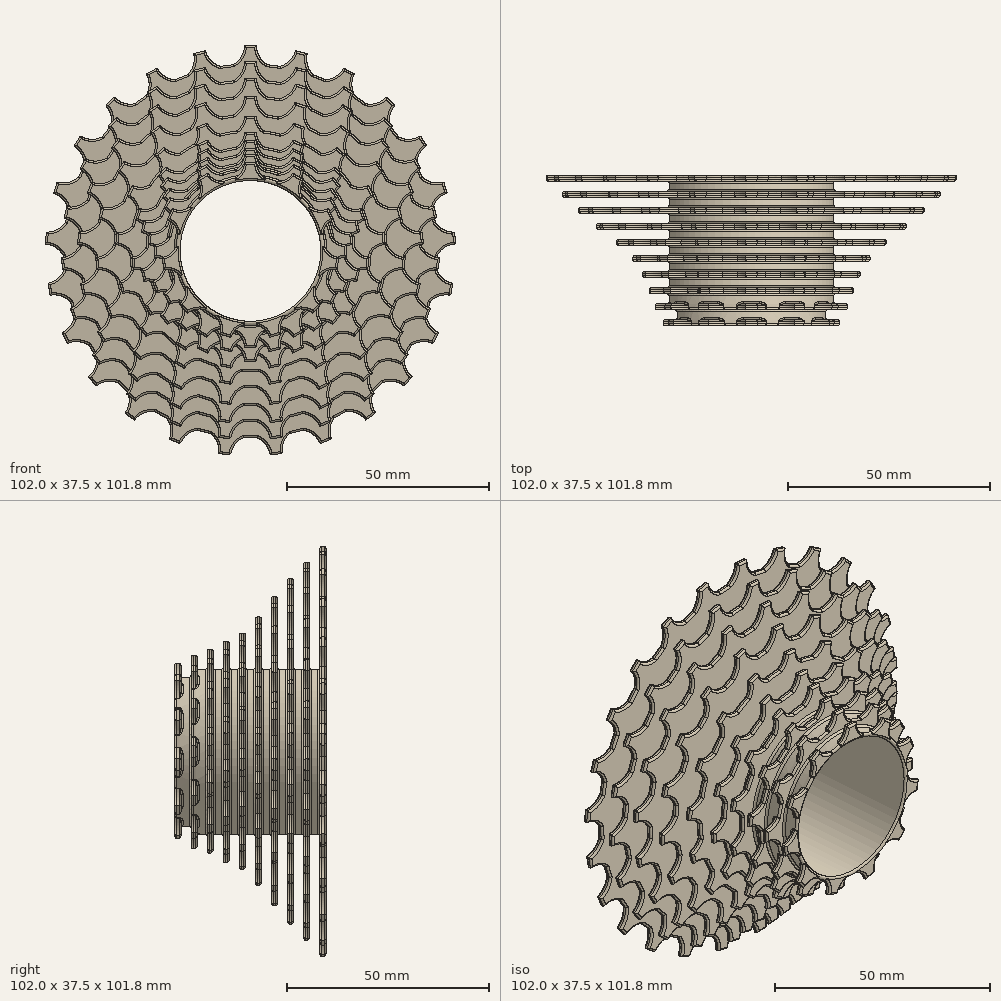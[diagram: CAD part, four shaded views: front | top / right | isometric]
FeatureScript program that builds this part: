
annotation { "Feature Type Name" : "Feature", "Feature Type Description" : "" }
export const myFeature = defineFeature(function(context is Context, id is Id, definition is map)
    precondition{}
    {
        {
            var Q0;
            Q0=qCreatedBy(makeId("Front.planeOp"),FACE);
            var sketch = newSketch(context, id + "F0", { "sketchPlane" : qUnion([Q0])});
            skCircle(sketch, "E0", {"center": v(0, 0) * mm, "radius": 46.5 * mm});
            skLineSegment(sketch, "E1", {"start": v(1.5, 51) * mm, "end": v(-1.5, 51) * mm});
            skLineSegment(sketch, "E2", {"start": v(0, -58.64) * mm, "end": v(0, 66.7) * mm, "construction": true});
            skLineSegment(sketch, "E3", {"start": v(-56.93, 0) * mm, "end": v(57.2, 0) * mm, "construction": true});
            skLineSegment(sketch, "E4", {"start": v(7, 54.15) * mm, "end": v(7, 48.61) * mm, "construction": true});
            skArc(sketch, "E5", {"start": v(1.5, 51) * mm, "mid": v(2.22, 48.3) * mm, "end": v(4.17, 46.31) * mm});
            skArc(sketch, "E6.MirrorCS", {"start": v(-1.5, 51) * mm, "mid": v(-2.22, 48.3) * mm, "end": v(-4.17, 46.31) * mm});
            skLineSegment(sketch, "E7.1.0", {"start": v(-11.23, 49.77) * mm, "end": v(-14.14, 49.02) * mm});
            skArc(sketch, "E7.1.1", {"start": v(-14.14, 49.02) * mm, "mid": v(-14.16, 46.24) * mm, "end": v(-15.56, 43.82) * mm});
            skArc(sketch, "E7.1.2", {"start": v(-11.23, 49.77) * mm, "mid": v(-9.86, 47.34) * mm, "end": v(-7.48, 45.9) * mm});
            skLineSegment(sketch, "E7.2.0", {"start": v(-23.25, 45.41) * mm, "end": v(-25.88, 43.97) * mm});
            skArc(sketch, "E7.2.1", {"start": v(-25.88, 43.97) * mm, "mid": v(-25.22, 41.26) * mm, "end": v(-25.97, 38.58) * mm});
            skArc(sketch, "E7.2.2", {"start": v(-23.25, 45.41) * mm, "mid": v(-21.33, 43.4) * mm, "end": v(-18.66, 42.6) * mm});
            skLineSegment(sketch, "E7.3.0", {"start": v(-33.82, 38.2) * mm, "end": v(-36, 36.15) * mm});
            skArc(sketch, "E7.3.1", {"start": v(-36, 36.15) * mm, "mid": v(-34.69, 33.7) * mm, "end": v(-34.74, 30.9) * mm});
            skArc(sketch, "E7.3.2", {"start": v(-33.82, 38.2) * mm, "mid": v(-31.45, 36.73) * mm, "end": v(-28.66, 36.62) * mm});
            skLineSegment(sketch, "E7.4.0", {"start": v(-42.26, 28.6) * mm, "end": v(-43.86, 26.06) * mm});
            skArc(sketch, "E7.4.1", {"start": v(-43.86, 26.06) * mm, "mid": v(-41.98, 24) * mm, "end": v(-41.34, 21.3) * mm});
            skArc(sketch, "E7.4.2", {"start": v(-42.26, 28.6) * mm, "mid": v(-39.6, 27.76) * mm, "end": v(-36.87, 28.34) * mm});
            skLineSegment(sketch, "E7.5.0", {"start": v(-48.04, 17.19) * mm, "end": v(-48.97, 14.33) * mm});
            skArc(sketch, "E7.5.1", {"start": v(-48.97, 14.33) * mm, "mid": v(-46.63, 12.82) * mm, "end": v(-45.33, 10.35) * mm});
            skArc(sketch, "E7.5.2", {"start": v(-48.04, 17.19) * mm, "mid": v(-45.26, 17.04) * mm, "end": v(-42.76, 18.28) * mm});
            skLineSegment(sketch, "E7.6.0", {"start": v(-50.8, 4.7) * mm, "end": v(-51, 1.7) * mm});
            skArc(sketch, "E7.6.1", {"start": v(-51, 1.7) * mm, "mid": v(-48.35, 0.82) * mm, "end": v(-46.48, -1.25) * mm});
            skArc(sketch, "E7.6.2", {"start": v(-50.8, 4.7) * mm, "mid": v(-48.07, 5.25) * mm, "end": v(-45.96, 7.07) * mm});
            skLineSegment(sketch, "E7.7.0", {"start": v(-50.38, -8.08) * mm, "end": v(-49.82, -11.03) * mm});
            skArc(sketch, "E7.7.1", {"start": v(-49.82, -11.03) * mm, "mid": v(-47.03, -11.23) * mm, "end": v(-44.71, -12.77) * mm});
            skArc(sketch, "E7.7.2", {"start": v(-50.38, -8.08) * mm, "mid": v(-47.87, -6.87) * mm, "end": v(-46.27, -4.58) * mm});
            skLineSegment(sketch, "E7.8.0", {"start": v(-46.78, -20.36) * mm, "end": v(-45.5, -23.07) * mm});
            skArc(sketch, "E7.8.1", {"start": v(-45.5, -23.07) * mm, "mid": v(-42.76, -22.58) * mm, "end": v(-40.13, -23.5) * mm});
            skArc(sketch, "E7.8.2", {"start": v(-46.78, -20.36) * mm, "mid": v(-44.65, -18.56) * mm, "end": v(-43.68, -15.95) * mm});
            skLineSegment(sketch, "E7.9.0", {"start": v(-40.25, -31.35) * mm, "end": v(-38.34, -33.66) * mm});
            skArc(sketch, "E7.9.1", {"start": v(-38.34, -33.66) * mm, "mid": v(-35.8, -32.5) * mm, "end": v(-33.03, -32.73) * mm});
            skArc(sketch, "E7.9.2", {"start": v(-40.25, -31.35) * mm, "mid": v(-38.64, -29.08) * mm, "end": v(-38.34, -26.3) * mm});
            skLineSegment(sketch, "E7.10.0", {"start": v(-31.2, -40.38) * mm, "end": v(-28.76, -42.14) * mm});
            skArc(sketch, "E7.10.1", {"start": v(-28.76, -42.14) * mm, "mid": v(-26.6, -40.39) * mm, "end": v(-23.85, -39.92) * mm});
            skArc(sketch, "E7.10.2", {"start": v(-31.2, -40.38) * mm, "mid": v(-30.2, -37.78) * mm, "end": v(-30.6, -35.02) * mm});
            skLineSegment(sketch, "E7.11.0", {"start": v(-20.17, -46.87) * mm, "end": v(-17.38, -47.97) * mm});
            skArc(sketch, "E7.11.1", {"start": v(-17.38, -47.97) * mm, "mid": v(-15.72, -45.73) * mm, "end": v(-13.17, -44.6) * mm});
            skArc(sketch, "E7.11.2", {"start": v(-20.17, -46.87) * mm, "mid": v(-19.85, -44.1) * mm, "end": v(-20.93, -41.53) * mm});
            skLineSegment(sketch, "E7.12.0", {"start": v(-7.88, -50.4) * mm, "end": v(-4.9, -50.79) * mm});
            skArc(sketch, "E7.12.1", {"start": v(-4.9, -50.79) * mm, "mid": v(-3.85, -48.2) * mm, "end": v(-1.67, -46.47) * mm});
            skArc(sketch, "E7.12.2", {"start": v(-7.88, -50.4) * mm, "mid": v(-8.26, -47.65) * mm, "end": v(-9.94, -45.42) * mm});
            skLineSegment(sketch, "E7.13.0", {"start": v(4.9, -50.79) * mm, "end": v(7.88, -50.4) * mm});
            skArc(sketch, "E7.13.1", {"start": v(7.88, -50.4) * mm, "mid": v(8.26, -47.65) * mm, "end": v(9.94, -45.42) * mm});
            skArc(sketch, "E7.13.2", {"start": v(4.9, -50.79) * mm, "mid": v(3.85, -48.2) * mm, "end": v(1.67, -46.47) * mm});
            skLineSegment(sketch, "E7.14.0", {"start": v(17.38, -47.97) * mm, "end": v(20.17, -46.87) * mm});
            skArc(sketch, "E7.14.1", {"start": v(20.17, -46.87) * mm, "mid": v(19.85, -44.1) * mm, "end": v(20.93, -41.53) * mm});
            skArc(sketch, "E7.14.2", {"start": v(17.38, -47.97) * mm, "mid": v(15.72, -45.73) * mm, "end": v(13.17, -44.6) * mm});
            skLineSegment(sketch, "E7.15.0", {"start": v(28.76, -42.14) * mm, "end": v(31.2, -40.38) * mm});
            skArc(sketch, "E7.15.1", {"start": v(31.2, -40.38) * mm, "mid": v(30.2, -37.78) * mm, "end": v(30.6, -35.02) * mm});
            skArc(sketch, "E7.15.2", {"start": v(28.76, -42.14) * mm, "mid": v(26.6, -40.39) * mm, "end": v(23.85, -39.92) * mm});
            skLineSegment(sketch, "E7.16.0", {"start": v(38.34, -33.66) * mm, "end": v(40.25, -31.35) * mm});
            skArc(sketch, "E7.16.1", {"start": v(40.25, -31.35) * mm, "mid": v(38.64, -29.08) * mm, "end": v(38.34, -26.3) * mm});
            skArc(sketch, "E7.16.2", {"start": v(38.34, -33.66) * mm, "mid": v(35.8, -32.5) * mm, "end": v(33.03, -32.73) * mm});
            skLineSegment(sketch, "E7.17.0", {"start": v(45.5, -23.07) * mm, "end": v(46.78, -20.36) * mm});
            skArc(sketch, "E7.17.1", {"start": v(46.78, -20.36) * mm, "mid": v(44.65, -18.56) * mm, "end": v(43.68, -15.95) * mm});
            skArc(sketch, "E7.17.2", {"start": v(45.5, -23.07) * mm, "mid": v(42.76, -22.58) * mm, "end": v(40.13, -23.5) * mm});
            skLineSegment(sketch, "E7.18.0", {"start": v(49.82, -11.03) * mm, "end": v(50.38, -8.08) * mm});
            skArc(sketch, "E7.18.1", {"start": v(50.38, -8.08) * mm, "mid": v(47.87, -6.87) * mm, "end": v(46.27, -4.58) * mm});
            skArc(sketch, "E7.18.2", {"start": v(49.82, -11.03) * mm, "mid": v(47.03, -11.23) * mm, "end": v(44.71, -12.77) * mm});
            skLineSegment(sketch, "E7.19.0", {"start": v(51, 1.7) * mm, "end": v(50.8, 4.7) * mm});
            skArc(sketch, "E7.19.1", {"start": v(50.8, 4.7) * mm, "mid": v(48.07, 5.25) * mm, "end": v(45.96, 7.07) * mm});
            skArc(sketch, "E7.19.2", {"start": v(51, 1.7) * mm, "mid": v(48.35, 0.82) * mm, "end": v(46.48, -1.25) * mm});
            skLineSegment(sketch, "E7.20.0", {"start": v(48.97, 14.33) * mm, "end": v(48.04, 17.19) * mm});
            skArc(sketch, "E7.20.1", {"start": v(48.04, 17.19) * mm, "mid": v(45.26, 17.04) * mm, "end": v(42.76, 18.28) * mm});
            skArc(sketch, "E7.20.2", {"start": v(48.97, 14.33) * mm, "mid": v(46.63, 12.82) * mm, "end": v(45.33, 10.35) * mm});
            skLineSegment(sketch, "E7.21.0", {"start": v(43.86, 26.06) * mm, "end": v(42.26, 28.6) * mm});
            skArc(sketch, "E7.21.1", {"start": v(42.26, 28.6) * mm, "mid": v(39.6, 27.76) * mm, "end": v(36.87, 28.34) * mm});
            skArc(sketch, "E7.21.2", {"start": v(43.86, 26.06) * mm, "mid": v(41.98, 24) * mm, "end": v(41.34, 21.3) * mm});
            skLineSegment(sketch, "E7.22.0", {"start": v(36, 36.15) * mm, "end": v(33.82, 38.2) * mm});
            skArc(sketch, "E7.22.1", {"start": v(33.82, 38.2) * mm, "mid": v(31.45, 36.73) * mm, "end": v(28.66, 36.62) * mm});
            skArc(sketch, "E7.22.2", {"start": v(36, 36.15) * mm, "mid": v(34.69, 33.7) * mm, "end": v(34.74, 30.9) * mm});
            skLineSegment(sketch, "E7.23.0", {"start": v(25.88, 43.97) * mm, "end": v(23.25, 45.41) * mm});
            skArc(sketch, "E7.23.1", {"start": v(23.25, 45.41) * mm, "mid": v(21.33, 43.4) * mm, "end": v(18.66, 42.6) * mm});
            skArc(sketch, "E7.23.2", {"start": v(25.88, 43.97) * mm, "mid": v(25.22, 41.26) * mm, "end": v(25.97, 38.58) * mm});
            skLineSegment(sketch, "E7.24.0", {"start": v(14.14, 49.02) * mm, "end": v(11.23, 49.77) * mm});
            skArc(sketch, "E7.24.1", {"start": v(11.23, 49.77) * mm, "mid": v(9.86, 47.34) * mm, "end": v(7.48, 45.9) * mm});
            skArc(sketch, "E7.24.2", {"start": v(14.14, 49.02) * mm, "mid": v(14.16, 46.24) * mm, "end": v(15.56, 43.82) * mm});
            skCircle(sketch, "E8", {"center": v(0, 0) * mm, "radius": 17.5 * mm});
            skSolve(sketch);
        }
        {
            var Q0;
            Q0 = qSketchRegion(id + "F0", true);
            extrude(context, id + "F1", {"entities" : qUnion([Q0]), "depth" : 1.5 * mm, "offsetDistance" : 25 * mm});
        }
        {
            var Q0;
            Q0=makeQuery(id+"F1.opExtrude","CAP_FACE",FACE,{"disambiguationData":[OSD([sQuery(id+"F0.wireOp",EDGE,"E0"),sQuery(id+"F0.wireOp",EDGE,"E1"),sQuery(id+"F0.wireOp",EDGE,"E5"),sQuery(id+"F0.wireOp",EDGE,"E6.MirrorCS"),sQuery(id+"F0.wireOp",EDGE,"E7.1.0"),sQuery(id+"F0.wireOp",EDGE,"E7.1.1"),sQuery(id+"F0.wireOp",EDGE,"E7.1.2"),sQuery(id+"F0.wireOp",EDGE,"E7.2.0"),sQuery(id+"F0.wireOp",EDGE,"E7.2.1"),sQuery(id+"F0.wireOp",EDGE,"E7.2.2"),sQuery(id+"F0.wireOp",EDGE,"E7.3.0"),sQuery(id+"F0.wireOp",EDGE,"E7.3.1"),sQuery(id+"F0.wireOp",EDGE,"E7.3.2"),sQuery(id+"F0.wireOp",EDGE,"E7.4.0"),sQuery(id+"F0.wireOp",EDGE,"E7.4.1"),sQuery(id+"F0.wireOp",EDGE,"E7.4.2"),sQuery(id+"F0.wireOp",EDGE,"E7.5.0"),sQuery(id+"F0.wireOp",EDGE,"E7.5.1"),sQuery(id+"F0.wireOp",EDGE,"E7.5.2"),sQuery(id+"F0.wireOp",EDGE,"E7.6.0"),sQuery(id+"F0.wireOp",EDGE,"E7.6.1"),sQuery(id+"F0.wireOp",EDGE,"E7.6.2"),sQuery(id+"F0.wireOp",EDGE,"E7.7.0"),sQuery(id+"F0.wireOp",EDGE,"E7.7.1"),sQuery(id+"F0.wireOp",EDGE,"E7.7.2"),sQuery(id+"F0.wireOp",EDGE,"E7.8.0"),sQuery(id+"F0.wireOp",EDGE,"E7.8.1"),sQuery(id+"F0.wireOp",EDGE,"E7.8.2"),sQuery(id+"F0.wireOp",EDGE,"E7.9.0"),sQuery(id+"F0.wireOp",EDGE,"E7.9.1"),sQuery(id+"F0.wireOp",EDGE,"E7.9.2"),sQuery(id+"F0.wireOp",EDGE,"E7.10.0"),sQuery(id+"F0.wireOp",EDGE,"E7.10.1"),sQuery(id+"F0.wireOp",EDGE,"E7.10.2"),sQuery(id+"F0.wireOp",EDGE,"E7.11.0"),sQuery(id+"F0.wireOp",EDGE,"E7.11.1"),sQuery(id+"F0.wireOp",EDGE,"E7.11.2"),sQuery(id+"F0.wireOp",EDGE,"E7.12.0"),sQuery(id+"F0.wireOp",EDGE,"E7.12.1"),sQuery(id+"F0.wireOp",EDGE,"E7.12.2"),sQuery(id+"F0.wireOp",EDGE,"E7.13.0"),sQuery(id+"F0.wireOp",EDGE,"E7.13.1"),sQuery(id+"F0.wireOp",EDGE,"E7.13.2"),sQuery(id+"F0.wireOp",EDGE,"E7.14.0"),sQuery(id+"F0.wireOp",EDGE,"E7.14.1"),sQuery(id+"F0.wireOp",EDGE,"E7.14.2"),sQuery(id+"F0.wireOp",EDGE,"E7.15.0"),sQuery(id+"F0.wireOp",EDGE,"E7.15.1"),sQuery(id+"F0.wireOp",EDGE,"E7.15.2"),sQuery(id+"F0.wireOp",EDGE,"E7.16.0"),sQuery(id+"F0.wireOp",EDGE,"E7.16.1"),sQuery(id+"F0.wireOp",EDGE,"E7.16.2"),sQuery(id+"F0.wireOp",EDGE,"E7.17.0"),sQuery(id+"F0.wireOp",EDGE,"E7.17.1"),sQuery(id+"F0.wireOp",EDGE,"E7.17.2"),sQuery(id+"F0.wireOp",EDGE,"E7.18.0"),sQuery(id+"F0.wireOp",EDGE,"E7.18.1"),sQuery(id+"F0.wireOp",EDGE,"E7.18.2"),sQuery(id+"F0.wireOp",EDGE,"E7.19.0"),sQuery(id+"F0.wireOp",EDGE,"E7.19.1"),sQuery(id+"F0.wireOp",EDGE,"E7.19.2"),sQuery(id+"F0.wireOp",EDGE,"E7.20.0"),sQuery(id+"F0.wireOp",EDGE,"E7.20.1"),sQuery(id+"F0.wireOp",EDGE,"E7.20.2"),sQuery(id+"F0.wireOp",EDGE,"E7.21.0"),sQuery(id+"F0.wireOp",EDGE,"E7.21.1"),sQuery(id+"F0.wireOp",EDGE,"E7.21.2"),sQuery(id+"F0.wireOp",EDGE,"E7.22.0"),sQuery(id+"F0.wireOp",EDGE,"E7.22.1"),sQuery(id+"F0.wireOp",EDGE,"E7.22.2"),sQuery(id+"F0.wireOp",EDGE,"E7.23.0"),sQuery(id+"F0.wireOp",EDGE,"E7.23.1"),sQuery(id+"F0.wireOp",EDGE,"E7.23.2"),sQuery(id+"F0.wireOp",EDGE,"E7.24.0"),sQuery(id+"F0.wireOp",EDGE,"E7.24.1"),sQuery(id+"F0.wireOp",EDGE,"E7.24.2"),sQuery(id+"F0.wireOp",EDGE,"E8")])],"isStart":false});
            var sketch = newSketch(context, id + "F2", { "sketchPlane" : qUnion([Q0])});
            skCircle(sketch, "E9", {"center": v(0, 0) * mm, "radius": 20.5 * mm});
            skCircle(sketch, "E10", {"center": v(0, 0) * mm, "radius": 17.5 * mm});
            skSolve(sketch);
        }
        {
            var Q0;
            Q0 = qSketchRegion(id + "F2", true);
            extrude(context, id + "F3", {"entities" : qUnion([Q0]), "operationType" : NewBodyOperationType.ADD, "depth" : 2.5 * mm, "offsetDistance" : 25 * mm});
        }
        {
            var Q0;
            Q0=makeQuery(id+"F3.opExtrude","CAP_FACE",FACE,{"disambiguationData":[OSD([sQuery(id+"F2.wireOp",EDGE,"E9"),sQuery(id+"F2.wireOp",EDGE,"E10")])],"isStart":false});
            var sketch = newSketch(context, id + "F4", { "sketchPlane" : qUnion([Q0])});
            skCircle(sketch, "E11", {"center": v(0, 0) * mm, "radius": 42.5 * mm});
            skLineSegment(sketch, "E12", {"start": v(-1.5, 47) * mm, "end": v(1.5, 47) * mm});
            skArc(sketch, "E13", {"start": v(1.5, 47) * mm, "mid": v(2.2, 44.3) * mm, "end": v(4.15, 42.3) * mm});
            skArc(sketch, "E14.MirrorCS", {"start": v(-1.5, 47) * mm, "mid": v(-2.2, 44.3) * mm, "end": v(-4.15, 42.3) * mm});
            skLineSegment(sketch, "E15.1.0", {"start": v(-14.12, 44.85) * mm, "end": v(-11.24, 45.66) * mm});
            skArc(sketch, "E15.1.1", {"start": v(-14.12, 44.85) * mm, "mid": v(-14.08, 42.06) * mm, "end": v(-15.4, 39.6) * mm});
            skArc(sketch, "E15.1.2", {"start": v(-11.24, 45.66) * mm, "mid": v(-9.83, 43.25) * mm, "end": v(-7.42, 41.85) * mm});
            skLineSegment(sketch, "E15.2.0", {"start": v(-25.7, 39.38) * mm, "end": v(-23.14, 40.94) * mm});
            skArc(sketch, "E15.2.1", {"start": v(-25.7, 39.38) * mm, "mid": v(-24.9, 36.7) * mm, "end": v(-25.52, 33.98) * mm});
            skArc(sketch, "E15.2.2", {"start": v(-23.14, 40.94) * mm, "mid": v(-21.13, 39) * mm, "end": v(-18.43, 38.3) * mm});
            skLineSegment(sketch, "E15.3.0", {"start": v(-35.37, 30.98) * mm, "end": v(-33.33, 33.18) * mm});
            skArc(sketch, "E15.3.1", {"start": v(-35.37, 30.98) * mm, "mid": v(-33.88, 28.62) * mm, "end": v(-33.74, 25.84) * mm});
            skArc(sketch, "E15.3.2", {"start": v(-33.33, 33.18) * mm, "mid": v(-30.87, 31.85) * mm, "end": v(-28.08, 31.9) * mm});
            skLineSegment(sketch, "E15.4.0", {"start": v(-42.42, 20.3) * mm, "end": v(-41.04, 22.95) * mm});
            skArc(sketch, "E15.4.1", {"start": v(-42.42, 20.3) * mm, "mid": v(-40.35, 18.42) * mm, "end": v(-39.46, 15.78) * mm});
            skArc(sketch, "E15.4.2", {"start": v(-41.04, 22.95) * mm, "mid": v(-38.32, 22.34) * mm, "end": v(-35.65, 23.14) * mm});
            skLineSegment(sketch, "E15.5.0", {"start": v(-46.32, 8.1) * mm, "end": v(-45.71, 11.03) * mm});
            skArc(sketch, "E15.5.1", {"start": v(-46.32, 8.1) * mm, "mid": v(-43.82, 6.85) * mm, "end": v(-42.26, 4.54) * mm});
            skArc(sketch, "E15.5.2", {"start": v(-45.71, 11.03) * mm, "mid": v(-42.93, 11.17) * mm, "end": v(-40.57, 12.67) * mm});
            skLineSegment(sketch, "E15.6.0", {"start": v(-46.79, -4.7) * mm, "end": v(-47, -1.71) * mm});
            skArc(sketch, "E15.6.1", {"start": v(-46.79, -4.7) * mm, "mid": v(-44.05, -5.23) * mm, "end": v(-41.92, -7.03) * mm});
            skArc(sketch, "E15.6.2", {"start": v(-47, -1.71) * mm, "mid": v(-44.35, -0.82) * mm, "end": v(-42.48, 1.25) * mm});
            skLineSegment(sketch, "E15.7.0", {"start": v(-43.78, -17.15) * mm, "end": v(-44.79, -14.33) * mm});
            skArc(sketch, "E15.7.1", {"start": v(-43.78, -17.15) * mm, "mid": v(-41, -16.92) * mm, "end": v(-38.47, -18.07) * mm});
            skArc(sketch, "E15.7.2", {"start": v(-44.79, -14.33) * mm, "mid": v(-42.48, -12.76) * mm, "end": v(-41.24, -10.26) * mm});
            skLineSegment(sketch, "E15.8.0", {"start": v(-37.53, -28.33) * mm, "end": v(-39.26, -25.88) * mm});
            skArc(sketch, "E15.8.1", {"start": v(-37.53, -28.33) * mm, "mid": v(-34.92, -27.35) * mm, "end": v(-32.16, -27.78) * mm});
            skArc(sketch, "E15.8.2", {"start": v(-39.26, -25.88) * mm, "mid": v(-37.47, -23.74) * mm, "end": v(-36.95, -21) * mm});
            skLineSegment(sketch, "E15.9.0", {"start": v(-28.5, -37.4) * mm, "end": v(-30.82, -35.51) * mm});
            skArc(sketch, "E15.9.1", {"start": v(-28.5, -37.4) * mm, "mid": v(-26.25, -35.76) * mm, "end": v(-23.48, -35.43) * mm});
            skArc(sketch, "E15.9.2", {"start": v(-30.82, -35.51) * mm, "mid": v(-29.67, -32.97) * mm, "end": v(-29.91, -30.2) * mm});
            skLineSegment(sketch, "E15.10.0", {"start": v(-17.35, -43.7) * mm, "end": v(-20.1, -42.51) * mm});
            skArc(sketch, "E15.10.1", {"start": v(-17.35, -43.7) * mm, "mid": v(-15.62, -41.51) * mm, "end": v(-13.05, -40.45) * mm});
            skArc(sketch, "E15.10.2", {"start": v(-20.1, -42.51) * mm, "mid": v(-19.67, -39.75) * mm, "end": v(-20.66, -37.14) * mm});
            skLineSegment(sketch, "E15.11.0", {"start": v(-4.91, -46.77) * mm, "end": v(-7.89, -46.36) * mm});
            skArc(sketch, "E15.11.1", {"start": v(-4.91, -46.77) * mm, "mid": v(-3.85, -44.19) * mm, "end": v(-1.65, -42.47) * mm});
            skArc(sketch, "E15.11.2", {"start": v(-7.89, -46.36) * mm, "mid": v(-8.22, -43.59) * mm, "end": v(-9.87, -41.34) * mm});
            skLineSegment(sketch, "E15.12.0", {"start": v(7.89, -46.36) * mm, "end": v(4.91, -46.77) * mm});
            skArc(sketch, "E15.12.1", {"start": v(7.89, -46.36) * mm, "mid": v(8.22, -43.59) * mm, "end": v(9.87, -41.34) * mm});
            skArc(sketch, "E15.12.2", {"start": v(4.91, -46.77) * mm, "mid": v(3.85, -44.19) * mm, "end": v(1.65, -42.47) * mm});
            skLineSegment(sketch, "E15.13.0", {"start": v(20.1, -42.51) * mm, "end": v(17.35, -43.7) * mm});
            skArc(sketch, "E15.13.1", {"start": v(20.1, -42.51) * mm, "mid": v(19.67, -39.75) * mm, "end": v(20.66, -37.14) * mm});
            skArc(sketch, "E15.13.2", {"start": v(17.35, -43.7) * mm, "mid": v(15.62, -41.51) * mm, "end": v(13.05, -40.45) * mm});
            skLineSegment(sketch, "E15.14.0", {"start": v(30.82, -35.51) * mm, "end": v(28.5, -37.4) * mm});
            skArc(sketch, "E15.14.1", {"start": v(30.82, -35.51) * mm, "mid": v(29.67, -32.97) * mm, "end": v(29.91, -30.2) * mm});
            skArc(sketch, "E15.14.2", {"start": v(28.5, -37.4) * mm, "mid": v(26.25, -35.76) * mm, "end": v(23.48, -35.43) * mm});
            skLineSegment(sketch, "E15.15.0", {"start": v(39.26, -25.88) * mm, "end": v(37.53, -28.33) * mm});
            skArc(sketch, "E15.15.1", {"start": v(39.26, -25.88) * mm, "mid": v(37.47, -23.74) * mm, "end": v(36.95, -21) * mm});
            skArc(sketch, "E15.15.2", {"start": v(37.53, -28.33) * mm, "mid": v(34.92, -27.35) * mm, "end": v(32.16, -27.78) * mm});
            skLineSegment(sketch, "E15.16.0", {"start": v(44.79, -14.33) * mm, "end": v(43.78, -17.15) * mm});
            skArc(sketch, "E15.16.1", {"start": v(44.79, -14.33) * mm, "mid": v(42.48, -12.76) * mm, "end": v(41.24, -10.26) * mm});
            skArc(sketch, "E15.16.2", {"start": v(43.78, -17.15) * mm, "mid": v(41, -16.92) * mm, "end": v(38.47, -18.07) * mm});
            skLineSegment(sketch, "E15.17.0", {"start": v(47, -1.71) * mm, "end": v(46.79, -4.7) * mm});
            skArc(sketch, "E15.17.1", {"start": v(47, -1.71) * mm, "mid": v(44.35, -0.82) * mm, "end": v(42.48, 1.25) * mm});
            skArc(sketch, "E15.17.2", {"start": v(46.79, -4.7) * mm, "mid": v(44.05, -5.23) * mm, "end": v(41.92, -7.03) * mm});
            skLineSegment(sketch, "E15.18.0", {"start": v(45.71, 11.03) * mm, "end": v(46.32, 8.1) * mm});
            skArc(sketch, "E15.18.1", {"start": v(45.71, 11.03) * mm, "mid": v(42.93, 11.17) * mm, "end": v(40.57, 12.67) * mm});
            skArc(sketch, "E15.18.2", {"start": v(46.32, 8.1) * mm, "mid": v(43.82, 6.85) * mm, "end": v(42.26, 4.54) * mm});
            skLineSegment(sketch, "E15.19.0", {"start": v(41.04, 22.95) * mm, "end": v(42.42, 20.3) * mm});
            skArc(sketch, "E15.19.1", {"start": v(41.04, 22.95) * mm, "mid": v(38.32, 22.34) * mm, "end": v(35.65, 23.14) * mm});
            skArc(sketch, "E15.19.2", {"start": v(42.42, 20.3) * mm, "mid": v(40.35, 18.42) * mm, "end": v(39.46, 15.78) * mm});
            skLineSegment(sketch, "E15.20.0", {"start": v(33.33, 33.18) * mm, "end": v(35.37, 30.98) * mm});
            skArc(sketch, "E15.20.1", {"start": v(33.33, 33.18) * mm, "mid": v(30.87, 31.85) * mm, "end": v(28.08, 31.9) * mm});
            skArc(sketch, "E15.20.2", {"start": v(35.37, 30.98) * mm, "mid": v(33.88, 28.62) * mm, "end": v(33.74, 25.84) * mm});
            skLineSegment(sketch, "E15.21.0", {"start": v(23.14, 40.94) * mm, "end": v(25.7, 39.38) * mm});
            skArc(sketch, "E15.21.1", {"start": v(23.14, 40.94) * mm, "mid": v(21.13, 39) * mm, "end": v(18.43, 38.3) * mm});
            skArc(sketch, "E15.21.2", {"start": v(25.7, 39.38) * mm, "mid": v(24.9, 36.7) * mm, "end": v(25.52, 33.98) * mm});
            skLineSegment(sketch, "E15.22.0", {"start": v(11.24, 45.66) * mm, "end": v(14.12, 44.85) * mm});
            skArc(sketch, "E15.22.1", {"start": v(11.24, 45.66) * mm, "mid": v(9.83, 43.25) * mm, "end": v(7.42, 41.85) * mm});
            skArc(sketch, "E15.22.2", {"start": v(14.12, 44.85) * mm, "mid": v(14.08, 42.06) * mm, "end": v(15.4, 39.6) * mm});
            skCircle(sketch, "E16", {"center": v(0, 0) * mm, "radius": 17.5 * mm});
            skSolve(sketch);
        }
        {
            var Q0;
            Q0 = qSketchRegion(id + "F4", true);
            extrude(context, id + "F5", {"entities" : qUnion([Q0]), "operationType" : NewBodyOperationType.ADD, "depth" : 1.5 * mm, "offsetDistance" : 25 * mm});
        }
        {
            var Q0;
            Q0=makeQuery(id+"F5.opExtrude","CAP_FACE",FACE,{"disambiguationData":[OSD([sQuery(id+"F4.wireOp",EDGE,"E11"),sQuery(id+"F4.wireOp",EDGE,"E12"),sQuery(id+"F4.wireOp",EDGE,"E13"),sQuery(id+"F4.wireOp",EDGE,"E14.MirrorCS"),sQuery(id+"F4.wireOp",EDGE,"E15.1.0"),sQuery(id+"F4.wireOp",EDGE,"E15.1.1"),sQuery(id+"F4.wireOp",EDGE,"E15.1.2"),sQuery(id+"F4.wireOp",EDGE,"E15.2.0"),sQuery(id+"F4.wireOp",EDGE,"E15.2.1"),sQuery(id+"F4.wireOp",EDGE,"E15.2.2"),sQuery(id+"F4.wireOp",EDGE,"E15.3.0"),sQuery(id+"F4.wireOp",EDGE,"E15.3.1"),sQuery(id+"F4.wireOp",EDGE,"E15.3.2"),sQuery(id+"F4.wireOp",EDGE,"E15.4.0"),sQuery(id+"F4.wireOp",EDGE,"E15.4.1"),sQuery(id+"F4.wireOp",EDGE,"E15.4.2"),sQuery(id+"F4.wireOp",EDGE,"E15.5.0"),sQuery(id+"F4.wireOp",EDGE,"E15.5.1"),sQuery(id+"F4.wireOp",EDGE,"E15.5.2"),sQuery(id+"F4.wireOp",EDGE,"E15.6.0"),sQuery(id+"F4.wireOp",EDGE,"E15.6.1"),sQuery(id+"F4.wireOp",EDGE,"E15.6.2"),sQuery(id+"F4.wireOp",EDGE,"E15.7.0"),sQuery(id+"F4.wireOp",EDGE,"E15.7.1"),sQuery(id+"F4.wireOp",EDGE,"E15.7.2"),sQuery(id+"F4.wireOp",EDGE,"E15.8.0"),sQuery(id+"F4.wireOp",EDGE,"E15.8.1"),sQuery(id+"F4.wireOp",EDGE,"E15.8.2"),sQuery(id+"F4.wireOp",EDGE,"E15.9.0"),sQuery(id+"F4.wireOp",EDGE,"E15.9.1"),sQuery(id+"F4.wireOp",EDGE,"E15.9.2"),sQuery(id+"F4.wireOp",EDGE,"E15.10.0"),sQuery(id+"F4.wireOp",EDGE,"E15.10.1"),sQuery(id+"F4.wireOp",EDGE,"E15.10.2"),sQuery(id+"F4.wireOp",EDGE,"E15.11.0"),sQuery(id+"F4.wireOp",EDGE,"E15.11.1"),sQuery(id+"F4.wireOp",EDGE,"E15.11.2"),sQuery(id+"F4.wireOp",EDGE,"E15.12.0"),sQuery(id+"F4.wireOp",EDGE,"E15.12.1"),sQuery(id+"F4.wireOp",EDGE,"E15.12.2"),sQuery(id+"F4.wireOp",EDGE,"E15.13.0"),sQuery(id+"F4.wireOp",EDGE,"E15.13.1"),sQuery(id+"F4.wireOp",EDGE,"E15.13.2"),sQuery(id+"F4.wireOp",EDGE,"E15.14.0"),sQuery(id+"F4.wireOp",EDGE,"E15.14.1"),sQuery(id+"F4.wireOp",EDGE,"E15.14.2"),sQuery(id+"F4.wireOp",EDGE,"E15.15.0"),sQuery(id+"F4.wireOp",EDGE,"E15.15.1"),sQuery(id+"F4.wireOp",EDGE,"E15.15.2"),sQuery(id+"F4.wireOp",EDGE,"E15.16.0"),sQuery(id+"F4.wireOp",EDGE,"E15.16.1"),sQuery(id+"F4.wireOp",EDGE,"E15.16.2"),sQuery(id+"F4.wireOp",EDGE,"E15.17.0"),sQuery(id+"F4.wireOp",EDGE,"E15.17.1"),sQuery(id+"F4.wireOp",EDGE,"E15.17.2"),sQuery(id+"F4.wireOp",EDGE,"E15.18.0"),sQuery(id+"F4.wireOp",EDGE,"E15.18.1"),sQuery(id+"F4.wireOp",EDGE,"E15.18.2"),sQuery(id+"F4.wireOp",EDGE,"E15.19.0"),sQuery(id+"F4.wireOp",EDGE,"E15.19.1"),sQuery(id+"F4.wireOp",EDGE,"E15.19.2"),sQuery(id+"F4.wireOp",EDGE,"E15.20.0"),sQuery(id+"F4.wireOp",EDGE,"E15.20.1"),sQuery(id+"F4.wireOp",EDGE,"E15.20.2"),sQuery(id+"F4.wireOp",EDGE,"E15.21.0"),sQuery(id+"F4.wireOp",EDGE,"E15.21.1"),sQuery(id+"F4.wireOp",EDGE,"E15.21.2"),sQuery(id+"F4.wireOp",EDGE,"E15.22.0"),sQuery(id+"F4.wireOp",EDGE,"E15.22.1"),sQuery(id+"F4.wireOp",EDGE,"E15.22.2"),sQuery(id+"F4.wireOp",EDGE,"E16")])],"isStart":false});
            var sketch = newSketch(context, id + "F6", { "sketchPlane" : qUnion([Q0])});
            skCircle(sketch, "E17", {"center": v(0, 0) * mm, "radius": 17.5 * mm});
            skCircle(sketch, "E18", {"center": v(0, 0) * mm, "radius": 20.5 * mm});
            skSolve(sketch);
        }
        {
            var Q0;
            Q0 = qSketchRegion(id + "F6", true);
            extrude(context, id + "F7", {"entities" : qUnion([Q0]), "operationType" : NewBodyOperationType.ADD, "depth" : 2.5 * mm, "offsetDistance" : 25 * mm});
        }
        {
            var Q0;
            Q0=makeQuery(id+"F3.opExtrude","SWEPT_FACE",FACE,{"disambiguationData":[OSD([sQuery(id+"F2.wireOp",EDGE,"E9")])]});
            var Q1;
            Q1=makeQuery(id+"F1.opExtrude","CAP_FACE",FACE,{"disambiguationData":[OSD([sQuery(id+"F0.wireOp",EDGE,"E0"),sQuery(id+"F0.wireOp",EDGE,"E1"),sQuery(id+"F0.wireOp",EDGE,"E5"),sQuery(id+"F0.wireOp",EDGE,"E6.MirrorCS"),sQuery(id+"F0.wireOp",EDGE,"E7.1.0"),sQuery(id+"F0.wireOp",EDGE,"E7.1.1"),sQuery(id+"F0.wireOp",EDGE,"E7.1.2"),sQuery(id+"F0.wireOp",EDGE,"E7.2.0"),sQuery(id+"F0.wireOp",EDGE,"E7.2.1"),sQuery(id+"F0.wireOp",EDGE,"E7.2.2"),sQuery(id+"F0.wireOp",EDGE,"E7.3.0"),sQuery(id+"F0.wireOp",EDGE,"E7.3.1"),sQuery(id+"F0.wireOp",EDGE,"E7.3.2"),sQuery(id+"F0.wireOp",EDGE,"E7.4.0"),sQuery(id+"F0.wireOp",EDGE,"E7.4.1"),sQuery(id+"F0.wireOp",EDGE,"E7.4.2"),sQuery(id+"F0.wireOp",EDGE,"E7.5.0"),sQuery(id+"F0.wireOp",EDGE,"E7.5.1"),sQuery(id+"F0.wireOp",EDGE,"E7.5.2"),sQuery(id+"F0.wireOp",EDGE,"E7.6.0"),sQuery(id+"F0.wireOp",EDGE,"E7.6.1"),sQuery(id+"F0.wireOp",EDGE,"E7.6.2"),sQuery(id+"F0.wireOp",EDGE,"E7.7.0"),sQuery(id+"F0.wireOp",EDGE,"E7.7.1"),sQuery(id+"F0.wireOp",EDGE,"E7.7.2"),sQuery(id+"F0.wireOp",EDGE,"E7.8.0"),sQuery(id+"F0.wireOp",EDGE,"E7.8.1"),sQuery(id+"F0.wireOp",EDGE,"E7.8.2"),sQuery(id+"F0.wireOp",EDGE,"E7.9.0"),sQuery(id+"F0.wireOp",EDGE,"E7.9.1"),sQuery(id+"F0.wireOp",EDGE,"E7.9.2"),sQuery(id+"F0.wireOp",EDGE,"E7.10.0"),sQuery(id+"F0.wireOp",EDGE,"E7.10.1"),sQuery(id+"F0.wireOp",EDGE,"E7.10.2"),sQuery(id+"F0.wireOp",EDGE,"E7.11.0"),sQuery(id+"F0.wireOp",EDGE,"E7.11.1"),sQuery(id+"F0.wireOp",EDGE,"E7.11.2"),sQuery(id+"F0.wireOp",EDGE,"E7.12.0"),sQuery(id+"F0.wireOp",EDGE,"E7.12.1"),sQuery(id+"F0.wireOp",EDGE,"E7.12.2"),sQuery(id+"F0.wireOp",EDGE,"E7.13.0"),sQuery(id+"F0.wireOp",EDGE,"E7.13.1"),sQuery(id+"F0.wireOp",EDGE,"E7.13.2"),sQuery(id+"F0.wireOp",EDGE,"E7.14.0"),sQuery(id+"F0.wireOp",EDGE,"E7.14.1"),sQuery(id+"F0.wireOp",EDGE,"E7.14.2"),sQuery(id+"F0.wireOp",EDGE,"E7.15.0"),sQuery(id+"F0.wireOp",EDGE,"E7.15.1"),sQuery(id+"F0.wireOp",EDGE,"E7.15.2"),sQuery(id+"F0.wireOp",EDGE,"E7.16.0"),sQuery(id+"F0.wireOp",EDGE,"E7.16.1"),sQuery(id+"F0.wireOp",EDGE,"E7.16.2"),sQuery(id+"F0.wireOp",EDGE,"E7.17.0"),sQuery(id+"F0.wireOp",EDGE,"E7.17.1"),sQuery(id+"F0.wireOp",EDGE,"E7.17.2"),sQuery(id+"F0.wireOp",EDGE,"E7.18.0"),sQuery(id+"F0.wireOp",EDGE,"E7.18.1"),sQuery(id+"F0.wireOp",EDGE,"E7.18.2"),sQuery(id+"F0.wireOp",EDGE,"E7.19.0"),sQuery(id+"F0.wireOp",EDGE,"E7.19.1"),sQuery(id+"F0.wireOp",EDGE,"E7.19.2"),sQuery(id+"F0.wireOp",EDGE,"E7.20.0"),sQuery(id+"F0.wireOp",EDGE,"E7.20.1"),sQuery(id+"F0.wireOp",EDGE,"E7.20.2"),sQuery(id+"F0.wireOp",EDGE,"E7.21.0"),sQuery(id+"F0.wireOp",EDGE,"E7.21.1"),sQuery(id+"F0.wireOp",EDGE,"E7.21.2"),sQuery(id+"F0.wireOp",EDGE,"E7.22.0"),sQuery(id+"F0.wireOp",EDGE,"E7.22.1"),sQuery(id+"F0.wireOp",EDGE,"E7.22.2"),sQuery(id+"F0.wireOp",EDGE,"E7.23.0"),sQuery(id+"F0.wireOp",EDGE,"E7.23.1"),sQuery(id+"F0.wireOp",EDGE,"E7.23.2"),sQuery(id+"F0.wireOp",EDGE,"E7.24.0"),sQuery(id+"F0.wireOp",EDGE,"E7.24.1"),sQuery(id+"F0.wireOp",EDGE,"E7.24.2"),sQuery(id+"F0.wireOp",EDGE,"E8")])],"isStart":false});
            fillet(context, id + "F8", {"entities" : qUnion([Q0, Q1]), "radius" : .5 * mm, "tangentPropagation" : true, "allowEdgeOverflow" : false});
        }
        {
            var Q0;
            Q0=makeQuery(id+"F1.opExtrude","CAP_FACE",FACE,{"disambiguationData":[OSD([sQuery(id+"F0.wireOp",EDGE,"E0"),sQuery(id+"F0.wireOp",EDGE,"E1"),sQuery(id+"F0.wireOp",EDGE,"E5"),sQuery(id+"F0.wireOp",EDGE,"E6.MirrorCS"),sQuery(id+"F0.wireOp",EDGE,"E7.1.0"),sQuery(id+"F0.wireOp",EDGE,"E7.1.1"),sQuery(id+"F0.wireOp",EDGE,"E7.1.2"),sQuery(id+"F0.wireOp",EDGE,"E7.2.0"),sQuery(id+"F0.wireOp",EDGE,"E7.2.1"),sQuery(id+"F0.wireOp",EDGE,"E7.2.2"),sQuery(id+"F0.wireOp",EDGE,"E7.3.0"),sQuery(id+"F0.wireOp",EDGE,"E7.3.1"),sQuery(id+"F0.wireOp",EDGE,"E7.3.2"),sQuery(id+"F0.wireOp",EDGE,"E7.4.0"),sQuery(id+"F0.wireOp",EDGE,"E7.4.1"),sQuery(id+"F0.wireOp",EDGE,"E7.4.2"),sQuery(id+"F0.wireOp",EDGE,"E7.5.0"),sQuery(id+"F0.wireOp",EDGE,"E7.5.1"),sQuery(id+"F0.wireOp",EDGE,"E7.5.2"),sQuery(id+"F0.wireOp",EDGE,"E7.6.0"),sQuery(id+"F0.wireOp",EDGE,"E7.6.1"),sQuery(id+"F0.wireOp",EDGE,"E7.6.2"),sQuery(id+"F0.wireOp",EDGE,"E7.7.0"),sQuery(id+"F0.wireOp",EDGE,"E7.7.1"),sQuery(id+"F0.wireOp",EDGE,"E7.7.2"),sQuery(id+"F0.wireOp",EDGE,"E7.8.0"),sQuery(id+"F0.wireOp",EDGE,"E7.8.1"),sQuery(id+"F0.wireOp",EDGE,"E7.8.2"),sQuery(id+"F0.wireOp",EDGE,"E7.9.0"),sQuery(id+"F0.wireOp",EDGE,"E7.9.1"),sQuery(id+"F0.wireOp",EDGE,"E7.9.2"),sQuery(id+"F0.wireOp",EDGE,"E7.10.0"),sQuery(id+"F0.wireOp",EDGE,"E7.10.1"),sQuery(id+"F0.wireOp",EDGE,"E7.10.2"),sQuery(id+"F0.wireOp",EDGE,"E7.11.0"),sQuery(id+"F0.wireOp",EDGE,"E7.11.1"),sQuery(id+"F0.wireOp",EDGE,"E7.11.2"),sQuery(id+"F0.wireOp",EDGE,"E7.12.0"),sQuery(id+"F0.wireOp",EDGE,"E7.12.1"),sQuery(id+"F0.wireOp",EDGE,"E7.12.2"),sQuery(id+"F0.wireOp",EDGE,"E7.13.0"),sQuery(id+"F0.wireOp",EDGE,"E7.13.1"),sQuery(id+"F0.wireOp",EDGE,"E7.13.2"),sQuery(id+"F0.wireOp",EDGE,"E7.14.0"),sQuery(id+"F0.wireOp",EDGE,"E7.14.1"),sQuery(id+"F0.wireOp",EDGE,"E7.14.2"),sQuery(id+"F0.wireOp",EDGE,"E7.15.0"),sQuery(id+"F0.wireOp",EDGE,"E7.15.1"),sQuery(id+"F0.wireOp",EDGE,"E7.15.2"),sQuery(id+"F0.wireOp",EDGE,"E7.16.0"),sQuery(id+"F0.wireOp",EDGE,"E7.16.1"),sQuery(id+"F0.wireOp",EDGE,"E7.16.2"),sQuery(id+"F0.wireOp",EDGE,"E7.17.0"),sQuery(id+"F0.wireOp",EDGE,"E7.17.1"),sQuery(id+"F0.wireOp",EDGE,"E7.17.2"),sQuery(id+"F0.wireOp",EDGE,"E7.18.0"),sQuery(id+"F0.wireOp",EDGE,"E7.18.1"),sQuery(id+"F0.wireOp",EDGE,"E7.18.2"),sQuery(id+"F0.wireOp",EDGE,"E7.19.0"),sQuery(id+"F0.wireOp",EDGE,"E7.19.1"),sQuery(id+"F0.wireOp",EDGE,"E7.19.2"),sQuery(id+"F0.wireOp",EDGE,"E7.20.0"),sQuery(id+"F0.wireOp",EDGE,"E7.20.1"),sQuery(id+"F0.wireOp",EDGE,"E7.20.2"),sQuery(id+"F0.wireOp",EDGE,"E7.21.0"),sQuery(id+"F0.wireOp",EDGE,"E7.21.1"),sQuery(id+"F0.wireOp",EDGE,"E7.21.2"),sQuery(id+"F0.wireOp",EDGE,"E7.22.0"),sQuery(id+"F0.wireOp",EDGE,"E7.22.1"),sQuery(id+"F0.wireOp",EDGE,"E7.22.2"),sQuery(id+"F0.wireOp",EDGE,"E7.23.0"),sQuery(id+"F0.wireOp",EDGE,"E7.23.1"),sQuery(id+"F0.wireOp",EDGE,"E7.23.2"),sQuery(id+"F0.wireOp",EDGE,"E7.24.0"),sQuery(id+"F0.wireOp",EDGE,"E7.24.1"),sQuery(id+"F0.wireOp",EDGE,"E7.24.2"),sQuery(id+"F0.wireOp",EDGE,"E8")])],"isStart":true});
            fillet(context, id + "F9", {"entities" : qUnion([Q0]), "radius" : .5 * mm, "tangentPropagation" : true, "allowEdgeOverflow" : false});
        }
        {
            var Q0;
            Q0=makeQuery(id+"F5.opExtrude","CAP_FACE",FACE,{"disambiguationData":[OSD([sQuery(id+"F4.wireOp",EDGE,"E11"),sQuery(id+"F4.wireOp",EDGE,"E12"),sQuery(id+"F4.wireOp",EDGE,"E13"),sQuery(id+"F4.wireOp",EDGE,"E14.MirrorCS"),sQuery(id+"F4.wireOp",EDGE,"E15.1.0"),sQuery(id+"F4.wireOp",EDGE,"E15.1.1"),sQuery(id+"F4.wireOp",EDGE,"E15.1.2"),sQuery(id+"F4.wireOp",EDGE,"E15.2.0"),sQuery(id+"F4.wireOp",EDGE,"E15.2.1"),sQuery(id+"F4.wireOp",EDGE,"E15.2.2"),sQuery(id+"F4.wireOp",EDGE,"E15.3.0"),sQuery(id+"F4.wireOp",EDGE,"E15.3.1"),sQuery(id+"F4.wireOp",EDGE,"E15.3.2"),sQuery(id+"F4.wireOp",EDGE,"E15.4.0"),sQuery(id+"F4.wireOp",EDGE,"E15.4.1"),sQuery(id+"F4.wireOp",EDGE,"E15.4.2"),sQuery(id+"F4.wireOp",EDGE,"E15.5.0"),sQuery(id+"F4.wireOp",EDGE,"E15.5.1"),sQuery(id+"F4.wireOp",EDGE,"E15.5.2"),sQuery(id+"F4.wireOp",EDGE,"E15.6.0"),sQuery(id+"F4.wireOp",EDGE,"E15.6.1"),sQuery(id+"F4.wireOp",EDGE,"E15.6.2"),sQuery(id+"F4.wireOp",EDGE,"E15.7.0"),sQuery(id+"F4.wireOp",EDGE,"E15.7.1"),sQuery(id+"F4.wireOp",EDGE,"E15.7.2"),sQuery(id+"F4.wireOp",EDGE,"E15.8.0"),sQuery(id+"F4.wireOp",EDGE,"E15.8.1"),sQuery(id+"F4.wireOp",EDGE,"E15.8.2"),sQuery(id+"F4.wireOp",EDGE,"E15.9.0"),sQuery(id+"F4.wireOp",EDGE,"E15.9.1"),sQuery(id+"F4.wireOp",EDGE,"E15.9.2"),sQuery(id+"F4.wireOp",EDGE,"E15.10.0"),sQuery(id+"F4.wireOp",EDGE,"E15.10.1"),sQuery(id+"F4.wireOp",EDGE,"E15.10.2"),sQuery(id+"F4.wireOp",EDGE,"E15.11.0"),sQuery(id+"F4.wireOp",EDGE,"E15.11.1"),sQuery(id+"F4.wireOp",EDGE,"E15.11.2"),sQuery(id+"F4.wireOp",EDGE,"E15.12.0"),sQuery(id+"F4.wireOp",EDGE,"E15.12.1"),sQuery(id+"F4.wireOp",EDGE,"E15.12.2"),sQuery(id+"F4.wireOp",EDGE,"E15.13.0"),sQuery(id+"F4.wireOp",EDGE,"E15.13.1"),sQuery(id+"F4.wireOp",EDGE,"E15.13.2"),sQuery(id+"F4.wireOp",EDGE,"E15.14.0"),sQuery(id+"F4.wireOp",EDGE,"E15.14.1"),sQuery(id+"F4.wireOp",EDGE,"E15.14.2"),sQuery(id+"F4.wireOp",EDGE,"E15.15.0"),sQuery(id+"F4.wireOp",EDGE,"E15.15.1"),sQuery(id+"F4.wireOp",EDGE,"E15.15.2"),sQuery(id+"F4.wireOp",EDGE,"E15.16.0"),sQuery(id+"F4.wireOp",EDGE,"E15.16.1"),sQuery(id+"F4.wireOp",EDGE,"E15.16.2"),sQuery(id+"F4.wireOp",EDGE,"E15.17.0"),sQuery(id+"F4.wireOp",EDGE,"E15.17.1"),sQuery(id+"F4.wireOp",EDGE,"E15.17.2"),sQuery(id+"F4.wireOp",EDGE,"E15.18.0"),sQuery(id+"F4.wireOp",EDGE,"E15.18.1"),sQuery(id+"F4.wireOp",EDGE,"E15.18.2"),sQuery(id+"F4.wireOp",EDGE,"E15.19.0"),sQuery(id+"F4.wireOp",EDGE,"E15.19.1"),sQuery(id+"F4.wireOp",EDGE,"E15.19.2"),sQuery(id+"F4.wireOp",EDGE,"E15.20.0"),sQuery(id+"F4.wireOp",EDGE,"E15.20.1"),sQuery(id+"F4.wireOp",EDGE,"E15.20.2"),sQuery(id+"F4.wireOp",EDGE,"E15.21.0"),sQuery(id+"F4.wireOp",EDGE,"E15.21.1"),sQuery(id+"F4.wireOp",EDGE,"E15.21.2"),sQuery(id+"F4.wireOp",EDGE,"E15.22.0"),sQuery(id+"F4.wireOp",EDGE,"E15.22.1"),sQuery(id+"F4.wireOp",EDGE,"E15.22.2"),sQuery(id+"F4.wireOp",EDGE,"E16")])],"isStart":true});
            fillet(context, id + "F10", {"entities" : qUnion([Q0]), "radius" : .5 * mm, "tangentPropagation" : true, "allowEdgeOverflow" : false});
        }
        {
            var Q0;
            Q0=makeQuery(id+"F7.opExtrude","CAP_FACE",FACE,{"disambiguationData":[OSD([sQuery(id+"F6.wireOp",EDGE,"E17"),sQuery(id+"F6.wireOp",EDGE,"E18")])],"isStart":false});
            var sketch = newSketch(context, id + "F11", { "sketchPlane" : qUnion([Q0])});
            skCircle(sketch, "E19", {"center": v(0, 0) * mm, "radius": 38.5 * mm});
            skLineSegment(sketch, "E20", {"start": v(-1.5, 43) * mm, "end": v(1.5, 43) * mm});
            skLineSegment(sketch, "E21", {"start": v(0, 43) * mm, "end": v(7, 43) * mm, "construction": true});
            skArc(sketch, "E22", {"start": v(1.5, 43) * mm, "mid": v(2.22, 40.28) * mm, "end": v(4.2, 38.27) * mm});
            skArc(sketch, "E23.MirrorCS", {"start": v(-1.5, 43) * mm, "mid": v(-2.22, 40.28) * mm, "end": v(-4.2, 38.27) * mm});
            skCircle(sketch, "E24", {"center": v(0, 0) * mm, "radius": 17.5 * mm});
            skArc(sketch, "E25.1.0", {"start": v(-11.24, 41.53) * mm, "mid": v(-9.75, 39.14) * mm, "end": v(-7.28, 37.8) * mm});
            skLineSegment(sketch, "E25.1.1", {"start": v(-14.1, 40.65) * mm, "end": v(-11.24, 41.53) * mm});
            skArc(sketch, "E25.1.2", {"start": v(-14.1, 40.65) * mm, "mid": v(-14, 37.84) * mm, "end": v(-15.29, 35.34) * mm});
            skArc(sketch, "E25.2.0", {"start": v(-22.98, 36.37) * mm, "mid": v(-20.86, 34.53) * mm, "end": v(-18.1, 33.98) * mm});
            skLineSegment(sketch, "E25.2.1", {"start": v(-25.46, 34.68) * mm, "end": v(-22.98, 36.37) * mm});
            skArc(sketch, "E25.2.2", {"start": v(-25.46, 34.68) * mm, "mid": v(-24.52, 32.03) * mm, "end": v(-25.02, 29.26) * mm});
            skArc(sketch, "E25.3.0", {"start": v(-32.68, 27.98) * mm, "mid": v(-30.1, 26.85) * mm, "end": v(-27.3, 27.14) * mm});
            skLineSegment(sketch, "E25.3.1", {"start": v(-34.55, 25.64) * mm, "end": v(-32.68, 27.98) * mm});
            skArc(sketch, "E25.3.2", {"start": v(-34.55, 25.64) * mm, "mid": v(-32.88, 23.38) * mm, "end": v(-32.53, 20.58) * mm});
            skArc(sketch, "E25.4.0", {"start": v(-39.48, 17.1) * mm, "mid": v(-36.68, 16.78) * mm, "end": v(-34.1, 17.88) * mm});
            skLineSegment(sketch, "E25.4.1", {"start": v(-40.58, 14.31) * mm, "end": v(-39.48, 17.1) * mm});
            skArc(sketch, "E25.4.2", {"start": v(-40.58, 14.31) * mm, "mid": v(-38.3, 12.65) * mm, "end": v(-37.16, 10.08) * mm});
            skArc(sketch, "E25.5.0", {"start": v(-42.77, 4.7) * mm, "mid": v(-40, 5.22) * mm, "end": v(-37.85, 7.04) * mm});
            skLineSegment(sketch, "E25.5.1", {"start": v(-43, 1.72) * mm, "end": v(-42.77, 4.7) * mm});
            skArc(sketch, "E25.5.2", {"start": v(-43, 1.72) * mm, "mid": v(-40.33, 0.8) * mm, "end": v(-38.48, -1.32) * mm});
            skArc(sketch, "E25.6.0", {"start": v(-42.26, -8.1) * mm, "mid": v(-39.76, -6.8) * mm, "end": v(-38.24, -4.43) * mm});
            skLineSegment(sketch, "E25.6.1", {"start": v(-41.59, -11.03) * mm, "end": v(-42.26, -8.1) * mm});
            skArc(sketch, "E25.6.2", {"start": v(-41.59, -11.03) * mm, "mid": v(-38.78, -11.13) * mm, "end": v(-36.38, -12.6) * mm});
            skArc(sketch, "E25.7.0", {"start": v(-37.99, -20.2) * mm, "mid": v(-36, -18.22) * mm, "end": v(-35.24, -15.5) * mm});
            skLineSegment(sketch, "E25.7.1", {"start": v(-36.49, -22.8) * mm, "end": v(-37.99, -20.2) * mm});
            skArc(sketch, "E25.7.2", {"start": v(-36.49, -22.8) * mm, "mid": v(-33.77, -22.06) * mm, "end": v(-31.05, -22.77) * mm});
            skArc(sketch, "E25.8.0", {"start": v(-30.35, -30.5) * mm, "mid": v(-29.02, -28.02) * mm, "end": v(-29.1, -25.2) * mm});
            skLineSegment(sketch, "E25.8.1", {"start": v(-28.15, -32.54) * mm, "end": v(-30.35, -30.5) * mm});
            skArc(sketch, "E25.8.2", {"start": v(-28.15, -32.54) * mm, "mid": v(-25.77, -31.04) * mm, "end": v(-22.96, -30.9) * mm});
            skArc(sketch, "E25.9.0", {"start": v(-20, -38.1) * mm, "mid": v(-19.48, -35.33) * mm, "end": v(-20.38, -32.66) * mm});
            skLineSegment(sketch, "E25.9.1", {"start": v(-17.3, -39.4) * mm, "end": v(-20, -38.1) * mm});
            skArc(sketch, "E25.9.2", {"start": v(-17.3, -39.4) * mm, "mid": v(-15.48, -37.25) * mm, "end": v(-12.83, -36.3) * mm});
            skArc(sketch, "E25.10.0", {"start": v(-7.9, -42.3) * mm, "mid": v(-8.2, -39.5) * mm, "end": v(-9.85, -37.22) * mm});
            skLineSegment(sketch, "E25.10.1", {"start": v(-4.93, -42.74) * mm, "end": v(-7.9, -42.3) * mm});
            skArc(sketch, "E25.10.2", {"start": v(-4.93, -42.74) * mm, "mid": v(-3.8, -40.16) * mm, "end": v(-1.56, -38.47) * mm});
            skArc(sketch, "E25.11.0", {"start": v(4.93, -42.74) * mm, "mid": v(3.8, -40.16) * mm, "end": v(1.56, -38.47) * mm});
            skLineSegment(sketch, "E25.11.1", {"start": v(7.9, -42.3) * mm, "end": v(4.93, -42.74) * mm});
            skArc(sketch, "E25.11.2", {"start": v(7.9, -42.3) * mm, "mid": v(8.2, -39.5) * mm, "end": v(9.85, -37.22) * mm});
            skArc(sketch, "E25.12.0", {"start": v(17.3, -39.4) * mm, "mid": v(15.48, -37.25) * mm, "end": v(12.83, -36.3) * mm});
            skLineSegment(sketch, "E25.12.1", {"start": v(20, -38.1) * mm, "end": v(17.3, -39.4) * mm});
            skArc(sketch, "E25.12.2", {"start": v(20, -38.1) * mm, "mid": v(19.48, -35.33) * mm, "end": v(20.38, -32.66) * mm});
            skArc(sketch, "E25.13.0", {"start": v(28.15, -32.54) * mm, "mid": v(25.77, -31.04) * mm, "end": v(22.96, -30.9) * mm});
            skLineSegment(sketch, "E25.13.1", {"start": v(30.35, -30.5) * mm, "end": v(28.15, -32.54) * mm});
            skArc(sketch, "E25.13.2", {"start": v(30.35, -30.5) * mm, "mid": v(29.02, -28.02) * mm, "end": v(29.1, -25.2) * mm});
            skArc(sketch, "E25.14.0", {"start": v(36.49, -22.8) * mm, "mid": v(33.77, -22.06) * mm, "end": v(31.05, -22.77) * mm});
            skLineSegment(sketch, "E25.14.1", {"start": v(37.99, -20.2) * mm, "end": v(36.49, -22.8) * mm});
            skArc(sketch, "E25.14.2", {"start": v(37.99, -20.2) * mm, "mid": v(36, -18.22) * mm, "end": v(35.24, -15.5) * mm});
            skArc(sketch, "E25.15.0", {"start": v(41.59, -11.03) * mm, "mid": v(38.78, -11.13) * mm, "end": v(36.38, -12.6) * mm});
            skLineSegment(sketch, "E25.15.1", {"start": v(42.26, -8.1) * mm, "end": v(41.59, -11.03) * mm});
            skArc(sketch, "E25.15.2", {"start": v(42.26, -8.1) * mm, "mid": v(39.76, -6.8) * mm, "end": v(38.24, -4.43) * mm});
            skArc(sketch, "E25.16.0", {"start": v(43, 1.72) * mm, "mid": v(40.33, 0.8) * mm, "end": v(38.48, -1.32) * mm});
            skLineSegment(sketch, "E25.16.1", {"start": v(42.77, 4.7) * mm, "end": v(43, 1.72) * mm});
            skArc(sketch, "E25.16.2", {"start": v(42.77, 4.7) * mm, "mid": v(40, 5.22) * mm, "end": v(37.85, 7.04) * mm});
            skArc(sketch, "E25.17.0", {"start": v(40.58, 14.31) * mm, "mid": v(38.3, 12.65) * mm, "end": v(37.16, 10.08) * mm});
            skLineSegment(sketch, "E25.17.1", {"start": v(39.48, 17.1) * mm, "end": v(40.58, 14.31) * mm});
            skArc(sketch, "E25.17.2", {"start": v(39.48, 17.1) * mm, "mid": v(36.68, 16.78) * mm, "end": v(34.1, 17.88) * mm});
            skArc(sketch, "E25.18.0", {"start": v(34.55, 25.64) * mm, "mid": v(32.88, 23.38) * mm, "end": v(32.53, 20.58) * mm});
            skLineSegment(sketch, "E25.18.1", {"start": v(32.68, 27.98) * mm, "end": v(34.55, 25.64) * mm});
            skArc(sketch, "E25.18.2", {"start": v(32.68, 27.98) * mm, "mid": v(30.1, 26.85) * mm, "end": v(27.3, 27.14) * mm});
            skArc(sketch, "E25.19.0", {"start": v(25.46, 34.68) * mm, "mid": v(24.52, 32.03) * mm, "end": v(25.02, 29.26) * mm});
            skLineSegment(sketch, "E25.19.1", {"start": v(22.98, 36.37) * mm, "end": v(25.46, 34.68) * mm});
            skArc(sketch, "E25.19.2", {"start": v(22.98, 36.37) * mm, "mid": v(20.86, 34.53) * mm, "end": v(18.1, 33.98) * mm});
            skArc(sketch, "E25.20.0", {"start": v(14.1, 40.65) * mm, "mid": v(14, 37.84) * mm, "end": v(15.29, 35.34) * mm});
            skLineSegment(sketch, "E25.20.1", {"start": v(11.24, 41.53) * mm, "end": v(14.1, 40.65) * mm});
            skArc(sketch, "E25.20.2", {"start": v(11.24, 41.53) * mm, "mid": v(9.75, 39.14) * mm, "end": v(7.28, 37.8) * mm});
            skSolve(sketch);
        }
        {
            var Q0;
            Q0 = qSketchRegion(id + "F11", true);
            extrude(context, id + "F12", {"entities" : qUnion([Q0]), "operationType" : NewBodyOperationType.ADD, "depth" : 1.5 * mm, "offsetDistance" : 25 * mm});
        }
        {
            var Q0;
            Q0=makeQuery(id+"F12.opExtrude","CAP_FACE",FACE,{"disambiguationData":[OSD([sQuery(id+"F11.wireOp",EDGE,"E19"),sQuery(id+"F11.wireOp",EDGE,"E20"),sQuery(id+"F11.wireOp",EDGE,"E22"),sQuery(id+"F11.wireOp",EDGE,"E23.MirrorCS"),sQuery(id+"F11.wireOp",EDGE,"E24"),sQuery(id+"F11.wireOp",EDGE,"E25.1.0"),sQuery(id+"F11.wireOp",EDGE,"E25.1.1"),sQuery(id+"F11.wireOp",EDGE,"E25.1.2"),sQuery(id+"F11.wireOp",EDGE,"E25.2.0"),sQuery(id+"F11.wireOp",EDGE,"E25.2.1"),sQuery(id+"F11.wireOp",EDGE,"E25.2.2"),sQuery(id+"F11.wireOp",EDGE,"E25.3.0"),sQuery(id+"F11.wireOp",EDGE,"E25.3.1"),sQuery(id+"F11.wireOp",EDGE,"E25.3.2"),sQuery(id+"F11.wireOp",EDGE,"E25.4.0"),sQuery(id+"F11.wireOp",EDGE,"E25.4.1"),sQuery(id+"F11.wireOp",EDGE,"E25.4.2"),sQuery(id+"F11.wireOp",EDGE,"E25.5.0"),sQuery(id+"F11.wireOp",EDGE,"E25.5.1"),sQuery(id+"F11.wireOp",EDGE,"E25.5.2"),sQuery(id+"F11.wireOp",EDGE,"E25.6.0"),sQuery(id+"F11.wireOp",EDGE,"E25.6.1"),sQuery(id+"F11.wireOp",EDGE,"E25.6.2"),sQuery(id+"F11.wireOp",EDGE,"E25.7.0"),sQuery(id+"F11.wireOp",EDGE,"E25.7.1"),sQuery(id+"F11.wireOp",EDGE,"E25.7.2"),sQuery(id+"F11.wireOp",EDGE,"E25.8.0"),sQuery(id+"F11.wireOp",EDGE,"E25.8.1"),sQuery(id+"F11.wireOp",EDGE,"E25.8.2"),sQuery(id+"F11.wireOp",EDGE,"E25.9.0"),sQuery(id+"F11.wireOp",EDGE,"E25.9.1"),sQuery(id+"F11.wireOp",EDGE,"E25.9.2"),sQuery(id+"F11.wireOp",EDGE,"E25.10.0"),sQuery(id+"F11.wireOp",EDGE,"E25.10.1"),sQuery(id+"F11.wireOp",EDGE,"E25.10.2"),sQuery(id+"F11.wireOp",EDGE,"E25.11.0"),sQuery(id+"F11.wireOp",EDGE,"E25.11.1"),sQuery(id+"F11.wireOp",EDGE,"E25.11.2"),sQuery(id+"F11.wireOp",EDGE,"E25.12.0"),sQuery(id+"F11.wireOp",EDGE,"E25.12.1"),sQuery(id+"F11.wireOp",EDGE,"E25.12.2"),sQuery(id+"F11.wireOp",EDGE,"E25.13.0"),sQuery(id+"F11.wireOp",EDGE,"E25.13.1"),sQuery(id+"F11.wireOp",EDGE,"E25.13.2"),sQuery(id+"F11.wireOp",EDGE,"E25.14.0"),sQuery(id+"F11.wireOp",EDGE,"E25.14.1"),sQuery(id+"F11.wireOp",EDGE,"E25.14.2"),sQuery(id+"F11.wireOp",EDGE,"E25.15.0"),sQuery(id+"F11.wireOp",EDGE,"E25.15.1"),sQuery(id+"F11.wireOp",EDGE,"E25.15.2"),sQuery(id+"F11.wireOp",EDGE,"E25.16.0"),sQuery(id+"F11.wireOp",EDGE,"E25.16.1"),sQuery(id+"F11.wireOp",EDGE,"E25.16.2"),sQuery(id+"F11.wireOp",EDGE,"E25.17.0"),sQuery(id+"F11.wireOp",EDGE,"E25.17.1"),sQuery(id+"F11.wireOp",EDGE,"E25.17.2"),sQuery(id+"F11.wireOp",EDGE,"E25.18.0"),sQuery(id+"F11.wireOp",EDGE,"E25.18.1"),sQuery(id+"F11.wireOp",EDGE,"E25.18.2"),sQuery(id+"F11.wireOp",EDGE,"E25.19.0"),sQuery(id+"F11.wireOp",EDGE,"E25.19.1"),sQuery(id+"F11.wireOp",EDGE,"E25.19.2"),sQuery(id+"F11.wireOp",EDGE,"E25.20.0"),sQuery(id+"F11.wireOp",EDGE,"E25.20.1"),sQuery(id+"F11.wireOp",EDGE,"E25.20.2")])],"isStart":false});
            var sketch = newSketch(context, id + "F13", { "sketchPlane" : qUnion([Q0])});
            skCircle(sketch, "E26", {"center": v(0, 0) * mm, "radius": 20.5 * mm});
            skCircle(sketch, "E27", {"center": v(0, 0) * mm, "radius": 17.5 * mm});
            skSolve(sketch);
        }
        {
            var Q0;
            Q0 = qSketchRegion(id + "F13", true);
            extrude(context, id + "F14", {"entities" : qUnion([Q0]), "operationType" : NewBodyOperationType.ADD, "depth" : 2.5 * mm, "offsetDistance" : 25 * mm});
        }
        {
            var Q0;
            Q0=makeQuery(id+"F14.opExtrude","CAP_FACE",FACE,{"disambiguationData":[OSD([sQuery(id+"F13.wireOp",EDGE,"E26"),sQuery(id+"F13.wireOp",EDGE,"E27")])],"isStart":false});
            var sketch = newSketch(context, id + "F15", { "sketchPlane" : qUnion([Q0])});
            skCircle(sketch, "E28", {"center": v(0, 0) * mm, "radius": 34 * mm});
            skLineSegment(sketch, "E29", {"start": v(-1.5, 38.5) * mm, "end": v(1.5, 38.5) * mm});
            skLineSegment(sketch, "E30", {"start": v(0, 38.5) * mm, "end": v(5.43, 38.5) * mm});
            skArc(sketch, "E31", {"start": v(1.5, 38.5) * mm, "mid": v(2.24, 35.75) * mm, "end": v(4.26, 33.73) * mm});
            skArc(sketch, "E32.MirrorCS", {"start": v(-1.5, 38.5) * mm, "mid": v(-2.24, 35.75) * mm, "end": v(-4.26, 33.73) * mm});
            skArc(sketch, "E33.1.0", {"start": v(-11.08, 36.9) * mm, "mid": v(-9.49, 34.54) * mm, "end": v(-6.93, 33.29) * mm});
            skLineSegment(sketch, "E33.1.1", {"start": v(-13.92, 35.93) * mm, "end": v(-11.08, 36.9) * mm});
            skArc(sketch, "E33.1.2", {"start": v(-13.92, 35.93) * mm, "mid": v(-13.72, 33.08) * mm, "end": v(-14.98, 30.52) * mm});
            skArc(sketch, "E33.2.0", {"start": v(-22.46, 31.3) * mm, "mid": v(-20.19, 29.58) * mm, "end": v(-17.36, 29.23) * mm});
            skLineSegment(sketch, "E33.2.1", {"start": v(-24.83, 29.46) * mm, "end": v(-22.46, 31.3) * mm});
            skArc(sketch, "E33.2.2", {"start": v(-24.83, 29.46) * mm, "mid": v(-23.72, 26.83) * mm, "end": v(-24.08, 24) * mm});
            skArc(sketch, "E33.3.0", {"start": v(-31.41, 22.31) * mm, "mid": v(-28.7, 21.43) * mm, "end": v(-25.91, 22.01) * mm});
            skLineSegment(sketch, "E33.3.1", {"start": v(-33.05, 19.8) * mm, "end": v(-31.41, 22.31) * mm});
            skArc(sketch, "E33.3.2", {"start": v(-33.05, 19.8) * mm, "mid": v(-31.15, 17.68) * mm, "end": v(-30.57, 14.89) * mm});
            skArc(sketch, "E33.4.0", {"start": v(-36.95, 10.9) * mm, "mid": v(-34.1, 10.95) * mm, "end": v(-31.65, 12.4) * mm});
            skLineSegment(sketch, "E33.4.1", {"start": v(-37.7, 8) * mm, "end": v(-36.95, 10.9) * mm});
            skArc(sketch, "E33.4.2", {"start": v(-37.7, 8) * mm, "mid": v(-35.2, 6.6) * mm, "end": v(-33.75, 4.15) * mm});
            skArc(sketch, "E33.5.0", {"start": v(-38.5, -1.68) * mm, "mid": v(-35.8, -0.72) * mm, "end": v(-33.97, 1.46) * mm});
            skLineSegment(sketch, "E33.5.1", {"start": v(-38.24, -4.67) * mm, "end": v(-38.5, -1.68) * mm});
            skArc(sketch, "E33.5.2", {"start": v(-38.24, -4.67) * mm, "mid": v(-35.44, -5.18) * mm, "end": v(-33.27, -7.03) * mm});
            skArc(sketch, "E33.6.0", {"start": v(-35.86, -14.1) * mm, "mid": v(-33.63, -12.3) * mm, "end": v(-32.6, -9.65) * mm});
            skLineSegment(sketch, "E33.6.1", {"start": v(-34.65, -16.84) * mm, "end": v(-35.86, -14.1) * mm});
            skArc(sketch, "E33.6.2", {"start": v(-34.65, -16.84) * mm, "mid": v(-31.84, -16.4) * mm, "end": v(-29.18, -17.45) * mm});
            skArc(sketch, "E33.7.0", {"start": v(-29.34, -24.97) * mm, "mid": v(-27.82, -22.56) * mm, "end": v(-27.7, -19.71) * mm});
            skLineSegment(sketch, "E33.7.1", {"start": v(-27.3, -27.18) * mm, "end": v(-29.34, -24.97) * mm});
            skArc(sketch, "E33.7.2", {"start": v(-27.3, -27.18) * mm, "mid": v(-24.78, -25.86) * mm, "end": v(-21.93, -25.98) * mm});
            skArc(sketch, "E33.8.0", {"start": v(-19.64, -33.15) * mm, "mid": v(-18.98, -30.37) * mm, "end": v(-19.8, -27.64) * mm});
            skLineSegment(sketch, "E33.8.1", {"start": v(-17, -34.57) * mm, "end": v(-19.64, -33.15) * mm});
            skArc(sketch, "E33.8.2", {"start": v(-17, -34.57) * mm, "mid": v(-15.04, -32.5) * mm, "end": v(-12.31, -31.7) * mm});
            skArc(sketch, "E33.9.0", {"start": v(-7.82, -37.73) * mm, "mid": v(-8.1, -34.9) * mm, "end": v(-9.75, -32.57) * mm});
            skLineSegment(sketch, "E33.9.1", {"start": v(-4.86, -38.22) * mm, "end": v(-7.82, -37.73) * mm});
            skArc(sketch, "E33.9.2", {"start": v(-4.86, -38.22) * mm, "mid": v(-3.68, -35.63) * mm, "end": v(-1.35, -33.97) * mm});
            skArc(sketch, "E33.10.0", {"start": v(4.86, -38.22) * mm, "mid": v(3.68, -35.63) * mm, "end": v(1.35, -33.97) * mm});
            skLineSegment(sketch, "E33.10.1", {"start": v(7.82, -37.73) * mm, "end": v(4.86, -38.22) * mm});
            skArc(sketch, "E33.10.2", {"start": v(7.82, -37.73) * mm, "mid": v(8.1, -34.9) * mm, "end": v(9.75, -32.57) * mm});
            skArc(sketch, "E33.11.0", {"start": v(17, -34.57) * mm, "mid": v(15.04, -32.5) * mm, "end": v(12.31, -31.7) * mm});
            skLineSegment(sketch, "E33.11.1", {"start": v(19.64, -33.15) * mm, "end": v(17, -34.57) * mm});
            skArc(sketch, "E33.11.2", {"start": v(19.64, -33.15) * mm, "mid": v(18.98, -30.37) * mm, "end": v(19.8, -27.64) * mm});
            skArc(sketch, "E33.12.0", {"start": v(27.3, -27.18) * mm, "mid": v(24.78, -25.86) * mm, "end": v(21.93, -25.98) * mm});
            skLineSegment(sketch, "E33.12.1", {"start": v(29.34, -24.97) * mm, "end": v(27.3, -27.18) * mm});
            skArc(sketch, "E33.12.2", {"start": v(29.34, -24.97) * mm, "mid": v(27.82, -22.56) * mm, "end": v(27.7, -19.71) * mm});
            skArc(sketch, "E33.13.0", {"start": v(34.65, -16.84) * mm, "mid": v(31.84, -16.4) * mm, "end": v(29.18, -17.45) * mm});
            skLineSegment(sketch, "E33.13.1", {"start": v(35.86, -14.1) * mm, "end": v(34.65, -16.84) * mm});
            skArc(sketch, "E33.13.2", {"start": v(35.86, -14.1) * mm, "mid": v(33.63, -12.3) * mm, "end": v(32.6, -9.65) * mm});
            skArc(sketch, "E33.14.0", {"start": v(38.24, -4.67) * mm, "mid": v(35.44, -5.18) * mm, "end": v(33.27, -7.03) * mm});
            skLineSegment(sketch, "E33.14.1", {"start": v(38.5, -1.68) * mm, "end": v(38.24, -4.67) * mm});
            skArc(sketch, "E33.14.2", {"start": v(38.5, -1.68) * mm, "mid": v(35.8, -0.72) * mm, "end": v(33.97, 1.46) * mm});
            skArc(sketch, "E33.15.0", {"start": v(37.7, 8) * mm, "mid": v(35.2, 6.6) * mm, "end": v(33.75, 4.15) * mm});
            skLineSegment(sketch, "E33.15.1", {"start": v(36.95, 10.9) * mm, "end": v(37.7, 8) * mm});
            skArc(sketch, "E33.15.2", {"start": v(36.95, 10.9) * mm, "mid": v(34.1, 10.95) * mm, "end": v(31.65, 12.4) * mm});
            skArc(sketch, "E33.16.0", {"start": v(33.05, 19.8) * mm, "mid": v(31.15, 17.68) * mm, "end": v(30.57, 14.89) * mm});
            skLineSegment(sketch, "E33.16.1", {"start": v(31.41, 22.31) * mm, "end": v(33.05, 19.8) * mm});
            skArc(sketch, "E33.16.2", {"start": v(31.41, 22.31) * mm, "mid": v(28.7, 21.43) * mm, "end": v(25.91, 22.01) * mm});
            skArc(sketch, "E33.17.0", {"start": v(24.83, 29.46) * mm, "mid": v(23.72, 26.83) * mm, "end": v(24.08, 24) * mm});
            skLineSegment(sketch, "E33.17.1", {"start": v(22.46, 31.3) * mm, "end": v(24.83, 29.46) * mm});
            skArc(sketch, "E33.17.2", {"start": v(22.46, 31.3) * mm, "mid": v(20.19, 29.58) * mm, "end": v(17.36, 29.23) * mm});
            skArc(sketch, "E33.18.0", {"start": v(13.92, 35.93) * mm, "mid": v(13.72, 33.08) * mm, "end": v(14.98, 30.52) * mm});
            skLineSegment(sketch, "E33.18.1", {"start": v(11.08, 36.9) * mm, "end": v(13.92, 35.93) * mm});
            skArc(sketch, "E33.18.2", {"start": v(11.08, 36.9) * mm, "mid": v(9.49, 34.54) * mm, "end": v(6.93, 33.29) * mm});
            skCircle(sketch, "E34", {"center": v(0, 0) * mm, "radius": 17.5 * mm});
            skSolve(sketch);
        }
        {
            var Q0;
            Q0 = qSketchRegion(id + "F15", true);
            extrude(context, id + "F16", {"entities" : qUnion([Q0]), "operationType" : NewBodyOperationType.ADD, "depth" : 1.5 * mm, "offsetDistance" : 25 * mm});
        }
        {
            var Q0;
            Q0=makeQuery(id+"F16.opExtrude","CAP_FACE",FACE,{"disambiguationData":[OSD([sQuery(id+"F15.wireOp",EDGE,"E28"),sQuery(id+"F15.wireOp",EDGE,"E29"),sQuery(id+"F15.wireOp",EDGE,"E30"),sQuery(id+"F15.wireOp",EDGE,"E32.MirrorCS"),sQuery(id+"F15.wireOp",EDGE,"E31"),sQuery(id+"F15.wireOp",EDGE,"E33.1.0"),sQuery(id+"F15.wireOp",EDGE,"E33.1.1"),sQuery(id+"F15.wireOp",EDGE,"E33.1.2"),sQuery(id+"F15.wireOp",EDGE,"E33.2.0"),sQuery(id+"F15.wireOp",EDGE,"E33.2.1"),sQuery(id+"F15.wireOp",EDGE,"E33.2.2"),sQuery(id+"F15.wireOp",EDGE,"E33.3.0"),sQuery(id+"F15.wireOp",EDGE,"E33.3.1"),sQuery(id+"F15.wireOp",EDGE,"E33.3.2"),sQuery(id+"F15.wireOp",EDGE,"E33.4.0"),sQuery(id+"F15.wireOp",EDGE,"E33.4.1"),sQuery(id+"F15.wireOp",EDGE,"E33.4.2"),sQuery(id+"F15.wireOp",EDGE,"E33.5.0"),sQuery(id+"F15.wireOp",EDGE,"E33.5.1"),sQuery(id+"F15.wireOp",EDGE,"E33.5.2"),sQuery(id+"F15.wireOp",EDGE,"E33.6.0"),sQuery(id+"F15.wireOp",EDGE,"E33.6.1"),sQuery(id+"F15.wireOp",EDGE,"E33.6.2"),sQuery(id+"F15.wireOp",EDGE,"E33.7.0"),sQuery(id+"F15.wireOp",EDGE,"E33.7.1"),sQuery(id+"F15.wireOp",EDGE,"E33.7.2"),sQuery(id+"F15.wireOp",EDGE,"E33.8.0"),sQuery(id+"F15.wireOp",EDGE,"E33.8.1"),sQuery(id+"F15.wireOp",EDGE,"E33.8.2"),sQuery(id+"F15.wireOp",EDGE,"E33.9.0"),sQuery(id+"F15.wireOp",EDGE,"E33.9.1"),sQuery(id+"F15.wireOp",EDGE,"E33.9.2"),sQuery(id+"F15.wireOp",EDGE,"E33.10.0"),sQuery(id+"F15.wireOp",EDGE,"E33.10.1"),sQuery(id+"F15.wireOp",EDGE,"E33.10.2"),sQuery(id+"F15.wireOp",EDGE,"E33.11.0"),sQuery(id+"F15.wireOp",EDGE,"E33.11.1"),sQuery(id+"F15.wireOp",EDGE,"E33.11.2"),sQuery(id+"F15.wireOp",EDGE,"E33.12.0"),sQuery(id+"F15.wireOp",EDGE,"E33.12.1"),sQuery(id+"F15.wireOp",EDGE,"E33.12.2"),sQuery(id+"F15.wireOp",EDGE,"E33.13.0"),sQuery(id+"F15.wireOp",EDGE,"E33.13.1"),sQuery(id+"F15.wireOp",EDGE,"E33.13.2"),sQuery(id+"F15.wireOp",EDGE,"E33.14.0"),sQuery(id+"F15.wireOp",EDGE,"E33.14.1"),sQuery(id+"F15.wireOp",EDGE,"E33.14.2"),sQuery(id+"F15.wireOp",EDGE,"E33.15.0"),sQuery(id+"F15.wireOp",EDGE,"E33.15.1"),sQuery(id+"F15.wireOp",EDGE,"E33.15.2"),sQuery(id+"F15.wireOp",EDGE,"E33.16.0"),sQuery(id+"F15.wireOp",EDGE,"E33.16.1"),sQuery(id+"F15.wireOp",EDGE,"E33.16.2"),sQuery(id+"F15.wireOp",EDGE,"E33.17.0"),sQuery(id+"F15.wireOp",EDGE,"E33.17.1"),sQuery(id+"F15.wireOp",EDGE,"E33.17.2"),sQuery(id+"F15.wireOp",EDGE,"E33.18.0"),sQuery(id+"F15.wireOp",EDGE,"E33.18.1"),sQuery(id+"F15.wireOp",EDGE,"E33.18.2"),sQuery(id+"F15.wireOp",EDGE,"E34")])],"isStart":false});
            var sketch = newSketch(context, id + "F17", { "sketchPlane" : qUnion([Q0])});
            skCircle(sketch, "E35", {"center": v(0, 0) * mm, "radius": 17.5 * mm});
            skCircle(sketch, "E36", {"center": v(0, 0) * mm, "radius": 20.5 * mm});
            skSolve(sketch);
        }
        {
            var Q0;
            Q0 = qSketchRegion(id + "F17", true);
            extrude(context, id + "F18", {"entities" : qUnion([Q0]), "operationType" : NewBodyOperationType.ADD, "depth" : 2.5 * mm, "offsetDistance" : 25 * mm});
        }
        {
            var Q0;
            Q0=makeQuery(id+"F18.opExtrude","CAP_FACE",FACE,{"disambiguationData":[OSD([sQuery(id+"F17.wireOp",EDGE,"E35"),sQuery(id+"F17.wireOp",EDGE,"E36")])],"isStart":false});
            var sketch = newSketch(context, id + "F19", { "sketchPlane" : qUnion([Q0])});
            skCircle(sketch, "E37", {"center": v(0, 0) * mm, "radius": 30 * mm});
            skLineSegment(sketch, "E38", {"start": v(-1.5, 33.5) * mm, "end": v(1.5, 33.5) * mm});
            skLineSegment(sketch, "E39", {"start": v(1.5, 33.5) * mm, "end": v(7.93, 33.5) * mm, "construction": true});
            skArc(sketch, "E40", {"start": v(1.5, 33.5) * mm, "mid": v(2.01, 31.41) * mm, "end": v(3.43, 29.8) * mm});
            skArc(sketch, "E41.MirrorCS", {"start": v(-1.5, 33.5) * mm, "mid": v(-2.01, 31.41) * mm, "end": v(-3.43, 29.8) * mm});
            skLineSegment(sketch, "E42.1.0", {"start": v(-13.5, 30.7) * mm, "end": v(-10.7, 31.78) * mm});
            skArc(sketch, "E42.1.1", {"start": v(-10.7, 31.78) * mm, "mid": v(-9.47, 30.02) * mm, "end": v(-7.56, 29.03) * mm});
            skArc(sketch, "E42.1.2", {"start": v(-13.5, 30.7) * mm, "mid": v(-13.22, 28.57) * mm, "end": v(-13.97, 26.55) * mm});
            skLineSegment(sketch, "E42.2.0", {"start": v(-23.68, 23.75) * mm, "end": v(-21.46, 25.77) * mm});
            skArc(sketch, "E42.2.1", {"start": v(-21.46, 25.77) * mm, "mid": v(-19.68, 24.57) * mm, "end": v(-17.54, 24.34) * mm});
            skArc(sketch, "E42.2.2", {"start": v(-23.68, 23.75) * mm, "mid": v(-22.65, 21.86) * mm, "end": v(-22.62, 19.71) * mm});
            skLineSegment(sketch, "E42.3.0", {"start": v(-30.66, 13.59) * mm, "end": v(-29.32, 16.27) * mm});
            skArc(sketch, "E42.3.1", {"start": v(-29.32, 16.27) * mm, "mid": v(-27.22, 15.8) * mm, "end": v(-25.15, 16.36) * mm});
            skArc(sketch, "E42.3.2", {"start": v(-30.66, 13.59) * mm, "mid": v(-29.02, 12.2) * mm, "end": v(-28.2, 10.2) * mm});
            skLineSegment(sketch, "E42.4.0", {"start": v(-33.5, 1.6) * mm, "end": v(-33.22, 4.58) * mm});
            skArc(sketch, "E42.4.1", {"start": v(-33.22, 4.58) * mm, "mid": v(-31.1, 4.9) * mm, "end": v(-29.36, 6.17) * mm});
            skArc(sketch, "E42.4.2", {"start": v(-33.5, 1.6) * mm, "mid": v(-31.47, 0.9) * mm, "end": v(-30, -0.67) * mm});
            skLineSegment(sketch, "E42.5.0", {"start": v(-31.81, -10.61) * mm, "end": v(-32.63, -7.72) * mm});
            skArc(sketch, "E42.5.1", {"start": v(-32.63, -7.72) * mm, "mid": v(-30.77, -6.66) * mm, "end": v(-29.6, -4.85) * mm});
            skArc(sketch, "E42.5.2", {"start": v(-31.81, -10.61) * mm, "mid": v(-29.66, -10.53) * mm, "end": v(-27.73, -11.46) * mm});
            skLineSegment(sketch, "E42.6.0", {"start": v(-25.83, -21.39) * mm, "end": v(-27.64, -19) * mm});
            skArc(sketch, "E42.6.1", {"start": v(-27.64, -19) * mm, "mid": v(-26.28, -17.32) * mm, "end": v(-25.85, -15.22) * mm});
            skArc(sketch, "E42.6.2", {"start": v(-25.83, -21.39) * mm, "mid": v(-23.86, -20.54) * mm, "end": v(-21.71, -20.7) * mm});
            skLineSegment(sketch, "E42.7.0", {"start": v(-16.36, -29.27) * mm, "end": v(-18.91, -27.7) * mm});
            skArc(sketch, "E42.7.1", {"start": v(-18.91, -27.7) * mm, "mid": v(-18.25, -25.65) * mm, "end": v(-18.6, -23.53) * mm});
            skArc(sketch, "E42.7.2", {"start": v(-16.36, -29.27) * mm, "mid": v(-14.83, -27.77) * mm, "end": v(-12.77, -27.15) * mm});
            skLineSegment(sketch, "E42.8.0", {"start": v(-4.68, -33.2) * mm, "end": v(-7.63, -32.65) * mm});
            skArc(sketch, "E42.8.1", {"start": v(-7.63, -32.65) * mm, "mid": v(-7.75, -30.5) * mm, "end": v(-8.85, -28.66) * mm});
            skArc(sketch, "E42.8.2", {"start": v(-4.68, -33.2) * mm, "mid": v(-3.8, -31.25) * mm, "end": v(-2.1, -29.93) * mm});
            skLineSegment(sketch, "E42.9.0", {"start": v(7.63, -32.65) * mm, "end": v(4.68, -33.2) * mm});
            skArc(sketch, "E42.9.1", {"start": v(4.68, -33.2) * mm, "mid": v(3.8, -31.25) * mm, "end": v(2.1, -29.93) * mm});
            skArc(sketch, "E42.9.2", {"start": v(7.63, -32.65) * mm, "mid": v(7.75, -30.5) * mm, "end": v(8.85, -28.66) * mm});
            skLineSegment(sketch, "E42.10.0", {"start": v(18.91, -27.7) * mm, "end": v(16.36, -29.27) * mm});
            skArc(sketch, "E42.10.1", {"start": v(16.36, -29.27) * mm, "mid": v(14.83, -27.77) * mm, "end": v(12.77, -27.15) * mm});
            skArc(sketch, "E42.10.2", {"start": v(18.91, -27.7) * mm, "mid": v(18.25, -25.65) * mm, "end": v(18.6, -23.53) * mm});
            skLineSegment(sketch, "E42.11.0", {"start": v(27.64, -19) * mm, "end": v(25.83, -21.39) * mm});
            skArc(sketch, "E42.11.1", {"start": v(25.83, -21.39) * mm, "mid": v(23.86, -20.54) * mm, "end": v(21.71, -20.7) * mm});
            skArc(sketch, "E42.11.2", {"start": v(27.64, -19) * mm, "mid": v(26.28, -17.32) * mm, "end": v(25.85, -15.22) * mm});
            skLineSegment(sketch, "E42.12.0", {"start": v(32.63, -7.72) * mm, "end": v(31.81, -10.61) * mm});
            skArc(sketch, "E42.12.1", {"start": v(31.81, -10.61) * mm, "mid": v(29.66, -10.53) * mm, "end": v(27.73, -11.46) * mm});
            skArc(sketch, "E42.12.2", {"start": v(32.63, -7.72) * mm, "mid": v(30.77, -6.66) * mm, "end": v(29.6, -4.85) * mm});
            skLineSegment(sketch, "E42.13.0", {"start": v(33.22, 4.58) * mm, "end": v(33.5, 1.6) * mm});
            skArc(sketch, "E42.13.1", {"start": v(33.5, 1.6) * mm, "mid": v(31.47, 0.9) * mm, "end": v(30, -0.67) * mm});
            skArc(sketch, "E42.13.2", {"start": v(33.22, 4.58) * mm, "mid": v(31.1, 4.9) * mm, "end": v(29.36, 6.17) * mm});
            skLineSegment(sketch, "E42.14.0", {"start": v(29.32, 16.27) * mm, "end": v(30.66, 13.59) * mm});
            skArc(sketch, "E42.14.1", {"start": v(30.66, 13.59) * mm, "mid": v(29.02, 12.2) * mm, "end": v(28.2, 10.2) * mm});
            skArc(sketch, "E42.14.2", {"start": v(29.32, 16.27) * mm, "mid": v(27.22, 15.8) * mm, "end": v(25.15, 16.36) * mm});
            skLineSegment(sketch, "E42.15.0", {"start": v(21.46, 25.77) * mm, "end": v(23.68, 23.75) * mm});
            skArc(sketch, "E42.15.1", {"start": v(23.68, 23.75) * mm, "mid": v(22.65, 21.86) * mm, "end": v(22.62, 19.71) * mm});
            skArc(sketch, "E42.15.2", {"start": v(21.46, 25.77) * mm, "mid": v(19.68, 24.57) * mm, "end": v(17.54, 24.34) * mm});
            skLineSegment(sketch, "E42.16.0", {"start": v(10.7, 31.78) * mm, "end": v(13.5, 30.7) * mm});
            skArc(sketch, "E42.16.1", {"start": v(13.5, 30.7) * mm, "mid": v(13.22, 28.57) * mm, "end": v(13.97, 26.55) * mm});
            skArc(sketch, "E42.16.2", {"start": v(10.7, 31.78) * mm, "mid": v(9.47, 30.02) * mm, "end": v(7.56, 29.03) * mm});
            skCircle(sketch, "E43", {"center": v(0, 0) * mm, "radius": 17.5 * mm});
            skSolve(sketch);
        }
        {
            var Q0;
            Q0 = qSketchRegion(id + "F19", true);
            extrude(context, id + "F20", {"entities" : qUnion([Q0]), "operationType" : NewBodyOperationType.ADD, "depth" : 1.5 * mm, "offsetDistance" : 25 * mm});
        }
        {
            var Q0;
            Q0=makeQuery(id+"F20.opExtrude","CAP_FACE",FACE,{"disambiguationData":[OSD([sQuery(id+"F19.wireOp",EDGE,"E37"),sQuery(id+"F19.wireOp",EDGE,"E38"),sQuery(id+"F19.wireOp",EDGE,"E40"),sQuery(id+"F19.wireOp",EDGE,"E41.MirrorCS"),sQuery(id+"F19.wireOp",EDGE,"E42.1.0"),sQuery(id+"F19.wireOp",EDGE,"E42.1.1"),sQuery(id+"F19.wireOp",EDGE,"E42.1.2"),sQuery(id+"F19.wireOp",EDGE,"E42.2.0"),sQuery(id+"F19.wireOp",EDGE,"E42.2.1"),sQuery(id+"F19.wireOp",EDGE,"E42.2.2"),sQuery(id+"F19.wireOp",EDGE,"E42.3.0"),sQuery(id+"F19.wireOp",EDGE,"E42.3.1"),sQuery(id+"F19.wireOp",EDGE,"E42.3.2"),sQuery(id+"F19.wireOp",EDGE,"E42.4.0"),sQuery(id+"F19.wireOp",EDGE,"E42.4.1"),sQuery(id+"F19.wireOp",EDGE,"E42.4.2"),sQuery(id+"F19.wireOp",EDGE,"E42.5.0"),sQuery(id+"F19.wireOp",EDGE,"E42.5.1"),sQuery(id+"F19.wireOp",EDGE,"E42.5.2"),sQuery(id+"F19.wireOp",EDGE,"E42.6.0"),sQuery(id+"F19.wireOp",EDGE,"E42.6.1"),sQuery(id+"F19.wireOp",EDGE,"E42.6.2"),sQuery(id+"F19.wireOp",EDGE,"E42.7.0"),sQuery(id+"F19.wireOp",EDGE,"E42.7.1"),sQuery(id+"F19.wireOp",EDGE,"E42.7.2"),sQuery(id+"F19.wireOp",EDGE,"E42.8.0"),sQuery(id+"F19.wireOp",EDGE,"E42.8.1"),sQuery(id+"F19.wireOp",EDGE,"E42.8.2"),sQuery(id+"F19.wireOp",EDGE,"E42.9.0"),sQuery(id+"F19.wireOp",EDGE,"E42.9.1"),sQuery(id+"F19.wireOp",EDGE,"E42.9.2"),sQuery(id+"F19.wireOp",EDGE,"E42.10.0"),sQuery(id+"F19.wireOp",EDGE,"E42.10.1"),sQuery(id+"F19.wireOp",EDGE,"E42.10.2"),sQuery(id+"F19.wireOp",EDGE,"E42.11.0"),sQuery(id+"F19.wireOp",EDGE,"E42.11.1"),sQuery(id+"F19.wireOp",EDGE,"E42.11.2"),sQuery(id+"F19.wireOp",EDGE,"E42.12.0"),sQuery(id+"F19.wireOp",EDGE,"E42.12.1"),sQuery(id+"F19.wireOp",EDGE,"E42.12.2"),sQuery(id+"F19.wireOp",EDGE,"E42.13.0"),sQuery(id+"F19.wireOp",EDGE,"E42.13.1"),sQuery(id+"F19.wireOp",EDGE,"E42.13.2"),sQuery(id+"F19.wireOp",EDGE,"E42.14.0"),sQuery(id+"F19.wireOp",EDGE,"E42.14.1"),sQuery(id+"F19.wireOp",EDGE,"E42.14.2"),sQuery(id+"F19.wireOp",EDGE,"E42.15.0"),sQuery(id+"F19.wireOp",EDGE,"E42.15.1"),sQuery(id+"F19.wireOp",EDGE,"E42.15.2"),sQuery(id+"F19.wireOp",EDGE,"E42.16.0"),sQuery(id+"F19.wireOp",EDGE,"E42.16.1"),sQuery(id+"F19.wireOp",EDGE,"E42.16.2"),sQuery(id+"F19.wireOp",EDGE,"E43")])],"isStart":false});
            var sketch = newSketch(context, id + "F21", { "sketchPlane" : qUnion([Q0])});
            skCircle(sketch, "E44", {"center": v(0, 0) * mm, "radius": 17.5 * mm});
            skCircle(sketch, "E45", {"center": v(0, 0) * mm, "radius": 20.5 * mm});
            skSolve(sketch);
        }
        {
            var Q0;
            Q0 = qSketchRegion(id + "F21", true);
            extrude(context, id + "F22", {"entities" : qUnion([Q0]), "operationType" : NewBodyOperationType.ADD, "depth" : 2.5 * mm, "offsetDistance" : 25 * mm});
        }
        {
            var Q0;
            Q0=makeQuery(id+"F22.opExtrude","CAP_FACE",FACE,{"disambiguationData":[OSD([sQuery(id+"F21.wireOp",EDGE,"E44"),sQuery(id+"F21.wireOp",EDGE,"E45")])],"isStart":false});
            var sketch = newSketch(context, id + "F23", { "sketchPlane" : qUnion([Q0])});
            skCircle(sketch, "E46", {"center": v(0, 0) * mm, "radius": 26 * mm});
            skLineSegment(sketch, "E47", {"start": v(-1.5, 29.5) * mm, "end": v(1.5, 29.5) * mm});
            skLineSegment(sketch, "E48", {"start": v(1.5, 29.5) * mm, "end": v(7.1, 29.5) * mm, "construction": true});
            skArc(sketch, "E49", {"start": v(1.5, 29.5) * mm, "mid": v(2.03, 27.38) * mm, "end": v(3.5, 25.76) * mm});
            skArc(sketch, "E50.MirrorCS", {"start": v(-1.5, 29.5) * mm, "mid": v(-2.03, 27.38) * mm, "end": v(-3.5, 25.76) * mm});
            skLineSegment(sketch, "E51.MirrorCS", {"start": v(1.5, 29.5) * mm, "end": v(-1.5, 29.5) * mm});
            skArc(sketch, "E52.1.0", {"start": v(-10.63, 27.56) * mm, "mid": v(-9.28, 25.84) * mm, "end": v(-7.3, 24.96) * mm});
            skArc(sketch, "E52.1.1", {"start": v(-13.37, 26.34) * mm, "mid": v(-13, 24.2) * mm, "end": v(-13.67, 22.12) * mm});
            skLineSegment(sketch, "E52.1.2", {"start": v(-13.37, 26.34) * mm, "end": v(-10.63, 27.56) * mm});
            skArc(sketch, "E52.2.0", {"start": v(-20.92, 20.85) * mm, "mid": v(-19, 19.83) * mm, "end": v(-16.81, 19.83) * mm});
            skArc(sketch, "E52.2.1", {"start": v(-22.93, 18.62) * mm, "mid": v(-21.7, 16.82) * mm, "end": v(-21.48, 14.65) * mm});
            skLineSegment(sketch, "E52.2.2", {"start": v(-22.93, 18.62) * mm, "end": v(-20.92, 20.85) * mm});
            skArc(sketch, "E52.3.0", {"start": v(-27.6, 10.54) * mm, "mid": v(-25.42, 10.4) * mm, "end": v(-23.42, 11.28) * mm});
            skArc(sketch, "E52.3.1", {"start": v(-28.52, 7.69) * mm, "mid": v(-26.67, 6.53) * mm, "end": v(-25.58, 4.64) * mm});
            skLineSegment(sketch, "E52.3.2", {"start": v(-28.52, 7.69) * mm, "end": v(-27.6, 10.54) * mm});
            skArc(sketch, "E52.4.0", {"start": v(-29.5, -1.6) * mm, "mid": v(-27.45, -0.84) * mm, "end": v(-25.99, 0.78) * mm});
            skArc(sketch, "E52.4.1", {"start": v(-29.18, -4.58) * mm, "mid": v(-27.02, -4.88) * mm, "end": v(-25.26, -6.16) * mm});
            skLineSegment(sketch, "E52.4.2", {"start": v(-29.18, -4.58) * mm, "end": v(-29.5, -1.6) * mm});
            skArc(sketch, "E52.5.0", {"start": v(-26.3, -13.45) * mm, "mid": v(-24.73, -11.93) * mm, "end": v(-24.06, -9.86) * mm});
            skArc(sketch, "E52.5.1", {"start": v(-24.8, -16.05) * mm, "mid": v(-22.7, -15.45) * mm, "end": v(-20.57, -15.9) * mm});
            skLineSegment(sketch, "E52.5.2", {"start": v(-24.8, -16.05) * mm, "end": v(-26.3, -13.45) * mm});
            skArc(sketch, "E52.6.0", {"start": v(-18.55, -22.98) * mm, "mid": v(-17.74, -20.96) * mm, "end": v(-17.97, -18.8) * mm});
            skArc(sketch, "E52.6.1", {"start": v(-16.13, -24.75) * mm, "mid": v(-14.45, -23.35) * mm, "end": v(-12.32, -22.9) * mm});
            skLineSegment(sketch, "E52.6.2", {"start": v(-16.13, -24.75) * mm, "end": v(-18.55, -22.98) * mm});
            skArc(sketch, "E52.7.0", {"start": v(-7.6, -28.54) * mm, "mid": v(-7.68, -26.36) * mm, "end": v(-8.77, -24.48) * mm});
            skArc(sketch, "E52.7.1", {"start": v(-4.67, -29.17) * mm, "mid": v(-3.7, -27.2) * mm, "end": v(-1.94, -25.93) * mm});
            skLineSegment(sketch, "E52.7.2", {"start": v(-4.67, -29.17) * mm, "end": v(-7.6, -28.54) * mm});
            skArc(sketch, "E52.8.0", {"start": v(4.67, -29.17) * mm, "mid": v(3.7, -27.2) * mm, "end": v(1.94, -25.93) * mm});
            skArc(sketch, "E52.8.1", {"start": v(7.6, -28.54) * mm, "mid": v(7.68, -26.36) * mm, "end": v(8.77, -24.48) * mm});
            skLineSegment(sketch, "E52.8.2", {"start": v(7.6, -28.54) * mm, "end": v(4.67, -29.17) * mm});
            skArc(sketch, "E52.9.0", {"start": v(16.13, -24.75) * mm, "mid": v(14.45, -23.35) * mm, "end": v(12.32, -22.9) * mm});
            skArc(sketch, "E52.9.1", {"start": v(18.55, -22.98) * mm, "mid": v(17.74, -20.96) * mm, "end": v(17.97, -18.8) * mm});
            skLineSegment(sketch, "E52.9.2", {"start": v(18.55, -22.98) * mm, "end": v(16.13, -24.75) * mm});
            skArc(sketch, "E52.10.0", {"start": v(24.8, -16.05) * mm, "mid": v(22.7, -15.45) * mm, "end": v(20.57, -15.9) * mm});
            skArc(sketch, "E52.10.1", {"start": v(26.3, -13.45) * mm, "mid": v(24.73, -11.93) * mm, "end": v(24.06, -9.86) * mm});
            skLineSegment(sketch, "E52.10.2", {"start": v(26.3, -13.45) * mm, "end": v(24.8, -16.05) * mm});
            skArc(sketch, "E52.11.0", {"start": v(29.18, -4.58) * mm, "mid": v(27.02, -4.88) * mm, "end": v(25.26, -6.16) * mm});
            skArc(sketch, "E52.11.1", {"start": v(29.5, -1.6) * mm, "mid": v(27.45, -0.84) * mm, "end": v(25.99, 0.78) * mm});
            skLineSegment(sketch, "E52.11.2", {"start": v(29.5, -1.6) * mm, "end": v(29.18, -4.58) * mm});
            skArc(sketch, "E52.12.0", {"start": v(28.52, 7.69) * mm, "mid": v(26.67, 6.53) * mm, "end": v(25.58, 4.64) * mm});
            skArc(sketch, "E52.12.1", {"start": v(27.6, 10.54) * mm, "mid": v(25.42, 10.4) * mm, "end": v(23.42, 11.28) * mm});
            skLineSegment(sketch, "E52.12.2", {"start": v(27.6, 10.54) * mm, "end": v(28.52, 7.69) * mm});
            skArc(sketch, "E52.13.0", {"start": v(22.93, 18.62) * mm, "mid": v(21.7, 16.82) * mm, "end": v(21.48, 14.65) * mm});
            skArc(sketch, "E52.13.1", {"start": v(20.92, 20.85) * mm, "mid": v(19, 19.83) * mm, "end": v(16.81, 19.83) * mm});
            skLineSegment(sketch, "E52.13.2", {"start": v(20.92, 20.85) * mm, "end": v(22.93, 18.62) * mm});
            skArc(sketch, "E52.14.0", {"start": v(13.37, 26.34) * mm, "mid": v(13, 24.2) * mm, "end": v(13.67, 22.12) * mm});
            skArc(sketch, "E52.14.1", {"start": v(10.63, 27.56) * mm, "mid": v(9.28, 25.84) * mm, "end": v(7.3, 24.96) * mm});
            skLineSegment(sketch, "E52.14.2", {"start": v(10.63, 27.56) * mm, "end": v(13.37, 26.34) * mm});
            skCircle(sketch, "E53", {"center": v(0, 0) * mm, "radius": 17.5 * mm});
            skSolve(sketch);
        }
        {
            var Q0;
            Q0 = qSketchRegion(id + "F23", true);
            extrude(context, id + "F24", {"entities" : qUnion([Q0]), "operationType" : NewBodyOperationType.ADD, "depth" : 1.5 * mm, "offsetDistance" : 25 * mm});
        }
        {
            var Q0;
            Q0=makeQuery(id+"F24.opExtrude","CAP_FACE",FACE,{"disambiguationData":[OSD([sQuery(id+"F23.wireOp",EDGE,"E46"),sQuery(id+"F23.wireOp",EDGE,"E50.MirrorCS"),sQuery(id+"F23.wireOp",EDGE,"E49"),sQuery(id+"F23.wireOp",EDGE,"E51.MirrorCS"),sQuery(id+"F23.wireOp",EDGE,"E52.1.0"),sQuery(id+"F23.wireOp",EDGE,"E52.1.1"),sQuery(id+"F23.wireOp",EDGE,"E52.1.2"),sQuery(id+"F23.wireOp",EDGE,"E52.2.0"),sQuery(id+"F23.wireOp",EDGE,"E52.2.1"),sQuery(id+"F23.wireOp",EDGE,"E52.2.2"),sQuery(id+"F23.wireOp",EDGE,"E52.3.0"),sQuery(id+"F23.wireOp",EDGE,"E52.3.1"),sQuery(id+"F23.wireOp",EDGE,"E52.3.2"),sQuery(id+"F23.wireOp",EDGE,"E52.4.0"),sQuery(id+"F23.wireOp",EDGE,"E52.4.1"),sQuery(id+"F23.wireOp",EDGE,"E52.4.2"),sQuery(id+"F23.wireOp",EDGE,"E52.5.0"),sQuery(id+"F23.wireOp",EDGE,"E52.5.1"),sQuery(id+"F23.wireOp",EDGE,"E52.5.2"),sQuery(id+"F23.wireOp",EDGE,"E52.6.0"),sQuery(id+"F23.wireOp",EDGE,"E52.6.1"),sQuery(id+"F23.wireOp",EDGE,"E52.6.2"),sQuery(id+"F23.wireOp",EDGE,"E52.7.0"),sQuery(id+"F23.wireOp",EDGE,"E52.7.1"),sQuery(id+"F23.wireOp",EDGE,"E52.7.2"),sQuery(id+"F23.wireOp",EDGE,"E52.8.0"),sQuery(id+"F23.wireOp",EDGE,"E52.8.1"),sQuery(id+"F23.wireOp",EDGE,"E52.8.2"),sQuery(id+"F23.wireOp",EDGE,"E52.9.0"),sQuery(id+"F23.wireOp",EDGE,"E52.9.1"),sQuery(id+"F23.wireOp",EDGE,"E52.9.2"),sQuery(id+"F23.wireOp",EDGE,"E52.10.0"),sQuery(id+"F23.wireOp",EDGE,"E52.10.1"),sQuery(id+"F23.wireOp",EDGE,"E52.10.2"),sQuery(id+"F23.wireOp",EDGE,"E52.11.0"),sQuery(id+"F23.wireOp",EDGE,"E52.11.1"),sQuery(id+"F23.wireOp",EDGE,"E52.11.2"),sQuery(id+"F23.wireOp",EDGE,"E52.12.0"),sQuery(id+"F23.wireOp",EDGE,"E52.12.1"),sQuery(id+"F23.wireOp",EDGE,"E52.12.2"),sQuery(id+"F23.wireOp",EDGE,"E52.13.0"),sQuery(id+"F23.wireOp",EDGE,"E52.13.1"),sQuery(id+"F23.wireOp",EDGE,"E52.13.2"),sQuery(id+"F23.wireOp",EDGE,"E52.14.0"),sQuery(id+"F23.wireOp",EDGE,"E52.14.1"),sQuery(id+"F23.wireOp",EDGE,"E52.14.2"),sQuery(id+"F23.wireOp",EDGE,"E53")])],"isStart":false});
            var sketch = newSketch(context, id + "F25", { "sketchPlane" : qUnion([Q0])});
            skCircle(sketch, "E54", {"center": v(0, 0) * mm, "radius": 17.5 * mm});
            skCircle(sketch, "E55", {"center": v(0, 0) * mm, "radius": 20.5 * mm});
            skSolve(sketch);
        }
        {
            var Q0;
            Q0 = qSketchRegion(id + "F25", true);
            extrude(context, id + "F26", {"entities" : qUnion([Q0]), "operationType" : NewBodyOperationType.ADD, "depth" : 2.5 * mm, "offsetDistance" : 25 * mm});
        }
        {
            var Q0;
            Q0=makeQuery(id+"F26.opExtrude","CAP_FACE",FACE,{"disambiguationData":[OSD([sQuery(id+"F25.wireOp",EDGE,"E54"),sQuery(id+"F25.wireOp",EDGE,"E55")])],"isStart":false});
            var sketch = newSketch(context, id + "F27", { "sketchPlane" : qUnion([Q0])});
            skCircle(sketch, "E56", {"center": v(0, 0) * mm, "radius": 24 * mm});
            skLineSegment(sketch, "E57", {"start": v(-1.5, 27.5) * mm, "end": v(1.5, 27.5) * mm});
            skLineSegment(sketch, "E58", {"start": v(1.5, 27.5) * mm, "end": v(6.04, 27.5) * mm, "construction": true});
            skArc(sketch, "E59", {"start": v(1.5, 27.5) * mm, "mid": v(2.04, 25.36) * mm, "end": v(3.53, 23.74) * mm});
            skArc(sketch, "E60.MirrorCS", {"start": v(-1.5, 27.5) * mm, "mid": v(-2.04, 25.36) * mm, "end": v(-3.53, 23.74) * mm});
            skArc(sketch, "E61.1.0", {"start": v(-10.58, 25.43) * mm, "mid": v(-9.17, 23.74) * mm, "end": v(-7.12, 22.92) * mm});
            skArc(sketch, "E61.1.1", {"start": v(-13.28, 24.13) * mm, "mid": v(-12.84, 21.97) * mm, "end": v(-13.48, 19.86) * mm});
            skLineSegment(sketch, "E61.1.2", {"start": v(-13.28, 24.13) * mm, "end": v(-10.58, 25.43) * mm});
            skArc(sketch, "E61.2.0", {"start": v(-20.57, 18.32) * mm, "mid": v(-18.56, 17.4) * mm, "end": v(-16.36, 17.56) * mm});
            skArc(sketch, "E61.2.1", {"start": v(-22.44, 15.97) * mm, "mid": v(-21.1, 14.22) * mm, "end": v(-20.76, 12.04) * mm});
            skLineSegment(sketch, "E61.2.2", {"start": v(-22.44, 15.97) * mm, "end": v(-20.57, 18.32) * mm});
            skArc(sketch, "E61.3.0", {"start": v(-26.48, 7.58) * mm, "mid": v(-24.27, 7.63) * mm, "end": v(-22.36, 8.72) * mm});
            skArc(sketch, "E61.3.1", {"start": v(-27.14, 4.66) * mm, "mid": v(-25.18, 3.66) * mm, "end": v(-23.93, 1.84) * mm});
            skLineSegment(sketch, "E61.3.2", {"start": v(-27.14, 4.66) * mm, "end": v(-26.48, 7.58) * mm});
            skArc(sketch, "E61.4.0", {"start": v(-27.14, -4.66) * mm, "mid": v(-25.18, -3.66) * mm, "end": v(-23.93, -1.84) * mm});
            skArc(sketch, "E61.4.1", {"start": v(-26.48, -7.58) * mm, "mid": v(-24.27, -7.63) * mm, "end": v(-22.36, -8.72) * mm});
            skLineSegment(sketch, "E61.4.2", {"start": v(-26.48, -7.58) * mm, "end": v(-27.14, -4.66) * mm});
            skArc(sketch, "E61.5.0", {"start": v(-22.44, -15.97) * mm, "mid": v(-21.1, -14.22) * mm, "end": v(-20.76, -12.04) * mm});
            skArc(sketch, "E61.5.1", {"start": v(-20.57, -18.32) * mm, "mid": v(-18.56, -17.4) * mm, "end": v(-16.36, -17.56) * mm});
            skLineSegment(sketch, "E61.5.2", {"start": v(-20.57, -18.32) * mm, "end": v(-22.44, -15.97) * mm});
            skArc(sketch, "E61.6.0", {"start": v(-13.28, -24.13) * mm, "mid": v(-12.84, -21.97) * mm, "end": v(-13.48, -19.86) * mm});
            skArc(sketch, "E61.6.1", {"start": v(-10.58, -25.43) * mm, "mid": v(-9.17, -23.74) * mm, "end": v(-7.12, -22.92) * mm});
            skLineSegment(sketch, "E61.6.2", {"start": v(-10.58, -25.43) * mm, "end": v(-13.28, -24.13) * mm});
            skArc(sketch, "E61.7.0", {"start": v(-1.5, -27.5) * mm, "mid": v(-2.04, -25.36) * mm, "end": v(-3.53, -23.74) * mm});
            skArc(sketch, "E61.7.1", {"start": v(1.5, -27.5) * mm, "mid": v(2.04, -25.36) * mm, "end": v(3.53, -23.74) * mm});
            skLineSegment(sketch, "E61.7.2", {"start": v(1.5, -27.5) * mm, "end": v(-1.5, -27.5) * mm});
            skArc(sketch, "E61.8.0", {"start": v(10.58, -25.43) * mm, "mid": v(9.17, -23.74) * mm, "end": v(7.12, -22.92) * mm});
            skArc(sketch, "E61.8.1", {"start": v(13.28, -24.13) * mm, "mid": v(12.84, -21.97) * mm, "end": v(13.48, -19.86) * mm});
            skLineSegment(sketch, "E61.8.2", {"start": v(13.28, -24.13) * mm, "end": v(10.58, -25.43) * mm});
            skArc(sketch, "E61.9.0", {"start": v(20.57, -18.32) * mm, "mid": v(18.56, -17.4) * mm, "end": v(16.36, -17.56) * mm});
            skArc(sketch, "E61.9.1", {"start": v(22.44, -15.97) * mm, "mid": v(21.1, -14.22) * mm, "end": v(20.76, -12.04) * mm});
            skLineSegment(sketch, "E61.9.2", {"start": v(22.44, -15.97) * mm, "end": v(20.57, -18.32) * mm});
            skArc(sketch, "E61.10.0", {"start": v(26.48, -7.58) * mm, "mid": v(24.27, -7.63) * mm, "end": v(22.36, -8.72) * mm});
            skArc(sketch, "E61.10.1", {"start": v(27.14, -4.66) * mm, "mid": v(25.18, -3.66) * mm, "end": v(23.93, -1.84) * mm});
            skLineSegment(sketch, "E61.10.2", {"start": v(27.14, -4.66) * mm, "end": v(26.48, -7.58) * mm});
            skArc(sketch, "E61.11.0", {"start": v(27.14, 4.66) * mm, "mid": v(25.18, 3.66) * mm, "end": v(23.93, 1.84) * mm});
            skArc(sketch, "E61.11.1", {"start": v(26.48, 7.58) * mm, "mid": v(24.27, 7.63) * mm, "end": v(22.36, 8.72) * mm});
            skLineSegment(sketch, "E61.11.2", {"start": v(26.48, 7.58) * mm, "end": v(27.14, 4.66) * mm});
            skArc(sketch, "E61.12.0", {"start": v(22.44, 15.97) * mm, "mid": v(21.1, 14.22) * mm, "end": v(20.76, 12.04) * mm});
            skArc(sketch, "E61.12.1", {"start": v(20.57, 18.32) * mm, "mid": v(18.56, 17.4) * mm, "end": v(16.36, 17.56) * mm});
            skLineSegment(sketch, "E61.12.2", {"start": v(20.57, 18.32) * mm, "end": v(22.44, 15.97) * mm});
            skArc(sketch, "E61.13.0", {"start": v(13.28, 24.13) * mm, "mid": v(12.84, 21.97) * mm, "end": v(13.48, 19.86) * mm});
            skArc(sketch, "E61.13.1", {"start": v(10.58, 25.43) * mm, "mid": v(9.17, 23.74) * mm, "end": v(7.12, 22.92) * mm});
            skLineSegment(sketch, "E61.13.2", {"start": v(10.58, 25.43) * mm, "end": v(13.28, 24.13) * mm});
            skCircle(sketch, "E62", {"center": v(0, 0) * mm, "radius": 17.5 * mm});
            skSolve(sketch);
        }
        {
            var Q0;
            Q0 = qSketchRegion(id + "F27", true);
            extrude(context, id + "F28", {"entities" : qUnion([Q0]), "operationType" : NewBodyOperationType.ADD, "depth" : 1.5 * mm, "offsetDistance" : 25 * mm});
        }
        {
            var Q0;
            Q0=makeQuery(id+"F28.opExtrude","CAP_FACE",FACE,{"disambiguationData":[OSD([sQuery(id+"F27.wireOp",EDGE,"E56"),sQuery(id+"F27.wireOp",EDGE,"E57"),sQuery(id+"F27.wireOp",EDGE,"E59"),sQuery(id+"F27.wireOp",EDGE,"E60.MirrorCS"),sQuery(id+"F27.wireOp",EDGE,"E61.1.0"),sQuery(id+"F27.wireOp",EDGE,"E61.1.1"),sQuery(id+"F27.wireOp",EDGE,"E61.1.2"),sQuery(id+"F27.wireOp",EDGE,"E61.2.0"),sQuery(id+"F27.wireOp",EDGE,"E61.2.1"),sQuery(id+"F27.wireOp",EDGE,"E61.2.2"),sQuery(id+"F27.wireOp",EDGE,"E61.3.0"),sQuery(id+"F27.wireOp",EDGE,"E61.3.1"),sQuery(id+"F27.wireOp",EDGE,"E61.3.2"),sQuery(id+"F27.wireOp",EDGE,"E61.4.0"),sQuery(id+"F27.wireOp",EDGE,"E61.4.1"),sQuery(id+"F27.wireOp",EDGE,"E61.4.2"),sQuery(id+"F27.wireOp",EDGE,"E61.5.0"),sQuery(id+"F27.wireOp",EDGE,"E61.5.1"),sQuery(id+"F27.wireOp",EDGE,"E61.5.2"),sQuery(id+"F27.wireOp",EDGE,"E61.6.0"),sQuery(id+"F27.wireOp",EDGE,"E61.6.1"),sQuery(id+"F27.wireOp",EDGE,"E61.6.2"),sQuery(id+"F27.wireOp",EDGE,"E61.7.0"),sQuery(id+"F27.wireOp",EDGE,"E61.7.1"),sQuery(id+"F27.wireOp",EDGE,"E61.7.2"),sQuery(id+"F27.wireOp",EDGE,"E61.8.0"),sQuery(id+"F27.wireOp",EDGE,"E61.8.1"),sQuery(id+"F27.wireOp",EDGE,"E61.8.2"),sQuery(id+"F27.wireOp",EDGE,"E61.9.0"),sQuery(id+"F27.wireOp",EDGE,"E61.9.1"),sQuery(id+"F27.wireOp",EDGE,"E61.9.2"),sQuery(id+"F27.wireOp",EDGE,"E61.10.0"),sQuery(id+"F27.wireOp",EDGE,"E61.10.1"),sQuery(id+"F27.wireOp",EDGE,"E61.10.2"),sQuery(id+"F27.wireOp",EDGE,"E61.11.0"),sQuery(id+"F27.wireOp",EDGE,"E61.11.1"),sQuery(id+"F27.wireOp",EDGE,"E61.11.2"),sQuery(id+"F27.wireOp",EDGE,"E61.12.0"),sQuery(id+"F27.wireOp",EDGE,"E61.12.1"),sQuery(id+"F27.wireOp",EDGE,"E61.12.2"),sQuery(id+"F27.wireOp",EDGE,"E61.13.0"),sQuery(id+"F27.wireOp",EDGE,"E61.13.1"),sQuery(id+"F27.wireOp",EDGE,"E61.13.2"),sQuery(id+"F27.wireOp",EDGE,"E62")])],"isStart":false});
            var sketch = newSketch(context, id + "F29", { "sketchPlane" : qUnion([Q0])});
            skCircle(sketch, "E63", {"center": v(0, 0) * mm, "radius": 17.5 * mm});
            skCircle(sketch, "E64", {"center": v(0, 0) * mm, "radius": 20.5 * mm});
            skSolve(sketch);
        }
        {
            var Q0;
            Q0 = qSketchRegion(id + "F29", true);
            extrude(context, id + "F30", {"entities" : qUnion([Q0]), "operationType" : NewBodyOperationType.ADD, "depth" : 2.5 * mm, "offsetDistance" : 25 * mm});
        }
        {
            var Q0;
            Q0=makeQuery(id+"F30.opExtrude","CAP_FACE",FACE,{"disambiguationData":[OSD([sQuery(id+"F29.wireOp",EDGE,"E63"),sQuery(id+"F29.wireOp",EDGE,"E64")])],"isStart":false});
            var sketch = newSketch(context, id + "F31", { "sketchPlane" : qUnion([Q0])});
            skCircle(sketch, "E65", {"center": v(0, 0) * mm, "radius": 22 * mm});
            skLineSegment(sketch, "E66", {"start": v(-1.5, 25.5) * mm, "end": v(1.5, 25.5) * mm});
            skLineSegment(sketch, "E67", {"start": v(1.5, 25.5) * mm, "end": v(7.04, 25.5) * mm, "construction": true});
            skArc(sketch, "E68", {"start": v(1.5, 25.5) * mm, "mid": v(2.05, 23.34) * mm, "end": v(3.58, 21.7) * mm});
            skArc(sketch, "E69.MirrorCS", {"start": v(-1.5, 25.5) * mm, "mid": v(-2.05, 23.34) * mm, "end": v(-3.58, 21.7) * mm});
            skCircle(sketch, "E70", {"center": v(0, 0) * mm, "radius": 17.5 * mm});
            skArc(sketch, "E71.1.0", {"start": v(-10.52, 23.28) * mm, "mid": v(-9.03, 21.62) * mm, "end": v(-6.92, 20.88) * mm});
            skArc(sketch, "E71.1.1", {"start": v(-13.18, 21.88) * mm, "mid": v(-12.66, 19.7) * mm, "end": v(-13.26, 17.56) * mm});
            skLineSegment(sketch, "E71.1.2", {"start": v(-13.18, 21.88) * mm, "end": v(-10.52, 23.28) * mm});
            skArc(sketch, "E71.2.0", {"start": v(-20.13, 15.72) * mm, "mid": v(-18.04, 14.95) * mm, "end": v(-15.83, 15.28) * mm});
            skArc(sketch, "E71.2.1", {"start": v(-21.84, 13.25) * mm, "mid": v(-20.37, 11.57) * mm, "end": v(-19.9, 9.39) * mm});
            skLineSegment(sketch, "E71.2.2", {"start": v(-21.84, 13.25) * mm, "end": v(-20.13, 15.72) * mm});
            skArc(sketch, "E71.3.0", {"start": v(-25.13, 4.56) * mm, "mid": v(-22.92, 4.85) * mm, "end": v(-21.12, 6.17) * mm});
            skArc(sketch, "E71.3.1", {"start": v(-25.5, 1.58) * mm, "mid": v(-23.41, 0.77) * mm, "end": v(-21.98, -0.94) * mm});
            skLineSegment(sketch, "E71.3.2", {"start": v(-25.5, 1.58) * mm, "end": v(-25.13, 4.56) * mm});
            skArc(sketch, "E71.4.0", {"start": v(-24.37, -7.64) * mm, "mid": v(-22.55, -6.36) * mm, "end": v(-21.57, -4.35) * mm});
            skArc(sketch, "E71.4.1", {"start": v(-23.31, -10.44) * mm, "mid": v(-21.1, -10.2) * mm, "end": v(-19.03, -11.04) * mm});
            skLineSegment(sketch, "E71.4.2", {"start": v(-23.31, -10.44) * mm, "end": v(-24.37, -7.64) * mm});
            skArc(sketch, "E71.5.0", {"start": v(-18.03, -18.1) * mm, "mid": v(-17.01, -16.1) * mm, "end": v(-17.07, -13.87) * mm});
            skArc(sketch, "E71.5.1", {"start": v(-15.79, -20.08) * mm, "mid": v(-13.94, -18.83) * mm, "end": v(-11.72, -18.62) * mm});
            skLineSegment(sketch, "E71.5.2", {"start": v(-15.79, -20.08) * mm, "end": v(-18.03, -18.1) * mm});
            skArc(sketch, "E71.6.0", {"start": v(-7.56, -24.4) * mm, "mid": v(-7.58, -22.17) * mm, "end": v(-8.67, -20.22) * mm});
            skArc(sketch, "E71.6.1", {"start": v(-4.65, -25.12) * mm, "mid": v(-3.6, -23.15) * mm, "end": v(-1.72, -21.93) * mm});
            skLineSegment(sketch, "E71.6.2", {"start": v(-4.65, -25.12) * mm, "end": v(-7.56, -24.4) * mm});
            skArc(sketch, "E71.7.0", {"start": v(4.65, -25.12) * mm, "mid": v(3.6, -23.15) * mm, "end": v(1.72, -21.93) * mm});
            skArc(sketch, "E71.7.1", {"start": v(7.56, -24.4) * mm, "mid": v(7.58, -22.17) * mm, "end": v(8.67, -20.22) * mm});
            skLineSegment(sketch, "E71.7.2", {"start": v(7.56, -24.4) * mm, "end": v(4.65, -25.12) * mm});
            skArc(sketch, "E71.8.0", {"start": v(15.79, -20.08) * mm, "mid": v(13.94, -18.83) * mm, "end": v(11.72, -18.62) * mm});
            skArc(sketch, "E71.8.1", {"start": v(18.03, -18.1) * mm, "mid": v(17.01, -16.1) * mm, "end": v(17.07, -13.87) * mm});
            skLineSegment(sketch, "E71.8.2", {"start": v(18.03, -18.1) * mm, "end": v(15.79, -20.08) * mm});
            skArc(sketch, "E71.9.0", {"start": v(23.31, -10.44) * mm, "mid": v(21.1, -10.2) * mm, "end": v(19.03, -11.04) * mm});
            skArc(sketch, "E71.9.1", {"start": v(24.37, -7.64) * mm, "mid": v(22.55, -6.36) * mm, "end": v(21.57, -4.35) * mm});
            skLineSegment(sketch, "E71.9.2", {"start": v(24.37, -7.64) * mm, "end": v(23.31, -10.44) * mm});
            skArc(sketch, "E71.10.0", {"start": v(25.5, 1.58) * mm, "mid": v(23.41, 0.77) * mm, "end": v(21.98, -0.94) * mm});
            skArc(sketch, "E71.10.1", {"start": v(25.13, 4.56) * mm, "mid": v(22.92, 4.85) * mm, "end": v(21.12, 6.17) * mm});
            skLineSegment(sketch, "E71.10.2", {"start": v(25.13, 4.56) * mm, "end": v(25.5, 1.58) * mm});
            skArc(sketch, "E71.11.0", {"start": v(21.84, 13.25) * mm, "mid": v(20.37, 11.57) * mm, "end": v(19.9, 9.39) * mm});
            skArc(sketch, "E71.11.1", {"start": v(20.13, 15.72) * mm, "mid": v(18.04, 14.95) * mm, "end": v(15.83, 15.28) * mm});
            skLineSegment(sketch, "E71.11.2", {"start": v(20.13, 15.72) * mm, "end": v(21.84, 13.25) * mm});
            skArc(sketch, "E71.12.0", {"start": v(13.18, 21.88) * mm, "mid": v(12.66, 19.7) * mm, "end": v(13.26, 17.56) * mm});
            skArc(sketch, "E71.12.1", {"start": v(10.52, 23.28) * mm, "mid": v(9.03, 21.62) * mm, "end": v(6.92, 20.88) * mm});
            skLineSegment(sketch, "E71.12.2", {"start": v(10.52, 23.28) * mm, "end": v(13.18, 21.88) * mm});
            skSolve(sketch);
        }
        {
            var Q0;
            Q0 = qSketchRegion(id + "F31", true);
            extrude(context, id + "F32", {"entities" : qUnion([Q0]), "operationType" : NewBodyOperationType.ADD, "depth" : 1.5 * mm, "offsetDistance" : 25 * mm});
        }
        {
            var Q0;
            Q0=makeQuery(id+"F32.opExtrude","CAP_FACE",FACE,{"disambiguationData":[OSD([sQuery(id+"F31.wireOp",EDGE,"E65"),sQuery(id+"F31.wireOp",EDGE,"E66"),sQuery(id+"F31.wireOp",EDGE,"E68"),sQuery(id+"F31.wireOp",EDGE,"E69.MirrorCS"),sQuery(id+"F31.wireOp",EDGE,"E70"),sQuery(id+"F31.wireOp",EDGE,"E71.1.0"),sQuery(id+"F31.wireOp",EDGE,"E71.1.1"),sQuery(id+"F31.wireOp",EDGE,"E71.1.2"),sQuery(id+"F31.wireOp",EDGE,"E71.2.0"),sQuery(id+"F31.wireOp",EDGE,"E71.2.1"),sQuery(id+"F31.wireOp",EDGE,"E71.2.2"),sQuery(id+"F31.wireOp",EDGE,"E71.3.0"),sQuery(id+"F31.wireOp",EDGE,"E71.3.1"),sQuery(id+"F31.wireOp",EDGE,"E71.3.2"),sQuery(id+"F31.wireOp",EDGE,"E71.4.0"),sQuery(id+"F31.wireOp",EDGE,"E71.4.1"),sQuery(id+"F31.wireOp",EDGE,"E71.4.2"),sQuery(id+"F31.wireOp",EDGE,"E71.5.0"),sQuery(id+"F31.wireOp",EDGE,"E71.5.1"),sQuery(id+"F31.wireOp",EDGE,"E71.5.2"),sQuery(id+"F31.wireOp",EDGE,"E71.6.0"),sQuery(id+"F31.wireOp",EDGE,"E71.6.1"),sQuery(id+"F31.wireOp",EDGE,"E71.6.2"),sQuery(id+"F31.wireOp",EDGE,"E71.7.0"),sQuery(id+"F31.wireOp",EDGE,"E71.7.1"),sQuery(id+"F31.wireOp",EDGE,"E71.7.2"),sQuery(id+"F31.wireOp",EDGE,"E71.8.0"),sQuery(id+"F31.wireOp",EDGE,"E71.8.1"),sQuery(id+"F31.wireOp",EDGE,"E71.8.2"),sQuery(id+"F31.wireOp",EDGE,"E71.9.0"),sQuery(id+"F31.wireOp",EDGE,"E71.9.1"),sQuery(id+"F31.wireOp",EDGE,"E71.9.2"),sQuery(id+"F31.wireOp",EDGE,"E71.10.0"),sQuery(id+"F31.wireOp",EDGE,"E71.10.1"),sQuery(id+"F31.wireOp",EDGE,"E71.10.2"),sQuery(id+"F31.wireOp",EDGE,"E71.11.0"),sQuery(id+"F31.wireOp",EDGE,"E71.11.1"),sQuery(id+"F31.wireOp",EDGE,"E71.11.2"),sQuery(id+"F31.wireOp",EDGE,"E71.12.0"),sQuery(id+"F31.wireOp",EDGE,"E71.12.1"),sQuery(id+"F31.wireOp",EDGE,"E71.12.2")])],"isStart":false});
            var sketch = newSketch(context, id + "F33", { "sketchPlane" : qUnion([Q0])});
            skCircle(sketch, "E72", {"center": v(0, 0) * mm, "radius": 17.5 * mm});
            skCircle(sketch, "E73", {"center": v(0, 0) * mm, "radius": 20.5 * mm});
            skSolve(sketch);
        }
        {
            var Q0;
            Q0 = qSketchRegion(id + "F33", true);
            extrude(context, id + "F34", {"entities" : qUnion([Q0]), "operationType" : NewBodyOperationType.ADD, "depth" : 2.5 * mm, "offsetDistance" : 25 * mm});
        }
        {
            var Q0;
            Q0=makeQuery(id+"F34.opExtrude","CAP_FACE",FACE,{"disambiguationData":[OSD([sQuery(id+"F33.wireOp",EDGE,"E72"),sQuery(id+"F33.wireOp",EDGE,"E73")])],"isStart":false});
            var sketch = newSketch(context, id + "F35", { "sketchPlane" : qUnion([Q0])});
            skCircle(sketch, "E74", {"center": v(0, 0) * mm, "radius": 20.5 * mm});
            skLineSegment(sketch, "E75", {"start": v(-1.5, 24) * mm, "end": v(1.5, 24) * mm});
            skLineSegment(sketch, "E76", {"start": v(1.5, 24) * mm, "end": v(8.08, 24) * mm, "construction": true});
            skArc(sketch, "E77", {"start": v(1.5, 24) * mm, "mid": v(2.07, 21.81) * mm, "end": v(3.63, 20.18) * mm});
            skArc(sketch, "E78.MirrorCS", {"start": v(-1.5, 24) * mm, "mid": v(-2.07, 21.81) * mm, "end": v(-3.63, 20.18) * mm});
            skArc(sketch, "E79.1.0", {"start": v(-13.3, 20.03) * mm, "mid": v(-12.7, 17.86) * mm, "end": v(-13.23, 15.66) * mm});
            skLineSegment(sketch, "E79.1.1", {"start": v(-13.3, 20.03) * mm, "end": v(-10.7, 21.53) * mm});
            skArc(sketch, "E79.1.2", {"start": v(-10.7, 21.53) * mm, "mid": v(-9.12, 19.92) * mm, "end": v(-6.95, 19.29) * mm});
            skArc(sketch, "E79.2.0", {"start": v(-21.53, 10.7) * mm, "mid": v(-19.92, 9.12) * mm, "end": v(-19.29, 6.95) * mm});
            skLineSegment(sketch, "E79.2.1", {"start": v(-21.53, 10.7) * mm, "end": v(-20.03, 13.3) * mm});
            skArc(sketch, "E79.2.2", {"start": v(-20.03, 13.3) * mm, "mid": v(-17.86, 12.7) * mm, "end": v(-15.66, 13.23) * mm});
            skArc(sketch, "E79.3.0", {"start": v(-24, -1.5) * mm, "mid": v(-21.81, -2.07) * mm, "end": v(-20.18, -3.63) * mm});
            skLineSegment(sketch, "E79.3.1", {"start": v(-24, -1.5) * mm, "end": v(-24, 1.5) * mm});
            skArc(sketch, "E79.3.2", {"start": v(-24, 1.5) * mm, "mid": v(-21.81, 2.07) * mm, "end": v(-20.18, 3.63) * mm});
            skArc(sketch, "E79.4.0", {"start": v(-20.03, -13.3) * mm, "mid": v(-17.86, -12.7) * mm, "end": v(-15.66, -13.23) * mm});
            skLineSegment(sketch, "E79.4.1", {"start": v(-20.03, -13.3) * mm, "end": v(-21.53, -10.7) * mm});
            skArc(sketch, "E79.4.2", {"start": v(-21.53, -10.7) * mm, "mid": v(-19.92, -9.12) * mm, "end": v(-19.29, -6.95) * mm});
            skArc(sketch, "E79.5.0", {"start": v(-10.7, -21.53) * mm, "mid": v(-9.12, -19.92) * mm, "end": v(-6.95, -19.29) * mm});
            skLineSegment(sketch, "E79.5.1", {"start": v(-10.7, -21.53) * mm, "end": v(-13.3, -20.03) * mm});
            skArc(sketch, "E79.5.2", {"start": v(-13.3, -20.03) * mm, "mid": v(-12.7, -17.86) * mm, "end": v(-13.23, -15.66) * mm});
            skArc(sketch, "E79.6.0", {"start": v(1.5, -24) * mm, "mid": v(2.07, -21.81) * mm, "end": v(3.63, -20.18) * mm});
            skLineSegment(sketch, "E79.6.1", {"start": v(1.5, -24) * mm, "end": v(-1.5, -24) * mm});
            skArc(sketch, "E79.6.2", {"start": v(-1.5, -24) * mm, "mid": v(-2.07, -21.81) * mm, "end": v(-3.63, -20.18) * mm});
            skArc(sketch, "E79.7.0", {"start": v(13.3, -20.03) * mm, "mid": v(12.7, -17.86) * mm, "end": v(13.23, -15.66) * mm});
            skLineSegment(sketch, "E79.7.1", {"start": v(13.3, -20.03) * mm, "end": v(10.7, -21.53) * mm});
            skArc(sketch, "E79.7.2", {"start": v(10.7, -21.53) * mm, "mid": v(9.12, -19.92) * mm, "end": v(6.95, -19.29) * mm});
            skArc(sketch, "E79.8.0", {"start": v(21.53, -10.7) * mm, "mid": v(19.92, -9.12) * mm, "end": v(19.29, -6.95) * mm});
            skLineSegment(sketch, "E79.8.1", {"start": v(21.53, -10.7) * mm, "end": v(20.03, -13.3) * mm});
            skArc(sketch, "E79.8.2", {"start": v(20.03, -13.3) * mm, "mid": v(17.86, -12.7) * mm, "end": v(15.66, -13.23) * mm});
            skArc(sketch, "E79.9.0", {"start": v(24, 1.5) * mm, "mid": v(21.81, 2.07) * mm, "end": v(20.18, 3.63) * mm});
            skLineSegment(sketch, "E79.9.1", {"start": v(24, 1.5) * mm, "end": v(24, -1.5) * mm});
            skArc(sketch, "E79.9.2", {"start": v(24, -1.5) * mm, "mid": v(21.81, -2.07) * mm, "end": v(20.18, -3.63) * mm});
            skArc(sketch, "E79.10.0", {"start": v(20.03, 13.3) * mm, "mid": v(17.86, 12.7) * mm, "end": v(15.66, 13.23) * mm});
            skLineSegment(sketch, "E79.10.1", {"start": v(20.03, 13.3) * mm, "end": v(21.53, 10.7) * mm});
            skArc(sketch, "E79.10.2", {"start": v(21.53, 10.7) * mm, "mid": v(19.92, 9.12) * mm, "end": v(19.29, 6.95) * mm});
            skArc(sketch, "E79.11.0", {"start": v(10.7, 21.53) * mm, "mid": v(9.12, 19.92) * mm, "end": v(6.95, 19.29) * mm});
            skLineSegment(sketch, "E79.11.1", {"start": v(10.7, 21.53) * mm, "end": v(13.3, 20.03) * mm});
            skArc(sketch, "E79.11.2", {"start": v(13.3, 20.03) * mm, "mid": v(12.7, 17.86) * mm, "end": v(13.23, 15.66) * mm});
            skCircle(sketch, "E80", {"center": v(0, 0) * mm, "radius": 17.5 * mm});
            skSolve(sketch);
        }
        {
            var Q0;
            Q0 = qSketchRegion(id + "F35", true);
            extrude(context, id + "F36", {"entities" : qUnion([Q0]), "operationType" : NewBodyOperationType.ADD, "depth" : 1.5 * mm, "offsetDistance" : 25 * mm});
        }
        {
            var Q0;
            Q0=makeQuery(id+"F36.opExtrude","CAP_FACE",FACE,{"disambiguationData":[OSD([sQuery(id+"F35.wireOp",EDGE,"E74"),sQuery(id+"F35.wireOp",EDGE,"E75"),sQuery(id+"F35.wireOp",EDGE,"E77"),sQuery(id+"F35.wireOp",EDGE,"E78.MirrorCS"),sQuery(id+"F35.wireOp",EDGE,"E79.1.0"),sQuery(id+"F35.wireOp",EDGE,"E79.1.1"),sQuery(id+"F35.wireOp",EDGE,"E79.1.2"),sQuery(id+"F35.wireOp",EDGE,"E79.2.0"),sQuery(id+"F35.wireOp",EDGE,"E79.2.1"),sQuery(id+"F35.wireOp",EDGE,"E79.2.2"),sQuery(id+"F35.wireOp",EDGE,"E79.3.0"),sQuery(id+"F35.wireOp",EDGE,"E79.3.1"),sQuery(id+"F35.wireOp",EDGE,"E79.3.2"),sQuery(id+"F35.wireOp",EDGE,"E79.4.0"),sQuery(id+"F35.wireOp",EDGE,"E79.4.1"),sQuery(id+"F35.wireOp",EDGE,"E79.4.2"),sQuery(id+"F35.wireOp",EDGE,"E79.5.0"),sQuery(id+"F35.wireOp",EDGE,"E79.5.1"),sQuery(id+"F35.wireOp",EDGE,"E79.5.2"),sQuery(id+"F35.wireOp",EDGE,"E79.6.0"),sQuery(id+"F35.wireOp",EDGE,"E79.6.1"),sQuery(id+"F35.wireOp",EDGE,"E79.6.2"),sQuery(id+"F35.wireOp",EDGE,"E79.7.0"),sQuery(id+"F35.wireOp",EDGE,"E79.7.1"),sQuery(id+"F35.wireOp",EDGE,"E79.7.2"),sQuery(id+"F35.wireOp",EDGE,"E79.8.0"),sQuery(id+"F35.wireOp",EDGE,"E79.8.1"),sQuery(id+"F35.wireOp",EDGE,"E79.8.2"),sQuery(id+"F35.wireOp",EDGE,"E79.9.0"),sQuery(id+"F35.wireOp",EDGE,"E79.9.1"),sQuery(id+"F35.wireOp",EDGE,"E79.9.2"),sQuery(id+"F35.wireOp",EDGE,"E79.10.0"),sQuery(id+"F35.wireOp",EDGE,"E79.10.1"),sQuery(id+"F35.wireOp",EDGE,"E79.10.2"),sQuery(id+"F35.wireOp",EDGE,"E79.11.0"),sQuery(id+"F35.wireOp",EDGE,"E79.11.1"),sQuery(id+"F35.wireOp",EDGE,"E79.11.2"),sQuery(id+"F35.wireOp",EDGE,"E80")])],"isStart":false});
            var sketch = newSketch(context, id + "F37", { "sketchPlane" : qUnion([Q0])});
            skCircle(sketch, "E81", {"center": v(0, 0) * mm, "radius": 17.5 * mm});
            skCircle(sketch, "E82", {"center": v(0, 0) * mm, "radius": 18.5 * mm});
            skSolve(sketch);
        }
        {
            var Q0;
            Q0 = qSketchRegion(id + "F37", true);
            extrude(context, id + "F38", {"entities" : qUnion([Q0]), "operationType" : NewBodyOperationType.ADD, "depth" : 2.5 * mm, "offsetDistance" : 25 * mm});
        }
        {
            var Q0;
            Q0=makeQuery(id+"F38.opExtrude","CAP_FACE",FACE,{"disambiguationData":[OSD([sQuery(id+"F37.wireOp",EDGE,"E81"),sQuery(id+"F37.wireOp",EDGE,"E82")])],"isStart":false});
            var sketch = newSketch(context, id + "F39", { "sketchPlane" : qUnion([Q0])});
            skCircle(sketch, "E83", {"center": v(0, 0) * mm, "radius": 18.5 * mm});
            skLineSegment(sketch, "E84", {"start": v(-1.5, 22) * mm, "end": v(1.5, 22) * mm});
            skLineSegment(sketch, "E85", {"start": v(1.5, 22) * mm, "end": v(5.15, 22) * mm, "construction": true});
            skArc(sketch, "E86", {"start": v(1.5, 22) * mm, "mid": v(2.1, 19.77) * mm, "end": v(3.72, 18.12) * mm});
            skArc(sketch, "E87.MirrorCS", {"start": v(-1.5, 22) * mm, "mid": v(-2.1, 19.77) * mm, "end": v(-3.72, 18.12) * mm});
            skArc(sketch, "E88.1.0", {"start": v(-10.63, 19.32) * mm, "mid": v(-8.93, 17.76) * mm, "end": v(-6.67, 17.25) * mm});
            skArc(sketch, "E88.1.1", {"start": v(-13.16, 17.7) * mm, "mid": v(-12.45, 15.5) * mm, "end": v(-12.92, 13.24) * mm});
            skLineSegment(sketch, "E88.1.2", {"start": v(-13.16, 17.7) * mm, "end": v(-10.63, 19.32) * mm});
            skArc(sketch, "E88.2.0", {"start": v(-19.39, 10.5) * mm, "mid": v(-17.11, 10.12) * mm, "end": v(-14.94, 10.9) * mm});
            skArc(sketch, "E88.2.1", {"start": v(-20.64, 7.77) * mm, "mid": v(-18.85, 6.3) * mm, "end": v(-18.03, 4.15) * mm});
            skLineSegment(sketch, "E88.2.2", {"start": v(-20.64, 7.77) * mm, "end": v(-19.39, 10.5) * mm});
            skArc(sketch, "E88.3.0", {"start": v(-21.99, -1.65) * mm, "mid": v(-19.86, -0.74) * mm, "end": v(-18.47, 1.1) * mm});
            skArc(sketch, "E88.3.1", {"start": v(-21.56, -4.62) * mm, "mid": v(-19.27, -4.88) * mm, "end": v(-17.4, -6.26) * mm});
            skLineSegment(sketch, "E88.3.2", {"start": v(-21.56, -4.62) * mm, "end": v(-21.99, -1.65) * mm});
            skArc(sketch, "E88.4.0", {"start": v(-17.6, -13.27) * mm, "mid": v(-16.3, -11.36) * mm, "end": v(-16.13, -9.06) * mm});
            skArc(sketch, "E88.4.1", {"start": v(-15.64, -15.54) * mm, "mid": v(-13.57, -14.53) * mm, "end": v(-11.26, -14.68) * mm});
            skLineSegment(sketch, "E88.4.2", {"start": v(-15.64, -15.54) * mm, "end": v(-17.6, -13.27) * mm});
            skArc(sketch, "E88.5.0", {"start": v(-7.64, -20.69) * mm, "mid": v(-7.58, -18.38) * mm, "end": v(-8.67, -16.34) * mm});
            skArc(sketch, "E88.5.1", {"start": v(-4.76, -21.53) * mm, "mid": v(-3.56, -19.56) * mm, "end": v(-1.54, -18.44) * mm});
            skLineSegment(sketch, "E88.5.2", {"start": v(-4.76, -21.53) * mm, "end": v(-7.64, -20.69) * mm});
            skArc(sketch, "E88.6.0", {"start": v(4.76, -21.53) * mm, "mid": v(3.56, -19.56) * mm, "end": v(1.54, -18.44) * mm});
            skArc(sketch, "E88.6.1", {"start": v(7.64, -20.69) * mm, "mid": v(7.58, -18.38) * mm, "end": v(8.67, -16.34) * mm});
            skLineSegment(sketch, "E88.6.2", {"start": v(7.64, -20.69) * mm, "end": v(4.76, -21.53) * mm});
            skArc(sketch, "E88.7.0", {"start": v(15.64, -15.54) * mm, "mid": v(13.57, -14.53) * mm, "end": v(11.26, -14.68) * mm});
            skArc(sketch, "E88.7.1", {"start": v(17.6, -13.27) * mm, "mid": v(16.3, -11.36) * mm, "end": v(16.13, -9.06) * mm});
            skLineSegment(sketch, "E88.7.2", {"start": v(17.6, -13.27) * mm, "end": v(15.64, -15.54) * mm});
            skArc(sketch, "E88.8.0", {"start": v(21.56, -4.62) * mm, "mid": v(19.27, -4.88) * mm, "end": v(17.4, -6.26) * mm});
            skArc(sketch, "E88.8.1", {"start": v(21.99, -1.65) * mm, "mid": v(19.86, -0.74) * mm, "end": v(18.47, 1.1) * mm});
            skLineSegment(sketch, "E88.8.2", {"start": v(21.99, -1.65) * mm, "end": v(21.56, -4.62) * mm});
            skArc(sketch, "E88.9.0", {"start": v(20.64, 7.77) * mm, "mid": v(18.85, 6.3) * mm, "end": v(18.03, 4.15) * mm});
            skArc(sketch, "E88.9.1", {"start": v(19.39, 10.5) * mm, "mid": v(17.11, 10.12) * mm, "end": v(14.94, 10.9) * mm});
            skLineSegment(sketch, "E88.9.2", {"start": v(19.39, 10.5) * mm, "end": v(20.64, 7.77) * mm});
            skArc(sketch, "E88.10.0", {"start": v(13.16, 17.7) * mm, "mid": v(12.45, 15.5) * mm, "end": v(12.92, 13.24) * mm});
            skArc(sketch, "E88.10.1", {"start": v(10.63, 19.32) * mm, "mid": v(8.93, 17.76) * mm, "end": v(6.67, 17.25) * mm});
            skLineSegment(sketch, "E88.10.2", {"start": v(10.63, 19.32) * mm, "end": v(13.16, 17.7) * mm});
            skCircle(sketch, "E89", {"center": v(0, 0) * mm, "radius": 17.5 * mm});
            skSolve(sketch);
        }
        {
            var Q0;
            Q0 = qSketchRegion(id + "F39", true);
            extrude(context, id + "F40", {"entities" : qUnion([Q0]), "operationType" : NewBodyOperationType.ADD, "depth" : 1.5 * mm, "offsetDistance" : 25 * mm});
        }
        {
            var Q0;
            Q0=makeQuery(id+"F7.opExtrude","SWEPT_FACE",FACE,{"disambiguationData":[OSD([sQuery(id+"F6.wireOp",EDGE,"E18")])]});
            var Q1;
            Q1=makeQuery(id+"F5.opExtrude","CAP_FACE",FACE,{"disambiguationData":[OSD([sQuery(id+"F4.wireOp",EDGE,"E11"),sQuery(id+"F4.wireOp",EDGE,"E12"),sQuery(id+"F4.wireOp",EDGE,"E13"),sQuery(id+"F4.wireOp",EDGE,"E14.MirrorCS"),sQuery(id+"F4.wireOp",EDGE,"E15.1.0"),sQuery(id+"F4.wireOp",EDGE,"E15.1.1"),sQuery(id+"F4.wireOp",EDGE,"E15.1.2"),sQuery(id+"F4.wireOp",EDGE,"E15.2.0"),sQuery(id+"F4.wireOp",EDGE,"E15.2.1"),sQuery(id+"F4.wireOp",EDGE,"E15.2.2"),sQuery(id+"F4.wireOp",EDGE,"E15.3.0"),sQuery(id+"F4.wireOp",EDGE,"E15.3.1"),sQuery(id+"F4.wireOp",EDGE,"E15.3.2"),sQuery(id+"F4.wireOp",EDGE,"E15.4.0"),sQuery(id+"F4.wireOp",EDGE,"E15.4.1"),sQuery(id+"F4.wireOp",EDGE,"E15.4.2"),sQuery(id+"F4.wireOp",EDGE,"E15.5.0"),sQuery(id+"F4.wireOp",EDGE,"E15.5.1"),sQuery(id+"F4.wireOp",EDGE,"E15.5.2"),sQuery(id+"F4.wireOp",EDGE,"E15.6.0"),sQuery(id+"F4.wireOp",EDGE,"E15.6.1"),sQuery(id+"F4.wireOp",EDGE,"E15.6.2"),sQuery(id+"F4.wireOp",EDGE,"E15.7.0"),sQuery(id+"F4.wireOp",EDGE,"E15.7.1"),sQuery(id+"F4.wireOp",EDGE,"E15.7.2"),sQuery(id+"F4.wireOp",EDGE,"E15.8.0"),sQuery(id+"F4.wireOp",EDGE,"E15.8.1"),sQuery(id+"F4.wireOp",EDGE,"E15.8.2"),sQuery(id+"F4.wireOp",EDGE,"E15.9.0"),sQuery(id+"F4.wireOp",EDGE,"E15.9.1"),sQuery(id+"F4.wireOp",EDGE,"E15.9.2"),sQuery(id+"F4.wireOp",EDGE,"E15.10.0"),sQuery(id+"F4.wireOp",EDGE,"E15.10.1"),sQuery(id+"F4.wireOp",EDGE,"E15.10.2"),sQuery(id+"F4.wireOp",EDGE,"E15.11.0"),sQuery(id+"F4.wireOp",EDGE,"E15.11.1"),sQuery(id+"F4.wireOp",EDGE,"E15.11.2"),sQuery(id+"F4.wireOp",EDGE,"E15.12.0"),sQuery(id+"F4.wireOp",EDGE,"E15.12.1"),sQuery(id+"F4.wireOp",EDGE,"E15.12.2"),sQuery(id+"F4.wireOp",EDGE,"E15.13.0"),sQuery(id+"F4.wireOp",EDGE,"E15.13.1"),sQuery(id+"F4.wireOp",EDGE,"E15.13.2"),sQuery(id+"F4.wireOp",EDGE,"E15.14.0"),sQuery(id+"F4.wireOp",EDGE,"E15.14.1"),sQuery(id+"F4.wireOp",EDGE,"E15.14.2"),sQuery(id+"F4.wireOp",EDGE,"E15.15.0"),sQuery(id+"F4.wireOp",EDGE,"E15.15.1"),sQuery(id+"F4.wireOp",EDGE,"E15.15.2"),sQuery(id+"F4.wireOp",EDGE,"E15.16.0"),sQuery(id+"F4.wireOp",EDGE,"E15.16.1"),sQuery(id+"F4.wireOp",EDGE,"E15.16.2"),sQuery(id+"F4.wireOp",EDGE,"E15.17.0"),sQuery(id+"F4.wireOp",EDGE,"E15.17.1"),sQuery(id+"F4.wireOp",EDGE,"E15.17.2"),sQuery(id+"F4.wireOp",EDGE,"E15.18.0"),sQuery(id+"F4.wireOp",EDGE,"E15.18.1"),sQuery(id+"F4.wireOp",EDGE,"E15.18.2"),sQuery(id+"F4.wireOp",EDGE,"E15.19.0"),sQuery(id+"F4.wireOp",EDGE,"E15.19.1"),sQuery(id+"F4.wireOp",EDGE,"E15.19.2"),sQuery(id+"F4.wireOp",EDGE,"E15.20.0"),sQuery(id+"F4.wireOp",EDGE,"E15.20.1"),sQuery(id+"F4.wireOp",EDGE,"E15.20.2"),sQuery(id+"F4.wireOp",EDGE,"E15.21.0"),sQuery(id+"F4.wireOp",EDGE,"E15.21.1"),sQuery(id+"F4.wireOp",EDGE,"E15.21.2"),sQuery(id+"F4.wireOp",EDGE,"E15.22.0"),sQuery(id+"F4.wireOp",EDGE,"E15.22.1"),sQuery(id+"F4.wireOp",EDGE,"E15.22.2"),sQuery(id+"F4.wireOp",EDGE,"E16")])],"isStart":false});
            fillet(context, id + "F41", {"entities" : qUnion([Q0, Q1]), "radius" : .5 * mm, "tangentPropagation" : true, "allowEdgeOverflow" : false});
        }
        {
            var Q0;
            Q0=makeQuery(id+"F12.opExtrude","CAP_FACE",FACE,{"disambiguationData":[OSD([sQuery(id+"F11.wireOp",EDGE,"E19"),sQuery(id+"F11.wireOp",EDGE,"E20"),sQuery(id+"F11.wireOp",EDGE,"E22"),sQuery(id+"F11.wireOp",EDGE,"E23.MirrorCS"),sQuery(id+"F11.wireOp",EDGE,"E24"),sQuery(id+"F11.wireOp",EDGE,"E25.1.0"),sQuery(id+"F11.wireOp",EDGE,"E25.1.1"),sQuery(id+"F11.wireOp",EDGE,"E25.1.2"),sQuery(id+"F11.wireOp",EDGE,"E25.2.0"),sQuery(id+"F11.wireOp",EDGE,"E25.2.1"),sQuery(id+"F11.wireOp",EDGE,"E25.2.2"),sQuery(id+"F11.wireOp",EDGE,"E25.3.0"),sQuery(id+"F11.wireOp",EDGE,"E25.3.1"),sQuery(id+"F11.wireOp",EDGE,"E25.3.2"),sQuery(id+"F11.wireOp",EDGE,"E25.4.0"),sQuery(id+"F11.wireOp",EDGE,"E25.4.1"),sQuery(id+"F11.wireOp",EDGE,"E25.4.2"),sQuery(id+"F11.wireOp",EDGE,"E25.5.0"),sQuery(id+"F11.wireOp",EDGE,"E25.5.1"),sQuery(id+"F11.wireOp",EDGE,"E25.5.2"),sQuery(id+"F11.wireOp",EDGE,"E25.6.0"),sQuery(id+"F11.wireOp",EDGE,"E25.6.1"),sQuery(id+"F11.wireOp",EDGE,"E25.6.2"),sQuery(id+"F11.wireOp",EDGE,"E25.7.0"),sQuery(id+"F11.wireOp",EDGE,"E25.7.1"),sQuery(id+"F11.wireOp",EDGE,"E25.7.2"),sQuery(id+"F11.wireOp",EDGE,"E25.8.0"),sQuery(id+"F11.wireOp",EDGE,"E25.8.1"),sQuery(id+"F11.wireOp",EDGE,"E25.8.2"),sQuery(id+"F11.wireOp",EDGE,"E25.9.0"),sQuery(id+"F11.wireOp",EDGE,"E25.9.1"),sQuery(id+"F11.wireOp",EDGE,"E25.9.2"),sQuery(id+"F11.wireOp",EDGE,"E25.10.0"),sQuery(id+"F11.wireOp",EDGE,"E25.10.1"),sQuery(id+"F11.wireOp",EDGE,"E25.10.2"),sQuery(id+"F11.wireOp",EDGE,"E25.11.0"),sQuery(id+"F11.wireOp",EDGE,"E25.11.1"),sQuery(id+"F11.wireOp",EDGE,"E25.11.2"),sQuery(id+"F11.wireOp",EDGE,"E25.12.0"),sQuery(id+"F11.wireOp",EDGE,"E25.12.1"),sQuery(id+"F11.wireOp",EDGE,"E25.12.2"),sQuery(id+"F11.wireOp",EDGE,"E25.13.0"),sQuery(id+"F11.wireOp",EDGE,"E25.13.1"),sQuery(id+"F11.wireOp",EDGE,"E25.13.2"),sQuery(id+"F11.wireOp",EDGE,"E25.14.0"),sQuery(id+"F11.wireOp",EDGE,"E25.14.1"),sQuery(id+"F11.wireOp",EDGE,"E25.14.2"),sQuery(id+"F11.wireOp",EDGE,"E25.15.0"),sQuery(id+"F11.wireOp",EDGE,"E25.15.1"),sQuery(id+"F11.wireOp",EDGE,"E25.15.2"),sQuery(id+"F11.wireOp",EDGE,"E25.16.0"),sQuery(id+"F11.wireOp",EDGE,"E25.16.1"),sQuery(id+"F11.wireOp",EDGE,"E25.16.2"),sQuery(id+"F11.wireOp",EDGE,"E25.17.0"),sQuery(id+"F11.wireOp",EDGE,"E25.17.1"),sQuery(id+"F11.wireOp",EDGE,"E25.17.2"),sQuery(id+"F11.wireOp",EDGE,"E25.18.0"),sQuery(id+"F11.wireOp",EDGE,"E25.18.1"),sQuery(id+"F11.wireOp",EDGE,"E25.18.2"),sQuery(id+"F11.wireOp",EDGE,"E25.19.0"),sQuery(id+"F11.wireOp",EDGE,"E25.19.1"),sQuery(id+"F11.wireOp",EDGE,"E25.19.2"),sQuery(id+"F11.wireOp",EDGE,"E25.20.0"),sQuery(id+"F11.wireOp",EDGE,"E25.20.1"),sQuery(id+"F11.wireOp",EDGE,"E25.20.2")])],"isStart":true});
            var Q1;
            Q1=makeQuery(id+"F7.opExtrude","SWEPT_FACE",FACE,{"disambiguationData":[OSD([sQuery(id+"F6.wireOp",EDGE,"E18")])]});
            fillet(context, id + "F42", {"entities" : qUnion([Q0, Q1]), "radius" : .5 * mm, "tangentPropagation" : true, "allowEdgeOverflow" : false});
        }
        {
            var Q0;
            Q0=makeQuery(id+"F14.opExtrude","SWEPT_FACE",FACE,{"disambiguationData":[OSD([sQuery(id+"F13.wireOp",EDGE,"E26")])]});
            var Q1;
            Q1=makeQuery(id+"F12.opExtrude","CAP_FACE",FACE,{"disambiguationData":[OSD([sQuery(id+"F11.wireOp",EDGE,"E19"),sQuery(id+"F11.wireOp",EDGE,"E20"),sQuery(id+"F11.wireOp",EDGE,"E22"),sQuery(id+"F11.wireOp",EDGE,"E23.MirrorCS"),sQuery(id+"F11.wireOp",EDGE,"E24"),sQuery(id+"F11.wireOp",EDGE,"E25.1.0"),sQuery(id+"F11.wireOp",EDGE,"E25.1.1"),sQuery(id+"F11.wireOp",EDGE,"E25.1.2"),sQuery(id+"F11.wireOp",EDGE,"E25.2.0"),sQuery(id+"F11.wireOp",EDGE,"E25.2.1"),sQuery(id+"F11.wireOp",EDGE,"E25.2.2"),sQuery(id+"F11.wireOp",EDGE,"E25.3.0"),sQuery(id+"F11.wireOp",EDGE,"E25.3.1"),sQuery(id+"F11.wireOp",EDGE,"E25.3.2"),sQuery(id+"F11.wireOp",EDGE,"E25.4.0"),sQuery(id+"F11.wireOp",EDGE,"E25.4.1"),sQuery(id+"F11.wireOp",EDGE,"E25.4.2"),sQuery(id+"F11.wireOp",EDGE,"E25.5.0"),sQuery(id+"F11.wireOp",EDGE,"E25.5.1"),sQuery(id+"F11.wireOp",EDGE,"E25.5.2"),sQuery(id+"F11.wireOp",EDGE,"E25.6.0"),sQuery(id+"F11.wireOp",EDGE,"E25.6.1"),sQuery(id+"F11.wireOp",EDGE,"E25.6.2"),sQuery(id+"F11.wireOp",EDGE,"E25.7.0"),sQuery(id+"F11.wireOp",EDGE,"E25.7.1"),sQuery(id+"F11.wireOp",EDGE,"E25.7.2"),sQuery(id+"F11.wireOp",EDGE,"E25.8.0"),sQuery(id+"F11.wireOp",EDGE,"E25.8.1"),sQuery(id+"F11.wireOp",EDGE,"E25.8.2"),sQuery(id+"F11.wireOp",EDGE,"E25.9.0"),sQuery(id+"F11.wireOp",EDGE,"E25.9.1"),sQuery(id+"F11.wireOp",EDGE,"E25.9.2"),sQuery(id+"F11.wireOp",EDGE,"E25.10.0"),sQuery(id+"F11.wireOp",EDGE,"E25.10.1"),sQuery(id+"F11.wireOp",EDGE,"E25.10.2"),sQuery(id+"F11.wireOp",EDGE,"E25.11.0"),sQuery(id+"F11.wireOp",EDGE,"E25.11.1"),sQuery(id+"F11.wireOp",EDGE,"E25.11.2"),sQuery(id+"F11.wireOp",EDGE,"E25.12.0"),sQuery(id+"F11.wireOp",EDGE,"E25.12.1"),sQuery(id+"F11.wireOp",EDGE,"E25.12.2"),sQuery(id+"F11.wireOp",EDGE,"E25.13.0"),sQuery(id+"F11.wireOp",EDGE,"E25.13.1"),sQuery(id+"F11.wireOp",EDGE,"E25.13.2"),sQuery(id+"F11.wireOp",EDGE,"E25.14.0"),sQuery(id+"F11.wireOp",EDGE,"E25.14.1"),sQuery(id+"F11.wireOp",EDGE,"E25.14.2"),sQuery(id+"F11.wireOp",EDGE,"E25.15.0"),sQuery(id+"F11.wireOp",EDGE,"E25.15.1"),sQuery(id+"F11.wireOp",EDGE,"E25.15.2"),sQuery(id+"F11.wireOp",EDGE,"E25.16.0"),sQuery(id+"F11.wireOp",EDGE,"E25.16.1"),sQuery(id+"F11.wireOp",EDGE,"E25.16.2"),sQuery(id+"F11.wireOp",EDGE,"E25.17.0"),sQuery(id+"F11.wireOp",EDGE,"E25.17.1"),sQuery(id+"F11.wireOp",EDGE,"E25.17.2"),sQuery(id+"F11.wireOp",EDGE,"E25.18.0"),sQuery(id+"F11.wireOp",EDGE,"E25.18.1"),sQuery(id+"F11.wireOp",EDGE,"E25.18.2"),sQuery(id+"F11.wireOp",EDGE,"E25.19.0"),sQuery(id+"F11.wireOp",EDGE,"E25.19.1"),sQuery(id+"F11.wireOp",EDGE,"E25.19.2"),sQuery(id+"F11.wireOp",EDGE,"E25.20.0"),sQuery(id+"F11.wireOp",EDGE,"E25.20.1"),sQuery(id+"F11.wireOp",EDGE,"E25.20.2")])],"isStart":false});
            var Q2;
            Q2=makeQuery(id+"F16.opExtrude","CAP_FACE",FACE,{"disambiguationData":[OSD([sQuery(id+"F15.wireOp",EDGE,"E28"),sQuery(id+"F15.wireOp",EDGE,"E29"),sQuery(id+"F15.wireOp",EDGE,"E30"),sQuery(id+"F15.wireOp",EDGE,"E32.MirrorCS"),sQuery(id+"F15.wireOp",EDGE,"E31"),sQuery(id+"F15.wireOp",EDGE,"E33.1.0"),sQuery(id+"F15.wireOp",EDGE,"E33.1.1"),sQuery(id+"F15.wireOp",EDGE,"E33.1.2"),sQuery(id+"F15.wireOp",EDGE,"E33.2.0"),sQuery(id+"F15.wireOp",EDGE,"E33.2.1"),sQuery(id+"F15.wireOp",EDGE,"E33.2.2"),sQuery(id+"F15.wireOp",EDGE,"E33.3.0"),sQuery(id+"F15.wireOp",EDGE,"E33.3.1"),sQuery(id+"F15.wireOp",EDGE,"E33.3.2"),sQuery(id+"F15.wireOp",EDGE,"E33.4.0"),sQuery(id+"F15.wireOp",EDGE,"E33.4.1"),sQuery(id+"F15.wireOp",EDGE,"E33.4.2"),sQuery(id+"F15.wireOp",EDGE,"E33.5.0"),sQuery(id+"F15.wireOp",EDGE,"E33.5.1"),sQuery(id+"F15.wireOp",EDGE,"E33.5.2"),sQuery(id+"F15.wireOp",EDGE,"E33.6.0"),sQuery(id+"F15.wireOp",EDGE,"E33.6.1"),sQuery(id+"F15.wireOp",EDGE,"E33.6.2"),sQuery(id+"F15.wireOp",EDGE,"E33.7.0"),sQuery(id+"F15.wireOp",EDGE,"E33.7.1"),sQuery(id+"F15.wireOp",EDGE,"E33.7.2"),sQuery(id+"F15.wireOp",EDGE,"E33.8.0"),sQuery(id+"F15.wireOp",EDGE,"E33.8.1"),sQuery(id+"F15.wireOp",EDGE,"E33.8.2"),sQuery(id+"F15.wireOp",EDGE,"E33.9.0"),sQuery(id+"F15.wireOp",EDGE,"E33.9.1"),sQuery(id+"F15.wireOp",EDGE,"E33.9.2"),sQuery(id+"F15.wireOp",EDGE,"E33.10.0"),sQuery(id+"F15.wireOp",EDGE,"E33.10.1"),sQuery(id+"F15.wireOp",EDGE,"E33.10.2"),sQuery(id+"F15.wireOp",EDGE,"E33.11.0"),sQuery(id+"F15.wireOp",EDGE,"E33.11.1"),sQuery(id+"F15.wireOp",EDGE,"E33.11.2"),sQuery(id+"F15.wireOp",EDGE,"E33.12.0"),sQuery(id+"F15.wireOp",EDGE,"E33.12.1"),sQuery(id+"F15.wireOp",EDGE,"E33.12.2"),sQuery(id+"F15.wireOp",EDGE,"E33.13.0"),sQuery(id+"F15.wireOp",EDGE,"E33.13.1"),sQuery(id+"F15.wireOp",EDGE,"E33.13.2"),sQuery(id+"F15.wireOp",EDGE,"E33.14.0"),sQuery(id+"F15.wireOp",EDGE,"E33.14.1"),sQuery(id+"F15.wireOp",EDGE,"E33.14.2"),sQuery(id+"F15.wireOp",EDGE,"E33.15.0"),sQuery(id+"F15.wireOp",EDGE,"E33.15.1"),sQuery(id+"F15.wireOp",EDGE,"E33.15.2"),sQuery(id+"F15.wireOp",EDGE,"E33.16.0"),sQuery(id+"F15.wireOp",EDGE,"E33.16.1"),sQuery(id+"F15.wireOp",EDGE,"E33.16.2"),sQuery(id+"F15.wireOp",EDGE,"E33.17.0"),sQuery(id+"F15.wireOp",EDGE,"E33.17.1"),sQuery(id+"F15.wireOp",EDGE,"E33.17.2"),sQuery(id+"F15.wireOp",EDGE,"E33.18.0"),sQuery(id+"F15.wireOp",EDGE,"E33.18.1"),sQuery(id+"F15.wireOp",EDGE,"E33.18.2"),sQuery(id+"F15.wireOp",EDGE,"E34")])],"isStart":true});
            fillet(context, id + "F43", {"entities" : qUnion([Q0, Q1, Q2]), "radius" : .5 * mm, "tangentPropagation" : true, "allowEdgeOverflow" : false});
        }
        {
            var Q0;
            Q0=makeQuery(id+"F20.opExtrude","CAP_FACE",FACE,{"disambiguationData":[OSD([sQuery(id+"F19.wireOp",EDGE,"E37"),sQuery(id+"F19.wireOp",EDGE,"E38"),sQuery(id+"F19.wireOp",EDGE,"E40"),sQuery(id+"F19.wireOp",EDGE,"E41.MirrorCS"),sQuery(id+"F19.wireOp",EDGE,"E42.1.0"),sQuery(id+"F19.wireOp",EDGE,"E42.1.1"),sQuery(id+"F19.wireOp",EDGE,"E42.1.2"),sQuery(id+"F19.wireOp",EDGE,"E42.2.0"),sQuery(id+"F19.wireOp",EDGE,"E42.2.1"),sQuery(id+"F19.wireOp",EDGE,"E42.2.2"),sQuery(id+"F19.wireOp",EDGE,"E42.3.0"),sQuery(id+"F19.wireOp",EDGE,"E42.3.1"),sQuery(id+"F19.wireOp",EDGE,"E42.3.2"),sQuery(id+"F19.wireOp",EDGE,"E42.4.0"),sQuery(id+"F19.wireOp",EDGE,"E42.4.1"),sQuery(id+"F19.wireOp",EDGE,"E42.4.2"),sQuery(id+"F19.wireOp",EDGE,"E42.5.0"),sQuery(id+"F19.wireOp",EDGE,"E42.5.1"),sQuery(id+"F19.wireOp",EDGE,"E42.5.2"),sQuery(id+"F19.wireOp",EDGE,"E42.6.0"),sQuery(id+"F19.wireOp",EDGE,"E42.6.1"),sQuery(id+"F19.wireOp",EDGE,"E42.6.2"),sQuery(id+"F19.wireOp",EDGE,"E42.7.0"),sQuery(id+"F19.wireOp",EDGE,"E42.7.1"),sQuery(id+"F19.wireOp",EDGE,"E42.7.2"),sQuery(id+"F19.wireOp",EDGE,"E42.8.0"),sQuery(id+"F19.wireOp",EDGE,"E42.8.1"),sQuery(id+"F19.wireOp",EDGE,"E42.8.2"),sQuery(id+"F19.wireOp",EDGE,"E42.9.0"),sQuery(id+"F19.wireOp",EDGE,"E42.9.1"),sQuery(id+"F19.wireOp",EDGE,"E42.9.2"),sQuery(id+"F19.wireOp",EDGE,"E42.10.0"),sQuery(id+"F19.wireOp",EDGE,"E42.10.1"),sQuery(id+"F19.wireOp",EDGE,"E42.10.2"),sQuery(id+"F19.wireOp",EDGE,"E42.11.0"),sQuery(id+"F19.wireOp",EDGE,"E42.11.1"),sQuery(id+"F19.wireOp",EDGE,"E42.11.2"),sQuery(id+"F19.wireOp",EDGE,"E42.12.0"),sQuery(id+"F19.wireOp",EDGE,"E42.12.1"),sQuery(id+"F19.wireOp",EDGE,"E42.12.2"),sQuery(id+"F19.wireOp",EDGE,"E42.13.0"),sQuery(id+"F19.wireOp",EDGE,"E42.13.1"),sQuery(id+"F19.wireOp",EDGE,"E42.13.2"),sQuery(id+"F19.wireOp",EDGE,"E42.14.0"),sQuery(id+"F19.wireOp",EDGE,"E42.14.1"),sQuery(id+"F19.wireOp",EDGE,"E42.14.2"),sQuery(id+"F19.wireOp",EDGE,"E42.15.0"),sQuery(id+"F19.wireOp",EDGE,"E42.15.1"),sQuery(id+"F19.wireOp",EDGE,"E42.15.2"),sQuery(id+"F19.wireOp",EDGE,"E42.16.0"),sQuery(id+"F19.wireOp",EDGE,"E42.16.1"),sQuery(id+"F19.wireOp",EDGE,"E42.16.2"),sQuery(id+"F19.wireOp",EDGE,"E43")])],"isStart":true});
            var Q1;
            Q1=makeQuery(id+"F18.opExtrude","SWEPT_FACE",FACE,{"disambiguationData":[OSD([sQuery(id+"F17.wireOp",EDGE,"E36")])]});
            var Q2;
            Q2=makeQuery(id+"F16.opExtrude","CAP_FACE",FACE,{"disambiguationData":[OSD([sQuery(id+"F15.wireOp",EDGE,"E28"),sQuery(id+"F15.wireOp",EDGE,"E29"),sQuery(id+"F15.wireOp",EDGE,"E30"),sQuery(id+"F15.wireOp",EDGE,"E32.MirrorCS"),sQuery(id+"F15.wireOp",EDGE,"E31"),sQuery(id+"F15.wireOp",EDGE,"E33.1.0"),sQuery(id+"F15.wireOp",EDGE,"E33.1.1"),sQuery(id+"F15.wireOp",EDGE,"E33.1.2"),sQuery(id+"F15.wireOp",EDGE,"E33.2.0"),sQuery(id+"F15.wireOp",EDGE,"E33.2.1"),sQuery(id+"F15.wireOp",EDGE,"E33.2.2"),sQuery(id+"F15.wireOp",EDGE,"E33.3.0"),sQuery(id+"F15.wireOp",EDGE,"E33.3.1"),sQuery(id+"F15.wireOp",EDGE,"E33.3.2"),sQuery(id+"F15.wireOp",EDGE,"E33.4.0"),sQuery(id+"F15.wireOp",EDGE,"E33.4.1"),sQuery(id+"F15.wireOp",EDGE,"E33.4.2"),sQuery(id+"F15.wireOp",EDGE,"E33.5.0"),sQuery(id+"F15.wireOp",EDGE,"E33.5.1"),sQuery(id+"F15.wireOp",EDGE,"E33.5.2"),sQuery(id+"F15.wireOp",EDGE,"E33.6.0"),sQuery(id+"F15.wireOp",EDGE,"E33.6.1"),sQuery(id+"F15.wireOp",EDGE,"E33.6.2"),sQuery(id+"F15.wireOp",EDGE,"E33.7.0"),sQuery(id+"F15.wireOp",EDGE,"E33.7.1"),sQuery(id+"F15.wireOp",EDGE,"E33.7.2"),sQuery(id+"F15.wireOp",EDGE,"E33.8.0"),sQuery(id+"F15.wireOp",EDGE,"E33.8.1"),sQuery(id+"F15.wireOp",EDGE,"E33.8.2"),sQuery(id+"F15.wireOp",EDGE,"E33.9.0"),sQuery(id+"F15.wireOp",EDGE,"E33.9.1"),sQuery(id+"F15.wireOp",EDGE,"E33.9.2"),sQuery(id+"F15.wireOp",EDGE,"E33.10.0"),sQuery(id+"F15.wireOp",EDGE,"E33.10.1"),sQuery(id+"F15.wireOp",EDGE,"E33.10.2"),sQuery(id+"F15.wireOp",EDGE,"E33.11.0"),sQuery(id+"F15.wireOp",EDGE,"E33.11.1"),sQuery(id+"F15.wireOp",EDGE,"E33.11.2"),sQuery(id+"F15.wireOp",EDGE,"E33.12.0"),sQuery(id+"F15.wireOp",EDGE,"E33.12.1"),sQuery(id+"F15.wireOp",EDGE,"E33.12.2"),sQuery(id+"F15.wireOp",EDGE,"E33.13.0"),sQuery(id+"F15.wireOp",EDGE,"E33.13.1"),sQuery(id+"F15.wireOp",EDGE,"E33.13.2"),sQuery(id+"F15.wireOp",EDGE,"E33.14.0"),sQuery(id+"F15.wireOp",EDGE,"E33.14.1"),sQuery(id+"F15.wireOp",EDGE,"E33.14.2"),sQuery(id+"F15.wireOp",EDGE,"E33.15.0"),sQuery(id+"F15.wireOp",EDGE,"E33.15.1"),sQuery(id+"F15.wireOp",EDGE,"E33.15.2"),sQuery(id+"F15.wireOp",EDGE,"E33.16.0"),sQuery(id+"F15.wireOp",EDGE,"E33.16.1"),sQuery(id+"F15.wireOp",EDGE,"E33.16.2"),sQuery(id+"F15.wireOp",EDGE,"E33.17.0"),sQuery(id+"F15.wireOp",EDGE,"E33.17.1"),sQuery(id+"F15.wireOp",EDGE,"E33.17.2"),sQuery(id+"F15.wireOp",EDGE,"E33.18.0"),sQuery(id+"F15.wireOp",EDGE,"E33.18.1"),sQuery(id+"F15.wireOp",EDGE,"E33.18.2"),sQuery(id+"F15.wireOp",EDGE,"E34")])],"isStart":false});
            fillet(context, id + "F44", {"entities" : qUnion([Q0, Q1, Q2]), "radius" : .5 * mm, "tangentPropagation" : true, "allowEdgeOverflow" : false});
        }
        {
            var Q0;
            Q0=makeQuery(id+"F22.opExtrude","SWEPT_FACE",FACE,{"disambiguationData":[OSD([sQuery(id+"F21.wireOp",EDGE,"E45")])]});
            var Q1;
            Q1=makeQuery(id+"F24.opExtrude","CAP_FACE",FACE,{"disambiguationData":[OSD([sQuery(id+"F23.wireOp",EDGE,"E46"),sQuery(id+"F23.wireOp",EDGE,"E50.MirrorCS"),sQuery(id+"F23.wireOp",EDGE,"E49"),sQuery(id+"F23.wireOp",EDGE,"E51.MirrorCS"),sQuery(id+"F23.wireOp",EDGE,"E52.1.0"),sQuery(id+"F23.wireOp",EDGE,"E52.1.1"),sQuery(id+"F23.wireOp",EDGE,"E52.1.2"),sQuery(id+"F23.wireOp",EDGE,"E52.2.0"),sQuery(id+"F23.wireOp",EDGE,"E52.2.1"),sQuery(id+"F23.wireOp",EDGE,"E52.2.2"),sQuery(id+"F23.wireOp",EDGE,"E52.3.0"),sQuery(id+"F23.wireOp",EDGE,"E52.3.1"),sQuery(id+"F23.wireOp",EDGE,"E52.3.2"),sQuery(id+"F23.wireOp",EDGE,"E52.4.0"),sQuery(id+"F23.wireOp",EDGE,"E52.4.1"),sQuery(id+"F23.wireOp",EDGE,"E52.4.2"),sQuery(id+"F23.wireOp",EDGE,"E52.5.0"),sQuery(id+"F23.wireOp",EDGE,"E52.5.1"),sQuery(id+"F23.wireOp",EDGE,"E52.5.2"),sQuery(id+"F23.wireOp",EDGE,"E52.6.0"),sQuery(id+"F23.wireOp",EDGE,"E52.6.1"),sQuery(id+"F23.wireOp",EDGE,"E52.6.2"),sQuery(id+"F23.wireOp",EDGE,"E52.7.0"),sQuery(id+"F23.wireOp",EDGE,"E52.7.1"),sQuery(id+"F23.wireOp",EDGE,"E52.7.2"),sQuery(id+"F23.wireOp",EDGE,"E52.8.0"),sQuery(id+"F23.wireOp",EDGE,"E52.8.1"),sQuery(id+"F23.wireOp",EDGE,"E52.8.2"),sQuery(id+"F23.wireOp",EDGE,"E52.9.0"),sQuery(id+"F23.wireOp",EDGE,"E52.9.1"),sQuery(id+"F23.wireOp",EDGE,"E52.9.2"),sQuery(id+"F23.wireOp",EDGE,"E52.10.0"),sQuery(id+"F23.wireOp",EDGE,"E52.10.1"),sQuery(id+"F23.wireOp",EDGE,"E52.10.2"),sQuery(id+"F23.wireOp",EDGE,"E52.11.0"),sQuery(id+"F23.wireOp",EDGE,"E52.11.1"),sQuery(id+"F23.wireOp",EDGE,"E52.11.2"),sQuery(id+"F23.wireOp",EDGE,"E52.12.0"),sQuery(id+"F23.wireOp",EDGE,"E52.12.1"),sQuery(id+"F23.wireOp",EDGE,"E52.12.2"),sQuery(id+"F23.wireOp",EDGE,"E52.13.0"),sQuery(id+"F23.wireOp",EDGE,"E52.13.1"),sQuery(id+"F23.wireOp",EDGE,"E52.13.2"),sQuery(id+"F23.wireOp",EDGE,"E52.14.0"),sQuery(id+"F23.wireOp",EDGE,"E52.14.1"),sQuery(id+"F23.wireOp",EDGE,"E52.14.2"),sQuery(id+"F23.wireOp",EDGE,"E53")])],"isStart":true});
            var Q2;
            Q2=makeQuery(id+"F20.opExtrude","CAP_FACE",FACE,{"disambiguationData":[OSD([sQuery(id+"F19.wireOp",EDGE,"E37"),sQuery(id+"F19.wireOp",EDGE,"E38"),sQuery(id+"F19.wireOp",EDGE,"E40"),sQuery(id+"F19.wireOp",EDGE,"E41.MirrorCS"),sQuery(id+"F19.wireOp",EDGE,"E42.1.0"),sQuery(id+"F19.wireOp",EDGE,"E42.1.1"),sQuery(id+"F19.wireOp",EDGE,"E42.1.2"),sQuery(id+"F19.wireOp",EDGE,"E42.2.0"),sQuery(id+"F19.wireOp",EDGE,"E42.2.1"),sQuery(id+"F19.wireOp",EDGE,"E42.2.2"),sQuery(id+"F19.wireOp",EDGE,"E42.3.0"),sQuery(id+"F19.wireOp",EDGE,"E42.3.1"),sQuery(id+"F19.wireOp",EDGE,"E42.3.2"),sQuery(id+"F19.wireOp",EDGE,"E42.4.0"),sQuery(id+"F19.wireOp",EDGE,"E42.4.1"),sQuery(id+"F19.wireOp",EDGE,"E42.4.2"),sQuery(id+"F19.wireOp",EDGE,"E42.5.0"),sQuery(id+"F19.wireOp",EDGE,"E42.5.1"),sQuery(id+"F19.wireOp",EDGE,"E42.5.2"),sQuery(id+"F19.wireOp",EDGE,"E42.6.0"),sQuery(id+"F19.wireOp",EDGE,"E42.6.1"),sQuery(id+"F19.wireOp",EDGE,"E42.6.2"),sQuery(id+"F19.wireOp",EDGE,"E42.7.0"),sQuery(id+"F19.wireOp",EDGE,"E42.7.1"),sQuery(id+"F19.wireOp",EDGE,"E42.7.2"),sQuery(id+"F19.wireOp",EDGE,"E42.8.0"),sQuery(id+"F19.wireOp",EDGE,"E42.8.1"),sQuery(id+"F19.wireOp",EDGE,"E42.8.2"),sQuery(id+"F19.wireOp",EDGE,"E42.9.0"),sQuery(id+"F19.wireOp",EDGE,"E42.9.1"),sQuery(id+"F19.wireOp",EDGE,"E42.9.2"),sQuery(id+"F19.wireOp",EDGE,"E42.10.0"),sQuery(id+"F19.wireOp",EDGE,"E42.10.1"),sQuery(id+"F19.wireOp",EDGE,"E42.10.2"),sQuery(id+"F19.wireOp",EDGE,"E42.11.0"),sQuery(id+"F19.wireOp",EDGE,"E42.11.1"),sQuery(id+"F19.wireOp",EDGE,"E42.11.2"),sQuery(id+"F19.wireOp",EDGE,"E42.12.0"),sQuery(id+"F19.wireOp",EDGE,"E42.12.1"),sQuery(id+"F19.wireOp",EDGE,"E42.12.2"),sQuery(id+"F19.wireOp",EDGE,"E42.13.0"),sQuery(id+"F19.wireOp",EDGE,"E42.13.1"),sQuery(id+"F19.wireOp",EDGE,"E42.13.2"),sQuery(id+"F19.wireOp",EDGE,"E42.14.0"),sQuery(id+"F19.wireOp",EDGE,"E42.14.1"),sQuery(id+"F19.wireOp",EDGE,"E42.14.2"),sQuery(id+"F19.wireOp",EDGE,"E42.15.0"),sQuery(id+"F19.wireOp",EDGE,"E42.15.1"),sQuery(id+"F19.wireOp",EDGE,"E42.15.2"),sQuery(id+"F19.wireOp",EDGE,"E42.16.0"),sQuery(id+"F19.wireOp",EDGE,"E42.16.1"),sQuery(id+"F19.wireOp",EDGE,"E42.16.2"),sQuery(id+"F19.wireOp",EDGE,"E43")])],"isStart":false});
            fillet(context, id + "F45", {"entities" : qUnion([Q0, Q1, Q2]), "radius" : .5 * mm, "tangentPropagation" : true, "allowEdgeOverflow" : false});
        }
        {
            var Q0;
            Q0=makeQuery(id+"F26.opExtrude","SWEPT_FACE",FACE,{"disambiguationData":[OSD([sQuery(id+"F25.wireOp",EDGE,"E55")])]});
            var Q1;
            Q1=makeQuery(id+"F24.opExtrude","CAP_FACE",FACE,{"disambiguationData":[OSD([sQuery(id+"F23.wireOp",EDGE,"E46"),sQuery(id+"F23.wireOp",EDGE,"E50.MirrorCS"),sQuery(id+"F23.wireOp",EDGE,"E49"),sQuery(id+"F23.wireOp",EDGE,"E51.MirrorCS"),sQuery(id+"F23.wireOp",EDGE,"E52.1.0"),sQuery(id+"F23.wireOp",EDGE,"E52.1.1"),sQuery(id+"F23.wireOp",EDGE,"E52.1.2"),sQuery(id+"F23.wireOp",EDGE,"E52.2.0"),sQuery(id+"F23.wireOp",EDGE,"E52.2.1"),sQuery(id+"F23.wireOp",EDGE,"E52.2.2"),sQuery(id+"F23.wireOp",EDGE,"E52.3.0"),sQuery(id+"F23.wireOp",EDGE,"E52.3.1"),sQuery(id+"F23.wireOp",EDGE,"E52.3.2"),sQuery(id+"F23.wireOp",EDGE,"E52.4.0"),sQuery(id+"F23.wireOp",EDGE,"E52.4.1"),sQuery(id+"F23.wireOp",EDGE,"E52.4.2"),sQuery(id+"F23.wireOp",EDGE,"E52.5.0"),sQuery(id+"F23.wireOp",EDGE,"E52.5.1"),sQuery(id+"F23.wireOp",EDGE,"E52.5.2"),sQuery(id+"F23.wireOp",EDGE,"E52.6.0"),sQuery(id+"F23.wireOp",EDGE,"E52.6.1"),sQuery(id+"F23.wireOp",EDGE,"E52.6.2"),sQuery(id+"F23.wireOp",EDGE,"E52.7.0"),sQuery(id+"F23.wireOp",EDGE,"E52.7.1"),sQuery(id+"F23.wireOp",EDGE,"E52.7.2"),sQuery(id+"F23.wireOp",EDGE,"E52.8.0"),sQuery(id+"F23.wireOp",EDGE,"E52.8.1"),sQuery(id+"F23.wireOp",EDGE,"E52.8.2"),sQuery(id+"F23.wireOp",EDGE,"E52.9.0"),sQuery(id+"F23.wireOp",EDGE,"E52.9.1"),sQuery(id+"F23.wireOp",EDGE,"E52.9.2"),sQuery(id+"F23.wireOp",EDGE,"E52.10.0"),sQuery(id+"F23.wireOp",EDGE,"E52.10.1"),sQuery(id+"F23.wireOp",EDGE,"E52.10.2"),sQuery(id+"F23.wireOp",EDGE,"E52.11.0"),sQuery(id+"F23.wireOp",EDGE,"E52.11.1"),sQuery(id+"F23.wireOp",EDGE,"E52.11.2"),sQuery(id+"F23.wireOp",EDGE,"E52.12.0"),sQuery(id+"F23.wireOp",EDGE,"E52.12.1"),sQuery(id+"F23.wireOp",EDGE,"E52.12.2"),sQuery(id+"F23.wireOp",EDGE,"E52.13.0"),sQuery(id+"F23.wireOp",EDGE,"E52.13.1"),sQuery(id+"F23.wireOp",EDGE,"E52.13.2"),sQuery(id+"F23.wireOp",EDGE,"E52.14.0"),sQuery(id+"F23.wireOp",EDGE,"E52.14.1"),sQuery(id+"F23.wireOp",EDGE,"E52.14.2"),sQuery(id+"F23.wireOp",EDGE,"E53")])],"isStart":false});
            var Q2;
            Q2=makeQuery(id+"F28.opExtrude","CAP_FACE",FACE,{"disambiguationData":[OSD([sQuery(id+"F27.wireOp",EDGE,"E56"),sQuery(id+"F27.wireOp",EDGE,"E57"),sQuery(id+"F27.wireOp",EDGE,"E59"),sQuery(id+"F27.wireOp",EDGE,"E60.MirrorCS"),sQuery(id+"F27.wireOp",EDGE,"E61.1.0"),sQuery(id+"F27.wireOp",EDGE,"E61.1.1"),sQuery(id+"F27.wireOp",EDGE,"E61.1.2"),sQuery(id+"F27.wireOp",EDGE,"E61.2.0"),sQuery(id+"F27.wireOp",EDGE,"E61.2.1"),sQuery(id+"F27.wireOp",EDGE,"E61.2.2"),sQuery(id+"F27.wireOp",EDGE,"E61.3.0"),sQuery(id+"F27.wireOp",EDGE,"E61.3.1"),sQuery(id+"F27.wireOp",EDGE,"E61.3.2"),sQuery(id+"F27.wireOp",EDGE,"E61.4.0"),sQuery(id+"F27.wireOp",EDGE,"E61.4.1"),sQuery(id+"F27.wireOp",EDGE,"E61.4.2"),sQuery(id+"F27.wireOp",EDGE,"E61.5.0"),sQuery(id+"F27.wireOp",EDGE,"E61.5.1"),sQuery(id+"F27.wireOp",EDGE,"E61.5.2"),sQuery(id+"F27.wireOp",EDGE,"E61.6.0"),sQuery(id+"F27.wireOp",EDGE,"E61.6.1"),sQuery(id+"F27.wireOp",EDGE,"E61.6.2"),sQuery(id+"F27.wireOp",EDGE,"E61.7.0"),sQuery(id+"F27.wireOp",EDGE,"E61.7.1"),sQuery(id+"F27.wireOp",EDGE,"E61.7.2"),sQuery(id+"F27.wireOp",EDGE,"E61.8.0"),sQuery(id+"F27.wireOp",EDGE,"E61.8.1"),sQuery(id+"F27.wireOp",EDGE,"E61.8.2"),sQuery(id+"F27.wireOp",EDGE,"E61.9.0"),sQuery(id+"F27.wireOp",EDGE,"E61.9.1"),sQuery(id+"F27.wireOp",EDGE,"E61.9.2"),sQuery(id+"F27.wireOp",EDGE,"E61.10.0"),sQuery(id+"F27.wireOp",EDGE,"E61.10.1"),sQuery(id+"F27.wireOp",EDGE,"E61.10.2"),sQuery(id+"F27.wireOp",EDGE,"E61.11.0"),sQuery(id+"F27.wireOp",EDGE,"E61.11.1"),sQuery(id+"F27.wireOp",EDGE,"E61.11.2"),sQuery(id+"F27.wireOp",EDGE,"E61.12.0"),sQuery(id+"F27.wireOp",EDGE,"E61.12.1"),sQuery(id+"F27.wireOp",EDGE,"E61.12.2"),sQuery(id+"F27.wireOp",EDGE,"E61.13.0"),sQuery(id+"F27.wireOp",EDGE,"E61.13.1"),sQuery(id+"F27.wireOp",EDGE,"E61.13.2"),sQuery(id+"F27.wireOp",EDGE,"E62")])],"isStart":true});
            fillet(context, id + "F46", {"entities" : qUnion([Q0, Q1, Q2]), "radius" : .5 * mm, "tangentPropagation" : true, "allowEdgeOverflow" : false});
        }
        {
            var Q0;
            Q0=makeQuery(id+"F28.opExtrude","CAP_FACE",FACE,{"disambiguationData":[OSD([sQuery(id+"F27.wireOp",EDGE,"E56"),sQuery(id+"F27.wireOp",EDGE,"E57"),sQuery(id+"F27.wireOp",EDGE,"E59"),sQuery(id+"F27.wireOp",EDGE,"E60.MirrorCS"),sQuery(id+"F27.wireOp",EDGE,"E61.1.0"),sQuery(id+"F27.wireOp",EDGE,"E61.1.1"),sQuery(id+"F27.wireOp",EDGE,"E61.1.2"),sQuery(id+"F27.wireOp",EDGE,"E61.2.0"),sQuery(id+"F27.wireOp",EDGE,"E61.2.1"),sQuery(id+"F27.wireOp",EDGE,"E61.2.2"),sQuery(id+"F27.wireOp",EDGE,"E61.3.0"),sQuery(id+"F27.wireOp",EDGE,"E61.3.1"),sQuery(id+"F27.wireOp",EDGE,"E61.3.2"),sQuery(id+"F27.wireOp",EDGE,"E61.4.0"),sQuery(id+"F27.wireOp",EDGE,"E61.4.1"),sQuery(id+"F27.wireOp",EDGE,"E61.4.2"),sQuery(id+"F27.wireOp",EDGE,"E61.5.0"),sQuery(id+"F27.wireOp",EDGE,"E61.5.1"),sQuery(id+"F27.wireOp",EDGE,"E61.5.2"),sQuery(id+"F27.wireOp",EDGE,"E61.6.0"),sQuery(id+"F27.wireOp",EDGE,"E61.6.1"),sQuery(id+"F27.wireOp",EDGE,"E61.6.2"),sQuery(id+"F27.wireOp",EDGE,"E61.7.0"),sQuery(id+"F27.wireOp",EDGE,"E61.7.1"),sQuery(id+"F27.wireOp",EDGE,"E61.7.2"),sQuery(id+"F27.wireOp",EDGE,"E61.8.0"),sQuery(id+"F27.wireOp",EDGE,"E61.8.1"),sQuery(id+"F27.wireOp",EDGE,"E61.8.2"),sQuery(id+"F27.wireOp",EDGE,"E61.9.0"),sQuery(id+"F27.wireOp",EDGE,"E61.9.1"),sQuery(id+"F27.wireOp",EDGE,"E61.9.2"),sQuery(id+"F27.wireOp",EDGE,"E61.10.0"),sQuery(id+"F27.wireOp",EDGE,"E61.10.1"),sQuery(id+"F27.wireOp",EDGE,"E61.10.2"),sQuery(id+"F27.wireOp",EDGE,"E61.11.0"),sQuery(id+"F27.wireOp",EDGE,"E61.11.1"),sQuery(id+"F27.wireOp",EDGE,"E61.11.2"),sQuery(id+"F27.wireOp",EDGE,"E61.12.0"),sQuery(id+"F27.wireOp",EDGE,"E61.12.1"),sQuery(id+"F27.wireOp",EDGE,"E61.12.2"),sQuery(id+"F27.wireOp",EDGE,"E61.13.0"),sQuery(id+"F27.wireOp",EDGE,"E61.13.1"),sQuery(id+"F27.wireOp",EDGE,"E61.13.2"),sQuery(id+"F27.wireOp",EDGE,"E62")])],"isStart":false});
            var Q1;
            Q1=makeQuery(id+"F30.opExtrude","SWEPT_FACE",FACE,{"disambiguationData":[OSD([sQuery(id+"F29.wireOp",EDGE,"E64")])]});
            var Q2;
            Q2=makeQuery(id+"F32.opExtrude","CAP_FACE",FACE,{"disambiguationData":[OSD([sQuery(id+"F31.wireOp",EDGE,"E65"),sQuery(id+"F31.wireOp",EDGE,"E66"),sQuery(id+"F31.wireOp",EDGE,"E68"),sQuery(id+"F31.wireOp",EDGE,"E69.MirrorCS"),sQuery(id+"F31.wireOp",EDGE,"E70"),sQuery(id+"F31.wireOp",EDGE,"E71.1.0"),sQuery(id+"F31.wireOp",EDGE,"E71.1.1"),sQuery(id+"F31.wireOp",EDGE,"E71.1.2"),sQuery(id+"F31.wireOp",EDGE,"E71.2.0"),sQuery(id+"F31.wireOp",EDGE,"E71.2.1"),sQuery(id+"F31.wireOp",EDGE,"E71.2.2"),sQuery(id+"F31.wireOp",EDGE,"E71.3.0"),sQuery(id+"F31.wireOp",EDGE,"E71.3.1"),sQuery(id+"F31.wireOp",EDGE,"E71.3.2"),sQuery(id+"F31.wireOp",EDGE,"E71.4.0"),sQuery(id+"F31.wireOp",EDGE,"E71.4.1"),sQuery(id+"F31.wireOp",EDGE,"E71.4.2"),sQuery(id+"F31.wireOp",EDGE,"E71.5.0"),sQuery(id+"F31.wireOp",EDGE,"E71.5.1"),sQuery(id+"F31.wireOp",EDGE,"E71.5.2"),sQuery(id+"F31.wireOp",EDGE,"E71.6.0"),sQuery(id+"F31.wireOp",EDGE,"E71.6.1"),sQuery(id+"F31.wireOp",EDGE,"E71.6.2"),sQuery(id+"F31.wireOp",EDGE,"E71.7.0"),sQuery(id+"F31.wireOp",EDGE,"E71.7.1"),sQuery(id+"F31.wireOp",EDGE,"E71.7.2"),sQuery(id+"F31.wireOp",EDGE,"E71.8.0"),sQuery(id+"F31.wireOp",EDGE,"E71.8.1"),sQuery(id+"F31.wireOp",EDGE,"E71.8.2"),sQuery(id+"F31.wireOp",EDGE,"E71.9.0"),sQuery(id+"F31.wireOp",EDGE,"E71.9.1"),sQuery(id+"F31.wireOp",EDGE,"E71.9.2"),sQuery(id+"F31.wireOp",EDGE,"E71.10.0"),sQuery(id+"F31.wireOp",EDGE,"E71.10.1"),sQuery(id+"F31.wireOp",EDGE,"E71.10.2"),sQuery(id+"F31.wireOp",EDGE,"E71.11.0"),sQuery(id+"F31.wireOp",EDGE,"E71.11.1"),sQuery(id+"F31.wireOp",EDGE,"E71.11.2"),sQuery(id+"F31.wireOp",EDGE,"E71.12.0"),sQuery(id+"F31.wireOp",EDGE,"E71.12.1"),sQuery(id+"F31.wireOp",EDGE,"E71.12.2")])],"isStart":true});
            fillet(context, id + "F47", {"entities" : qUnion([Q0, Q1, Q2]), "radius" : .5 * mm, "tangentPropagation" : true, "allowEdgeOverflow" : false});
        }
        {
            var Q0;
            {var subQ0=sQuery(id+"F35.wireOp",EDGE,"E79.5.0");var subQ1=sQuery(id+"F35.wireOp",EDGE,"E74");var subQ2=sQuery(id+"F35.wireOp",EDGE,"E79.6.2");var subQ3=sQuery(id+"F35.wireOp",EDGE,"E79.3.0");var subQ4=sQuery(id+"F35.wireOp",EDGE,"E79.4.2");var subQ5=sQuery(id+"F35.wireOp",EDGE,"E79.5.2");var subQ6=sQuery(id+"F35.wireOp",EDGE,"E79.2.0");var subQ7=sQuery(id+"F35.wireOp",EDGE,"E79.3.2");var subQ8=sQuery(id+"F35.wireOp",EDGE,"E79.5.1");var subQ9=sQuery(id+"F35.wireOp",EDGE,"E79.1.0");var subQ10=sQuery(id+"F35.wireOp",EDGE,"E79.2.2");var subQ11=sQuery(id+"F35.wireOp",EDGE,"E78.MirrorCS");var subQ12=sQuery(id+"F35.wireOp",EDGE,"E79.1.2");var subQ13=sQuery(id+"F35.wireOp",EDGE,"E79.4.0");var subQ14=sQuery(id+"F35.wireOp",EDGE,"E79.8.0");var subQ15=sQuery(id+"F35.wireOp",EDGE,"E79.9.2");var subQ16=sQuery(id+"F35.wireOp",EDGE,"E77");var subQ17=sQuery(id+"F35.wireOp",EDGE,"E79.11.0");var subQ18=sQuery(id+"F35.wireOp",EDGE,"E79.9.0");var subQ19=sQuery(id+"F35.wireOp",EDGE,"E79.10.2");var subQ20=sQuery(id+"F35.wireOp",EDGE,"E79.10.0");var subQ21=sQuery(id+"F35.wireOp",EDGE,"E79.11.2");var subQ22=sQuery(id+"F35.wireOp",EDGE,"E79.6.0");var subQ23=sQuery(id+"F35.wireOp",EDGE,"E79.7.2");var subQ24=sQuery(id+"F35.wireOp",EDGE,"E79.7.0");var subQ25=sQuery(id+"F35.wireOp",EDGE,"E79.8.2");Q0=makeQuery(id+"F36.boolean.opBoolean","SPLIT",FACE,{"disambiguationData":[TD([makeQuery(id+"F36.opExtrude","SWEPT_FACE",FACE,{"disambiguationData":[OSD([subQ0])]})])],"derivedFrom":makeQuery(id+"F36.opExtrude","CAP_FACE",FACE,{"disambiguationData":[OSD([subQ1,sQuery(id+"F35.wireOp",EDGE,"E75"),subQ16,subQ11,subQ9,sQuery(id+"F35.wireOp",EDGE,"E79.1.1"),subQ12,subQ6,sQuery(id+"F35.wireOp",EDGE,"E79.2.1"),subQ10,subQ3,sQuery(id+"F35.wireOp",EDGE,"E79.3.1"),subQ7,subQ13,sQuery(id+"F35.wireOp",EDGE,"E79.4.1"),subQ4,subQ0,subQ8,subQ5,subQ22,sQuery(id+"F35.wireOp",EDGE,"E79.6.1"),subQ2,subQ24,sQuery(id+"F35.wireOp",EDGE,"E79.7.1"),subQ23,subQ14,sQuery(id+"F35.wireOp",EDGE,"E79.8.1"),subQ25,subQ18,sQuery(id+"F35.wireOp",EDGE,"E79.9.1"),subQ15,subQ20,sQuery(id+"F35.wireOp",EDGE,"E79.10.1"),subQ19,subQ17,sQuery(id+"F35.wireOp",EDGE,"E79.11.1"),subQ21,sQuery(id+"F35.wireOp",EDGE,"E80")])],"isStart":true})});}
            var Q1;
            {var subQ0=sQuery(id+"F35.wireOp",EDGE,"E79.5.0");var subQ1=sQuery(id+"F35.wireOp",EDGE,"E74");var subQ2=sQuery(id+"F35.wireOp",EDGE,"E79.6.2");var subQ3=sQuery(id+"F35.wireOp",EDGE,"E79.3.0");var subQ4=sQuery(id+"F35.wireOp",EDGE,"E79.4.2");var subQ5=sQuery(id+"F35.wireOp",EDGE,"E79.2.0");var subQ6=sQuery(id+"F35.wireOp",EDGE,"E79.3.2");var subQ7=sQuery(id+"F35.wireOp",EDGE,"E79.1.0");var subQ8=sQuery(id+"F35.wireOp",EDGE,"E79.2.2");var subQ9=sQuery(id+"F35.wireOp",EDGE,"E78.MirrorCS");var subQ10=sQuery(id+"F35.wireOp",EDGE,"E79.1.2");var subQ11=sQuery(id+"F35.wireOp",EDGE,"E79.4.0");var subQ12=sQuery(id+"F35.wireOp",EDGE,"E79.5.2");var subQ13=sQuery(id+"F35.wireOp",EDGE,"E79.8.0");var subQ14=sQuery(id+"F35.wireOp",EDGE,"E79.9.2");var subQ15=sQuery(id+"F35.wireOp",EDGE,"E77");var subQ16=sQuery(id+"F35.wireOp",EDGE,"E79.11.0");var subQ17=sQuery(id+"F35.wireOp",EDGE,"E79.9.0");var subQ18=sQuery(id+"F35.wireOp",EDGE,"E79.10.2");var subQ19=sQuery(id+"F35.wireOp",EDGE,"E79.10.0");var subQ20=sQuery(id+"F35.wireOp",EDGE,"E79.11.2");var subQ21=sQuery(id+"F35.wireOp",EDGE,"E79.6.0");var subQ22=sQuery(id+"F35.wireOp",EDGE,"E79.7.2");var subQ23=sQuery(id+"F35.wireOp",EDGE,"E79.7.0");var subQ24=sQuery(id+"F35.wireOp",EDGE,"E79.8.2");var subQ25=sQuery(id+"F35.wireOp",EDGE,"E75");Q1=makeQuery(id+"F36.boolean.opBoolean","SPLIT",FACE,{"disambiguationData":[TD([makeQuery(id+"F36.opExtrude","SWEPT_FACE",FACE,{"disambiguationData":[OSD([subQ25])]})])],"derivedFrom":makeQuery(id+"F36.opExtrude","CAP_FACE",FACE,{"disambiguationData":[OSD([subQ1,subQ25,subQ15,subQ9,subQ7,sQuery(id+"F35.wireOp",EDGE,"E79.1.1"),subQ10,subQ5,sQuery(id+"F35.wireOp",EDGE,"E79.2.1"),subQ8,subQ3,sQuery(id+"F35.wireOp",EDGE,"E79.3.1"),subQ6,subQ11,sQuery(id+"F35.wireOp",EDGE,"E79.4.1"),subQ4,subQ0,sQuery(id+"F35.wireOp",EDGE,"E79.5.1"),subQ12,subQ21,sQuery(id+"F35.wireOp",EDGE,"E79.6.1"),subQ2,subQ23,sQuery(id+"F35.wireOp",EDGE,"E79.7.1"),subQ22,subQ13,sQuery(id+"F35.wireOp",EDGE,"E79.8.1"),subQ24,subQ17,sQuery(id+"F35.wireOp",EDGE,"E79.9.1"),subQ14,subQ19,sQuery(id+"F35.wireOp",EDGE,"E79.10.1"),subQ18,subQ16,sQuery(id+"F35.wireOp",EDGE,"E79.11.1"),subQ20,sQuery(id+"F35.wireOp",EDGE,"E80")])],"isStart":true})});}
            var Q2;
            {var subQ0=sQuery(id+"F35.wireOp",EDGE,"E79.5.0");var subQ1=sQuery(id+"F35.wireOp",EDGE,"E74");var subQ2=sQuery(id+"F35.wireOp",EDGE,"E79.6.2");var subQ3=sQuery(id+"F35.wireOp",EDGE,"E79.3.0");var subQ4=sQuery(id+"F35.wireOp",EDGE,"E79.4.2");var subQ5=sQuery(id+"F35.wireOp",EDGE,"E79.2.0");var subQ6=sQuery(id+"F35.wireOp",EDGE,"E79.3.2");var subQ7=sQuery(id+"F35.wireOp",EDGE,"E79.1.0");var subQ8=sQuery(id+"F35.wireOp",EDGE,"E79.2.2");var subQ9=sQuery(id+"F35.wireOp",EDGE,"E78.MirrorCS");var subQ10=sQuery(id+"F35.wireOp",EDGE,"E79.1.2");var subQ11=sQuery(id+"F35.wireOp",EDGE,"E79.4.0");var subQ12=sQuery(id+"F35.wireOp",EDGE,"E79.5.2");var subQ13=sQuery(id+"F35.wireOp",EDGE,"E79.8.0");var subQ14=sQuery(id+"F35.wireOp",EDGE,"E79.9.2");var subQ15=sQuery(id+"F35.wireOp",EDGE,"E77");var subQ16=sQuery(id+"F35.wireOp",EDGE,"E79.11.0");var subQ17=sQuery(id+"F35.wireOp",EDGE,"E79.9.0");var subQ18=sQuery(id+"F35.wireOp",EDGE,"E79.10.2");var subQ19=sQuery(id+"F35.wireOp",EDGE,"E79.10.0");var subQ20=sQuery(id+"F35.wireOp",EDGE,"E79.11.2");var subQ21=sQuery(id+"F35.wireOp",EDGE,"E79.6.0");var subQ22=sQuery(id+"F35.wireOp",EDGE,"E79.7.2");var subQ23=sQuery(id+"F35.wireOp",EDGE,"E79.7.0");var subQ24=sQuery(id+"F35.wireOp",EDGE,"E79.8.2");var subQ25=sQuery(id+"F35.wireOp",EDGE,"E79.9.1");Q2=makeQuery(id+"F36.boolean.opBoolean","SPLIT",FACE,{"disambiguationData":[TD([makeQuery(id+"F36.opExtrude","SWEPT_FACE",FACE,{"disambiguationData":[OSD([subQ17])]})])],"derivedFrom":makeQuery(id+"F36.opExtrude","CAP_FACE",FACE,{"disambiguationData":[OSD([subQ1,sQuery(id+"F35.wireOp",EDGE,"E75"),subQ15,subQ9,subQ7,sQuery(id+"F35.wireOp",EDGE,"E79.1.1"),subQ10,subQ5,sQuery(id+"F35.wireOp",EDGE,"E79.2.1"),subQ8,subQ3,sQuery(id+"F35.wireOp",EDGE,"E79.3.1"),subQ6,subQ11,sQuery(id+"F35.wireOp",EDGE,"E79.4.1"),subQ4,subQ0,sQuery(id+"F35.wireOp",EDGE,"E79.5.1"),subQ12,subQ21,sQuery(id+"F35.wireOp",EDGE,"E79.6.1"),subQ2,subQ23,sQuery(id+"F35.wireOp",EDGE,"E79.7.1"),subQ22,subQ13,sQuery(id+"F35.wireOp",EDGE,"E79.8.1"),subQ24,subQ17,subQ25,subQ14,subQ19,sQuery(id+"F35.wireOp",EDGE,"E79.10.1"),subQ18,subQ16,sQuery(id+"F35.wireOp",EDGE,"E79.11.1"),subQ20,sQuery(id+"F35.wireOp",EDGE,"E80")])],"isStart":true})});}
            var Q3;
            {var subQ0=sQuery(id+"F35.wireOp",EDGE,"E79.5.0");var subQ1=sQuery(id+"F35.wireOp",EDGE,"E74");var subQ2=sQuery(id+"F35.wireOp",EDGE,"E79.6.2");var subQ3=sQuery(id+"F35.wireOp",EDGE,"E79.3.0");var subQ4=sQuery(id+"F35.wireOp",EDGE,"E79.4.2");var subQ5=sQuery(id+"F35.wireOp",EDGE,"E79.2.0");var subQ6=sQuery(id+"F35.wireOp",EDGE,"E79.3.2");var subQ7=sQuery(id+"F35.wireOp",EDGE,"E79.1.0");var subQ8=sQuery(id+"F35.wireOp",EDGE,"E79.2.2");var subQ9=sQuery(id+"F35.wireOp",EDGE,"E78.MirrorCS");var subQ10=sQuery(id+"F35.wireOp",EDGE,"E79.1.2");var subQ11=sQuery(id+"F35.wireOp",EDGE,"E79.4.0");var subQ12=sQuery(id+"F35.wireOp",EDGE,"E79.5.2");var subQ13=sQuery(id+"F35.wireOp",EDGE,"E79.8.0");var subQ14=sQuery(id+"F35.wireOp",EDGE,"E79.9.2");var subQ15=sQuery(id+"F35.wireOp",EDGE,"E77");var subQ16=sQuery(id+"F35.wireOp",EDGE,"E79.11.0");var subQ17=sQuery(id+"F35.wireOp",EDGE,"E79.9.0");var subQ18=sQuery(id+"F35.wireOp",EDGE,"E79.10.2");var subQ19=sQuery(id+"F35.wireOp",EDGE,"E79.10.0");var subQ20=sQuery(id+"F35.wireOp",EDGE,"E79.11.2");var subQ21=sQuery(id+"F35.wireOp",EDGE,"E79.6.0");var subQ22=sQuery(id+"F35.wireOp",EDGE,"E79.7.2");var subQ23=sQuery(id+"F35.wireOp",EDGE,"E79.7.0");var subQ24=sQuery(id+"F35.wireOp",EDGE,"E79.8.2");var subQ25=sQuery(id+"F35.wireOp",EDGE,"E79.10.1");Q3=makeQuery(id+"F36.boolean.opBoolean","SPLIT",FACE,{"disambiguationData":[TD([makeQuery(id+"F36.opExtrude","SWEPT_FACE",FACE,{"disambiguationData":[OSD([subQ19])]})])],"derivedFrom":makeQuery(id+"F36.opExtrude","CAP_FACE",FACE,{"disambiguationData":[OSD([subQ1,sQuery(id+"F35.wireOp",EDGE,"E75"),subQ15,subQ9,subQ7,sQuery(id+"F35.wireOp",EDGE,"E79.1.1"),subQ10,subQ5,sQuery(id+"F35.wireOp",EDGE,"E79.2.1"),subQ8,subQ3,sQuery(id+"F35.wireOp",EDGE,"E79.3.1"),subQ6,subQ11,sQuery(id+"F35.wireOp",EDGE,"E79.4.1"),subQ4,subQ0,sQuery(id+"F35.wireOp",EDGE,"E79.5.1"),subQ12,subQ21,sQuery(id+"F35.wireOp",EDGE,"E79.6.1"),subQ2,subQ23,sQuery(id+"F35.wireOp",EDGE,"E79.7.1"),subQ22,subQ13,sQuery(id+"F35.wireOp",EDGE,"E79.8.1"),subQ24,subQ17,sQuery(id+"F35.wireOp",EDGE,"E79.9.1"),subQ14,subQ19,subQ25,subQ18,subQ16,sQuery(id+"F35.wireOp",EDGE,"E79.11.1"),subQ20,sQuery(id+"F35.wireOp",EDGE,"E80")])],"isStart":true})});}
            var Q4;
            {var subQ0=sQuery(id+"F35.wireOp",EDGE,"E79.5.0");var subQ1=sQuery(id+"F35.wireOp",EDGE,"E74");var subQ2=sQuery(id+"F35.wireOp",EDGE,"E79.6.2");var subQ3=sQuery(id+"F35.wireOp",EDGE,"E79.3.0");var subQ4=sQuery(id+"F35.wireOp",EDGE,"E79.4.2");var subQ5=sQuery(id+"F35.wireOp",EDGE,"E79.2.0");var subQ6=sQuery(id+"F35.wireOp",EDGE,"E79.3.2");var subQ7=sQuery(id+"F35.wireOp",EDGE,"E79.1.0");var subQ8=sQuery(id+"F35.wireOp",EDGE,"E79.2.2");var subQ9=sQuery(id+"F35.wireOp",EDGE,"E78.MirrorCS");var subQ10=sQuery(id+"F35.wireOp",EDGE,"E79.1.2");var subQ11=sQuery(id+"F35.wireOp",EDGE,"E79.4.0");var subQ12=sQuery(id+"F35.wireOp",EDGE,"E79.5.2");var subQ13=sQuery(id+"F35.wireOp",EDGE,"E79.8.0");var subQ14=sQuery(id+"F35.wireOp",EDGE,"E79.9.2");var subQ15=sQuery(id+"F35.wireOp",EDGE,"E79.7.1");var subQ16=sQuery(id+"F35.wireOp",EDGE,"E77");var subQ17=sQuery(id+"F35.wireOp",EDGE,"E79.11.0");var subQ18=sQuery(id+"F35.wireOp",EDGE,"E79.9.0");var subQ19=sQuery(id+"F35.wireOp",EDGE,"E79.10.2");var subQ20=sQuery(id+"F35.wireOp",EDGE,"E79.10.0");var subQ21=sQuery(id+"F35.wireOp",EDGE,"E79.11.2");var subQ22=sQuery(id+"F35.wireOp",EDGE,"E79.6.0");var subQ23=sQuery(id+"F35.wireOp",EDGE,"E79.7.2");var subQ24=sQuery(id+"F35.wireOp",EDGE,"E79.7.0");var subQ25=sQuery(id+"F35.wireOp",EDGE,"E79.8.2");Q4=makeQuery(id+"F36.boolean.opBoolean","SPLIT",FACE,{"disambiguationData":[TD([makeQuery(id+"F36.opExtrude","SWEPT_FACE",FACE,{"disambiguationData":[OSD([subQ24])]})])],"derivedFrom":makeQuery(id+"F36.opExtrude","CAP_FACE",FACE,{"disambiguationData":[OSD([subQ1,sQuery(id+"F35.wireOp",EDGE,"E75"),subQ16,subQ9,subQ7,sQuery(id+"F35.wireOp",EDGE,"E79.1.1"),subQ10,subQ5,sQuery(id+"F35.wireOp",EDGE,"E79.2.1"),subQ8,subQ3,sQuery(id+"F35.wireOp",EDGE,"E79.3.1"),subQ6,subQ11,sQuery(id+"F35.wireOp",EDGE,"E79.4.1"),subQ4,subQ0,sQuery(id+"F35.wireOp",EDGE,"E79.5.1"),subQ12,subQ22,sQuery(id+"F35.wireOp",EDGE,"E79.6.1"),subQ2,subQ24,subQ15,subQ23,subQ13,sQuery(id+"F35.wireOp",EDGE,"E79.8.1"),subQ25,subQ18,sQuery(id+"F35.wireOp",EDGE,"E79.9.1"),subQ14,subQ20,sQuery(id+"F35.wireOp",EDGE,"E79.10.1"),subQ19,subQ17,sQuery(id+"F35.wireOp",EDGE,"E79.11.1"),subQ21,sQuery(id+"F35.wireOp",EDGE,"E80")])],"isStart":true})});}
            var Q5;
            {var subQ0=sQuery(id+"F35.wireOp",EDGE,"E79.5.0");var subQ1=sQuery(id+"F35.wireOp",EDGE,"E74");var subQ2=sQuery(id+"F35.wireOp",EDGE,"E79.6.2");var subQ3=sQuery(id+"F35.wireOp",EDGE,"E79.3.0");var subQ4=sQuery(id+"F35.wireOp",EDGE,"E79.4.2");var subQ5=sQuery(id+"F35.wireOp",EDGE,"E79.2.0");var subQ6=sQuery(id+"F35.wireOp",EDGE,"E79.3.2");var subQ7=sQuery(id+"F35.wireOp",EDGE,"E79.1.0");var subQ8=sQuery(id+"F35.wireOp",EDGE,"E79.2.2");var subQ9=sQuery(id+"F35.wireOp",EDGE,"E78.MirrorCS");var subQ10=sQuery(id+"F35.wireOp",EDGE,"E79.1.2");var subQ11=sQuery(id+"F35.wireOp",EDGE,"E79.4.0");var subQ12=sQuery(id+"F35.wireOp",EDGE,"E79.5.2");var subQ13=sQuery(id+"F35.wireOp",EDGE,"E79.8.0");var subQ14=sQuery(id+"F35.wireOp",EDGE,"E79.9.2");var subQ15=sQuery(id+"F35.wireOp",EDGE,"E77");var subQ16=sQuery(id+"F35.wireOp",EDGE,"E79.11.0");var subQ17=sQuery(id+"F35.wireOp",EDGE,"E79.4.1");var subQ18=sQuery(id+"F35.wireOp",EDGE,"E79.9.0");var subQ19=sQuery(id+"F35.wireOp",EDGE,"E79.10.2");var subQ20=sQuery(id+"F35.wireOp",EDGE,"E79.10.0");var subQ21=sQuery(id+"F35.wireOp",EDGE,"E79.11.2");var subQ22=sQuery(id+"F35.wireOp",EDGE,"E79.6.0");var subQ23=sQuery(id+"F35.wireOp",EDGE,"E79.7.2");var subQ24=sQuery(id+"F35.wireOp",EDGE,"E79.7.0");var subQ25=sQuery(id+"F35.wireOp",EDGE,"E79.8.2");Q5=makeQuery(id+"F36.boolean.opBoolean","SPLIT",FACE,{"disambiguationData":[TD([makeQuery(id+"F36.opExtrude","SWEPT_FACE",FACE,{"disambiguationData":[OSD([subQ11])]})])],"derivedFrom":makeQuery(id+"F36.opExtrude","CAP_FACE",FACE,{"disambiguationData":[OSD([subQ1,sQuery(id+"F35.wireOp",EDGE,"E75"),subQ15,subQ9,subQ7,sQuery(id+"F35.wireOp",EDGE,"E79.1.1"),subQ10,subQ5,sQuery(id+"F35.wireOp",EDGE,"E79.2.1"),subQ8,subQ3,sQuery(id+"F35.wireOp",EDGE,"E79.3.1"),subQ6,subQ11,subQ17,subQ4,subQ0,sQuery(id+"F35.wireOp",EDGE,"E79.5.1"),subQ12,subQ22,sQuery(id+"F35.wireOp",EDGE,"E79.6.1"),subQ2,subQ24,sQuery(id+"F35.wireOp",EDGE,"E79.7.1"),subQ23,subQ13,sQuery(id+"F35.wireOp",EDGE,"E79.8.1"),subQ25,subQ18,sQuery(id+"F35.wireOp",EDGE,"E79.9.1"),subQ14,subQ20,sQuery(id+"F35.wireOp",EDGE,"E79.10.1"),subQ19,subQ16,sQuery(id+"F35.wireOp",EDGE,"E79.11.1"),subQ21,sQuery(id+"F35.wireOp",EDGE,"E80")])],"isStart":true})});}
            var Q6;
            {var subQ0=sQuery(id+"F35.wireOp",EDGE,"E79.5.0");var subQ1=sQuery(id+"F35.wireOp",EDGE,"E74");var subQ2=sQuery(id+"F35.wireOp",EDGE,"E79.6.2");var subQ3=sQuery(id+"F35.wireOp",EDGE,"E79.3.0");var subQ4=sQuery(id+"F35.wireOp",EDGE,"E79.4.2");var subQ5=sQuery(id+"F35.wireOp",EDGE,"E79.2.0");var subQ6=sQuery(id+"F35.wireOp",EDGE,"E79.3.2");var subQ7=sQuery(id+"F35.wireOp",EDGE,"E79.1.0");var subQ8=sQuery(id+"F35.wireOp",EDGE,"E79.2.2");var subQ9=sQuery(id+"F35.wireOp",EDGE,"E78.MirrorCS");var subQ10=sQuery(id+"F35.wireOp",EDGE,"E79.1.2");var subQ11=sQuery(id+"F35.wireOp",EDGE,"E79.4.0");var subQ12=sQuery(id+"F35.wireOp",EDGE,"E79.5.2");var subQ13=sQuery(id+"F35.wireOp",EDGE,"E79.8.0");var subQ14=sQuery(id+"F35.wireOp",EDGE,"E79.9.2");var subQ15=sQuery(id+"F35.wireOp",EDGE,"E77");var subQ16=sQuery(id+"F35.wireOp",EDGE,"E79.11.0");var subQ17=sQuery(id+"F35.wireOp",EDGE,"E79.9.0");var subQ18=sQuery(id+"F35.wireOp",EDGE,"E79.10.2");var subQ19=sQuery(id+"F35.wireOp",EDGE,"E79.10.0");var subQ20=sQuery(id+"F35.wireOp",EDGE,"E79.11.2");var subQ21=sQuery(id+"F35.wireOp",EDGE,"E79.6.0");var subQ22=sQuery(id+"F35.wireOp",EDGE,"E79.7.2");var subQ23=sQuery(id+"F35.wireOp",EDGE,"E79.7.0");var subQ24=sQuery(id+"F35.wireOp",EDGE,"E79.8.2");var subQ25=sQuery(id+"F35.wireOp",EDGE,"E79.8.1");Q6=makeQuery(id+"F36.boolean.opBoolean","SPLIT",FACE,{"disambiguationData":[TD([makeQuery(id+"F36.opExtrude","SWEPT_FACE",FACE,{"disambiguationData":[OSD([subQ13])]})])],"derivedFrom":makeQuery(id+"F36.opExtrude","CAP_FACE",FACE,{"disambiguationData":[OSD([subQ1,sQuery(id+"F35.wireOp",EDGE,"E75"),subQ15,subQ9,subQ7,sQuery(id+"F35.wireOp",EDGE,"E79.1.1"),subQ10,subQ5,sQuery(id+"F35.wireOp",EDGE,"E79.2.1"),subQ8,subQ3,sQuery(id+"F35.wireOp",EDGE,"E79.3.1"),subQ6,subQ11,sQuery(id+"F35.wireOp",EDGE,"E79.4.1"),subQ4,subQ0,sQuery(id+"F35.wireOp",EDGE,"E79.5.1"),subQ12,subQ21,sQuery(id+"F35.wireOp",EDGE,"E79.6.1"),subQ2,subQ23,sQuery(id+"F35.wireOp",EDGE,"E79.7.1"),subQ22,subQ13,subQ25,subQ24,subQ17,sQuery(id+"F35.wireOp",EDGE,"E79.9.1"),subQ14,subQ19,sQuery(id+"F35.wireOp",EDGE,"E79.10.1"),subQ18,subQ16,sQuery(id+"F35.wireOp",EDGE,"E79.11.1"),subQ20,sQuery(id+"F35.wireOp",EDGE,"E80")])],"isStart":true})});}
            var Q7;
            {var subQ0=sQuery(id+"F35.wireOp",EDGE,"E79.5.0");var subQ1=sQuery(id+"F35.wireOp",EDGE,"E74");var subQ2=sQuery(id+"F35.wireOp",EDGE,"E79.6.2");var subQ3=sQuery(id+"F35.wireOp",EDGE,"E79.3.0");var subQ4=sQuery(id+"F35.wireOp",EDGE,"E79.4.2");var subQ5=sQuery(id+"F35.wireOp",EDGE,"E79.2.0");var subQ6=sQuery(id+"F35.wireOp",EDGE,"E79.3.2");var subQ7=sQuery(id+"F35.wireOp",EDGE,"E79.1.0");var subQ8=sQuery(id+"F35.wireOp",EDGE,"E79.2.2");var subQ9=sQuery(id+"F35.wireOp",EDGE,"E78.MirrorCS");var subQ10=sQuery(id+"F35.wireOp",EDGE,"E79.1.2");var subQ11=sQuery(id+"F35.wireOp",EDGE,"E79.4.0");var subQ12=sQuery(id+"F35.wireOp",EDGE,"E79.5.2");var subQ13=sQuery(id+"F35.wireOp",EDGE,"E79.8.0");var subQ14=sQuery(id+"F35.wireOp",EDGE,"E79.9.2");var subQ15=sQuery(id+"F35.wireOp",EDGE,"E77");var subQ16=sQuery(id+"F35.wireOp",EDGE,"E79.11.0");var subQ17=sQuery(id+"F35.wireOp",EDGE,"E79.9.0");var subQ18=sQuery(id+"F35.wireOp",EDGE,"E79.10.2");var subQ19=sQuery(id+"F35.wireOp",EDGE,"E79.10.0");var subQ20=sQuery(id+"F35.wireOp",EDGE,"E79.11.2");var subQ21=sQuery(id+"F35.wireOp",EDGE,"E79.6.0");var subQ22=sQuery(id+"F35.wireOp",EDGE,"E79.7.2");var subQ23=sQuery(id+"F35.wireOp",EDGE,"E79.7.0");var subQ24=sQuery(id+"F35.wireOp",EDGE,"E79.8.2");var subQ25=sQuery(id+"F35.wireOp",EDGE,"E79.2.1");Q7=makeQuery(id+"F36.boolean.opBoolean","SPLIT",FACE,{"disambiguationData":[TD([makeQuery(id+"F36.opExtrude","SWEPT_FACE",FACE,{"disambiguationData":[OSD([subQ5])]})])],"derivedFrom":makeQuery(id+"F36.opExtrude","CAP_FACE",FACE,{"disambiguationData":[OSD([subQ1,sQuery(id+"F35.wireOp",EDGE,"E75"),subQ15,subQ9,subQ7,sQuery(id+"F35.wireOp",EDGE,"E79.1.1"),subQ10,subQ5,subQ25,subQ8,subQ3,sQuery(id+"F35.wireOp",EDGE,"E79.3.1"),subQ6,subQ11,sQuery(id+"F35.wireOp",EDGE,"E79.4.1"),subQ4,subQ0,sQuery(id+"F35.wireOp",EDGE,"E79.5.1"),subQ12,subQ21,sQuery(id+"F35.wireOp",EDGE,"E79.6.1"),subQ2,subQ23,sQuery(id+"F35.wireOp",EDGE,"E79.7.1"),subQ22,subQ13,sQuery(id+"F35.wireOp",EDGE,"E79.8.1"),subQ24,subQ17,sQuery(id+"F35.wireOp",EDGE,"E79.9.1"),subQ14,subQ19,sQuery(id+"F35.wireOp",EDGE,"E79.10.1"),subQ18,subQ16,sQuery(id+"F35.wireOp",EDGE,"E79.11.1"),subQ20,sQuery(id+"F35.wireOp",EDGE,"E80")])],"isStart":true})});}
            var Q8;
            {var subQ0=sQuery(id+"F35.wireOp",EDGE,"E79.5.0");var subQ1=sQuery(id+"F35.wireOp",EDGE,"E74");var subQ2=sQuery(id+"F35.wireOp",EDGE,"E79.6.2");var subQ3=sQuery(id+"F35.wireOp",EDGE,"E79.6.1");var subQ4=sQuery(id+"F35.wireOp",EDGE,"E79.3.0");var subQ5=sQuery(id+"F35.wireOp",EDGE,"E79.4.2");var subQ6=sQuery(id+"F35.wireOp",EDGE,"E79.2.0");var subQ7=sQuery(id+"F35.wireOp",EDGE,"E79.3.2");var subQ8=sQuery(id+"F35.wireOp",EDGE,"E79.1.0");var subQ9=sQuery(id+"F35.wireOp",EDGE,"E79.2.2");var subQ10=sQuery(id+"F35.wireOp",EDGE,"E78.MirrorCS");var subQ11=sQuery(id+"F35.wireOp",EDGE,"E79.1.2");var subQ12=sQuery(id+"F35.wireOp",EDGE,"E79.4.0");var subQ13=sQuery(id+"F35.wireOp",EDGE,"E79.5.2");var subQ14=sQuery(id+"F35.wireOp",EDGE,"E79.6.0");var subQ15=sQuery(id+"F35.wireOp",EDGE,"E79.8.0");var subQ16=sQuery(id+"F35.wireOp",EDGE,"E79.9.2");var subQ17=sQuery(id+"F35.wireOp",EDGE,"E77");var subQ18=sQuery(id+"F35.wireOp",EDGE,"E79.11.0");var subQ19=sQuery(id+"F35.wireOp",EDGE,"E79.9.0");var subQ20=sQuery(id+"F35.wireOp",EDGE,"E79.10.2");var subQ21=sQuery(id+"F35.wireOp",EDGE,"E79.10.0");var subQ22=sQuery(id+"F35.wireOp",EDGE,"E79.11.2");var subQ23=sQuery(id+"F35.wireOp",EDGE,"E79.7.2");var subQ24=sQuery(id+"F35.wireOp",EDGE,"E79.7.0");var subQ25=sQuery(id+"F35.wireOp",EDGE,"E79.8.2");Q8=makeQuery(id+"F36.boolean.opBoolean","SPLIT",FACE,{"disambiguationData":[TD([makeQuery(id+"F36.opExtrude","SWEPT_FACE",FACE,{"disambiguationData":[OSD([subQ14])]})])],"derivedFrom":makeQuery(id+"F36.opExtrude","CAP_FACE",FACE,{"disambiguationData":[OSD([subQ1,sQuery(id+"F35.wireOp",EDGE,"E75"),subQ17,subQ10,subQ8,sQuery(id+"F35.wireOp",EDGE,"E79.1.1"),subQ11,subQ6,sQuery(id+"F35.wireOp",EDGE,"E79.2.1"),subQ9,subQ4,sQuery(id+"F35.wireOp",EDGE,"E79.3.1"),subQ7,subQ12,sQuery(id+"F35.wireOp",EDGE,"E79.4.1"),subQ5,subQ0,sQuery(id+"F35.wireOp",EDGE,"E79.5.1"),subQ13,subQ14,subQ3,subQ2,subQ24,sQuery(id+"F35.wireOp",EDGE,"E79.7.1"),subQ23,subQ15,sQuery(id+"F35.wireOp",EDGE,"E79.8.1"),subQ25,subQ19,sQuery(id+"F35.wireOp",EDGE,"E79.9.1"),subQ16,subQ21,sQuery(id+"F35.wireOp",EDGE,"E79.10.1"),subQ20,subQ18,sQuery(id+"F35.wireOp",EDGE,"E79.11.1"),subQ22,sQuery(id+"F35.wireOp",EDGE,"E80")])],"isStart":true})});}
            var Q9;
            {var subQ0=sQuery(id+"F35.wireOp",EDGE,"E79.5.0");var subQ1=sQuery(id+"F35.wireOp",EDGE,"E74");var subQ2=sQuery(id+"F35.wireOp",EDGE,"E79.6.2");var subQ3=sQuery(id+"F35.wireOp",EDGE,"E79.3.0");var subQ4=sQuery(id+"F35.wireOp",EDGE,"E79.4.2");var subQ5=sQuery(id+"F35.wireOp",EDGE,"E79.2.0");var subQ6=sQuery(id+"F35.wireOp",EDGE,"E79.3.2");var subQ7=sQuery(id+"F35.wireOp",EDGE,"E79.1.0");var subQ8=sQuery(id+"F35.wireOp",EDGE,"E79.2.2");var subQ9=sQuery(id+"F35.wireOp",EDGE,"E78.MirrorCS");var subQ10=sQuery(id+"F35.wireOp",EDGE,"E79.1.2");var subQ11=sQuery(id+"F35.wireOp",EDGE,"E79.4.0");var subQ12=sQuery(id+"F35.wireOp",EDGE,"E79.5.2");var subQ13=sQuery(id+"F35.wireOp",EDGE,"E79.8.0");var subQ14=sQuery(id+"F35.wireOp",EDGE,"E79.9.2");var subQ15=sQuery(id+"F35.wireOp",EDGE,"E77");var subQ16=sQuery(id+"F35.wireOp",EDGE,"E79.11.0");var subQ17=sQuery(id+"F35.wireOp",EDGE,"E79.9.0");var subQ18=sQuery(id+"F35.wireOp",EDGE,"E79.10.2");var subQ19=sQuery(id+"F35.wireOp",EDGE,"E79.10.0");var subQ20=sQuery(id+"F35.wireOp",EDGE,"E79.11.2");var subQ21=sQuery(id+"F35.wireOp",EDGE,"E79.6.0");var subQ22=sQuery(id+"F35.wireOp",EDGE,"E79.7.2");var subQ23=sQuery(id+"F35.wireOp",EDGE,"E79.7.0");var subQ24=sQuery(id+"F35.wireOp",EDGE,"E79.8.2");var subQ25=sQuery(id+"F35.wireOp",EDGE,"E79.11.1");Q9=makeQuery(id+"F36.boolean.opBoolean","SPLIT",FACE,{"disambiguationData":[TD([makeQuery(id+"F36.opExtrude","SWEPT_FACE",FACE,{"disambiguationData":[OSD([subQ16])]})])],"derivedFrom":makeQuery(id+"F36.opExtrude","CAP_FACE",FACE,{"disambiguationData":[OSD([subQ1,sQuery(id+"F35.wireOp",EDGE,"E75"),subQ15,subQ9,subQ7,sQuery(id+"F35.wireOp",EDGE,"E79.1.1"),subQ10,subQ5,sQuery(id+"F35.wireOp",EDGE,"E79.2.1"),subQ8,subQ3,sQuery(id+"F35.wireOp",EDGE,"E79.3.1"),subQ6,subQ11,sQuery(id+"F35.wireOp",EDGE,"E79.4.1"),subQ4,subQ0,sQuery(id+"F35.wireOp",EDGE,"E79.5.1"),subQ12,subQ21,sQuery(id+"F35.wireOp",EDGE,"E79.6.1"),subQ2,subQ23,sQuery(id+"F35.wireOp",EDGE,"E79.7.1"),subQ22,subQ13,sQuery(id+"F35.wireOp",EDGE,"E79.8.1"),subQ24,subQ17,sQuery(id+"F35.wireOp",EDGE,"E79.9.1"),subQ14,subQ19,sQuery(id+"F35.wireOp",EDGE,"E79.10.1"),subQ18,subQ16,subQ25,subQ20,sQuery(id+"F35.wireOp",EDGE,"E80")])],"isStart":true})});}
            var Q10;
            {var subQ0=sQuery(id+"F35.wireOp",EDGE,"E74");Q10=makeQuery(id+"F36.boolean.opBoolean","MERGE",FACE,{"derivedFrom":[makeQuery(id+"F34.opExtrude","SWEPT_FACE",FACE,{"disambiguationData":[OSD([sQuery(id+"F33.wireOp",EDGE,"E73")])]}),makeQuery(id+"F36.opExtrude","SWEPT_FACE",FACE,{"disambiguationData":[OSD([subQ0]),TDD([makeQuery(id+"F35.imprint","IMPRINT",EDGE,{"disambiguationData":[TD([[makeQuery(id+"F35.imprint","INTERSECT",VERTEX,{"derivedFrom":[subQ0,sQuery(id+"F35.wireOp",EDGE,"E79.9.0")]}),-1.0]])],"derivedFrom":subQ0})])]}),makeQuery(id+"F36.opExtrude","SWEPT_FACE",FACE,{"disambiguationData":[OSD([subQ0]),TDD([makeQuery(id+"F35.imprint","IMPRINT",EDGE,{"disambiguationData":[TD([[makeQuery(id+"F35.imprint","INTERSECT",VERTEX,{"derivedFrom":[subQ0,sQuery(id+"F35.wireOp",EDGE,"E79.10.0")]}),-1.0]])],"derivedFrom":subQ0})])]}),makeQuery(id+"F36.opExtrude","SWEPT_FACE",FACE,{"disambiguationData":[OSD([subQ0]),TDD([makeQuery(id+"F35.imprint","IMPRINT",EDGE,{"disambiguationData":[TD([[makeQuery(id+"F35.imprint","INTERSECT",VERTEX,{"derivedFrom":[subQ0,sQuery(id+"F35.wireOp",EDGE,"E77")]}),1.0]])],"derivedFrom":subQ0})])]}),makeQuery(id+"F36.opExtrude","SWEPT_FACE",FACE,{"disambiguationData":[OSD([subQ0]),TDD([makeQuery(id+"F35.imprint","IMPRINT",EDGE,{"disambiguationData":[TD([[makeQuery(id+"F35.imprint","INTERSECT",VERTEX,{"derivedFrom":[subQ0,sQuery(id+"F35.wireOp",EDGE,"E78.MirrorCS")]}),-1.0]])],"derivedFrom":subQ0})])]}),makeQuery(id+"F36.opExtrude","SWEPT_FACE",FACE,{"disambiguationData":[OSD([subQ0]),TDD([makeQuery(id+"F35.imprint","IMPRINT",EDGE,{"disambiguationData":[TD([[makeQuery(id+"F35.imprint","INTERSECT",VERTEX,{"derivedFrom":[subQ0,sQuery(id+"F35.wireOp",EDGE,"E79.1.0")]}),-1.0]])],"derivedFrom":subQ0})])]}),makeQuery(id+"F36.opExtrude","SWEPT_FACE",FACE,{"disambiguationData":[OSD([subQ0]),TDD([makeQuery(id+"F35.imprint","IMPRINT",EDGE,{"disambiguationData":[TD([[makeQuery(id+"F35.imprint","INTERSECT",VERTEX,{"derivedFrom":[subQ0,sQuery(id+"F35.wireOp",EDGE,"E79.2.0")]}),-1.0]])],"derivedFrom":subQ0})])]}),makeQuery(id+"F36.opExtrude","SWEPT_FACE",FACE,{"disambiguationData":[OSD([subQ0]),TDD([makeQuery(id+"F35.imprint","IMPRINT",EDGE,{"disambiguationData":[TD([[makeQuery(id+"F35.imprint","INTERSECT",VERTEX,{"derivedFrom":[subQ0,sQuery(id+"F35.wireOp",EDGE,"E79.3.0")]}),-1.0]])],"derivedFrom":subQ0})])]}),makeQuery(id+"F36.opExtrude","SWEPT_FACE",FACE,{"disambiguationData":[OSD([subQ0]),TDD([makeQuery(id+"F35.imprint","IMPRINT",EDGE,{"disambiguationData":[TD([[makeQuery(id+"F35.imprint","INTERSECT",VERTEX,{"derivedFrom":[subQ0,sQuery(id+"F35.wireOp",EDGE,"E79.4.0")]}),-1.0]])],"derivedFrom":subQ0})])]}),makeQuery(id+"F36.opExtrude","SWEPT_FACE",FACE,{"disambiguationData":[OSD([subQ0]),TDD([makeQuery(id+"F35.imprint","IMPRINT",EDGE,{"disambiguationData":[TD([[makeQuery(id+"F35.imprint","INTERSECT",VERTEX,{"derivedFrom":[subQ0,sQuery(id+"F35.wireOp",EDGE,"E79.5.0")]}),-1.0]])],"derivedFrom":subQ0})])]}),makeQuery(id+"F36.opExtrude","SWEPT_FACE",FACE,{"disambiguationData":[OSD([subQ0]),TDD([makeQuery(id+"F35.imprint","IMPRINT",EDGE,{"disambiguationData":[TD([[makeQuery(id+"F35.imprint","INTERSECT",VERTEX,{"derivedFrom":[subQ0,sQuery(id+"F35.wireOp",EDGE,"E79.6.0")]}),-1.0]])],"derivedFrom":subQ0})])]}),makeQuery(id+"F36.opExtrude","SWEPT_FACE",FACE,{"disambiguationData":[OSD([subQ0]),TDD([makeQuery(id+"F35.imprint","IMPRINT",EDGE,{"disambiguationData":[TD([[makeQuery(id+"F35.imprint","INTERSECT",VERTEX,{"derivedFrom":[subQ0,sQuery(id+"F35.wireOp",EDGE,"E79.7.0")]}),-1.0]])],"derivedFrom":subQ0})])]}),makeQuery(id+"F36.opExtrude","SWEPT_FACE",FACE,{"disambiguationData":[OSD([subQ0]),TDD([makeQuery(id+"F35.imprint","IMPRINT",EDGE,{"disambiguationData":[TD([[makeQuery(id+"F35.imprint","INTERSECT",VERTEX,{"derivedFrom":[subQ0,sQuery(id+"F35.wireOp",EDGE,"E79.8.0")]}),-1.0]])],"derivedFrom":subQ0})])]})]});}
            var Q11;
            {var subQ0=sQuery(id+"F35.wireOp",EDGE,"E79.5.0");var subQ1=sQuery(id+"F35.wireOp",EDGE,"E74");var subQ2=sQuery(id+"F35.wireOp",EDGE,"E79.6.2");var subQ3=sQuery(id+"F35.wireOp",EDGE,"E79.3.0");var subQ4=sQuery(id+"F35.wireOp",EDGE,"E79.4.2");var subQ5=sQuery(id+"F35.wireOp",EDGE,"E79.2.0");var subQ6=sQuery(id+"F35.wireOp",EDGE,"E79.3.2");var subQ7=sQuery(id+"F35.wireOp",EDGE,"E79.1.0");var subQ8=sQuery(id+"F35.wireOp",EDGE,"E79.2.2");var subQ9=sQuery(id+"F35.wireOp",EDGE,"E78.MirrorCS");var subQ10=sQuery(id+"F35.wireOp",EDGE,"E79.1.2");var subQ11=sQuery(id+"F35.wireOp",EDGE,"E79.4.0");var subQ12=sQuery(id+"F35.wireOp",EDGE,"E79.5.2");var subQ13=sQuery(id+"F35.wireOp",EDGE,"E79.8.0");var subQ14=sQuery(id+"F35.wireOp",EDGE,"E79.9.2");var subQ15=sQuery(id+"F35.wireOp",EDGE,"E77");var subQ16=sQuery(id+"F35.wireOp",EDGE,"E79.11.0");var subQ17=sQuery(id+"F35.wireOp",EDGE,"E79.9.0");var subQ18=sQuery(id+"F35.wireOp",EDGE,"E79.10.2");var subQ19=sQuery(id+"F35.wireOp",EDGE,"E79.10.0");var subQ20=sQuery(id+"F35.wireOp",EDGE,"E79.11.2");var subQ21=sQuery(id+"F35.wireOp",EDGE,"E79.6.0");var subQ22=sQuery(id+"F35.wireOp",EDGE,"E79.7.2");var subQ23=sQuery(id+"F35.wireOp",EDGE,"E79.7.0");var subQ24=sQuery(id+"F35.wireOp",EDGE,"E79.8.2");var subQ25=sQuery(id+"F35.wireOp",EDGE,"E79.3.1");Q11=makeQuery(id+"F36.boolean.opBoolean","SPLIT",FACE,{"disambiguationData":[TD([makeQuery(id+"F36.opExtrude","SWEPT_FACE",FACE,{"disambiguationData":[OSD([subQ3])]})])],"derivedFrom":makeQuery(id+"F36.opExtrude","CAP_FACE",FACE,{"disambiguationData":[OSD([subQ1,sQuery(id+"F35.wireOp",EDGE,"E75"),subQ15,subQ9,subQ7,sQuery(id+"F35.wireOp",EDGE,"E79.1.1"),subQ10,subQ5,sQuery(id+"F35.wireOp",EDGE,"E79.2.1"),subQ8,subQ3,subQ25,subQ6,subQ11,sQuery(id+"F35.wireOp",EDGE,"E79.4.1"),subQ4,subQ0,sQuery(id+"F35.wireOp",EDGE,"E79.5.1"),subQ12,subQ21,sQuery(id+"F35.wireOp",EDGE,"E79.6.1"),subQ2,subQ23,sQuery(id+"F35.wireOp",EDGE,"E79.7.1"),subQ22,subQ13,sQuery(id+"F35.wireOp",EDGE,"E79.8.1"),subQ24,subQ17,sQuery(id+"F35.wireOp",EDGE,"E79.9.1"),subQ14,subQ19,sQuery(id+"F35.wireOp",EDGE,"E79.10.1"),subQ18,subQ16,sQuery(id+"F35.wireOp",EDGE,"E79.11.1"),subQ20,sQuery(id+"F35.wireOp",EDGE,"E80")])],"isStart":true})});}
            var Q12;
            Q12=makeQuery(id+"F32.opExtrude","CAP_FACE",FACE,{"disambiguationData":[OSD([sQuery(id+"F31.wireOp",EDGE,"E65"),sQuery(id+"F31.wireOp",EDGE,"E66"),sQuery(id+"F31.wireOp",EDGE,"E68"),sQuery(id+"F31.wireOp",EDGE,"E69.MirrorCS"),sQuery(id+"F31.wireOp",EDGE,"E70"),sQuery(id+"F31.wireOp",EDGE,"E71.1.0"),sQuery(id+"F31.wireOp",EDGE,"E71.1.1"),sQuery(id+"F31.wireOp",EDGE,"E71.1.2"),sQuery(id+"F31.wireOp",EDGE,"E71.2.0"),sQuery(id+"F31.wireOp",EDGE,"E71.2.1"),sQuery(id+"F31.wireOp",EDGE,"E71.2.2"),sQuery(id+"F31.wireOp",EDGE,"E71.3.0"),sQuery(id+"F31.wireOp",EDGE,"E71.3.1"),sQuery(id+"F31.wireOp",EDGE,"E71.3.2"),sQuery(id+"F31.wireOp",EDGE,"E71.4.0"),sQuery(id+"F31.wireOp",EDGE,"E71.4.1"),sQuery(id+"F31.wireOp",EDGE,"E71.4.2"),sQuery(id+"F31.wireOp",EDGE,"E71.5.0"),sQuery(id+"F31.wireOp",EDGE,"E71.5.1"),sQuery(id+"F31.wireOp",EDGE,"E71.5.2"),sQuery(id+"F31.wireOp",EDGE,"E71.6.0"),sQuery(id+"F31.wireOp",EDGE,"E71.6.1"),sQuery(id+"F31.wireOp",EDGE,"E71.6.2"),sQuery(id+"F31.wireOp",EDGE,"E71.7.0"),sQuery(id+"F31.wireOp",EDGE,"E71.7.1"),sQuery(id+"F31.wireOp",EDGE,"E71.7.2"),sQuery(id+"F31.wireOp",EDGE,"E71.8.0"),sQuery(id+"F31.wireOp",EDGE,"E71.8.1"),sQuery(id+"F31.wireOp",EDGE,"E71.8.2"),sQuery(id+"F31.wireOp",EDGE,"E71.9.0"),sQuery(id+"F31.wireOp",EDGE,"E71.9.1"),sQuery(id+"F31.wireOp",EDGE,"E71.9.2"),sQuery(id+"F31.wireOp",EDGE,"E71.10.0"),sQuery(id+"F31.wireOp",EDGE,"E71.10.1"),sQuery(id+"F31.wireOp",EDGE,"E71.10.2"),sQuery(id+"F31.wireOp",EDGE,"E71.11.0"),sQuery(id+"F31.wireOp",EDGE,"E71.11.1"),sQuery(id+"F31.wireOp",EDGE,"E71.11.2"),sQuery(id+"F31.wireOp",EDGE,"E71.12.0"),sQuery(id+"F31.wireOp",EDGE,"E71.12.1"),sQuery(id+"F31.wireOp",EDGE,"E71.12.2")])],"isStart":false});
            var Q13;
            {var subQ0=sQuery(id+"F35.wireOp",EDGE,"E79.5.0");var subQ1=sQuery(id+"F35.wireOp",EDGE,"E74");var subQ2=sQuery(id+"F35.wireOp",EDGE,"E79.6.2");var subQ3=sQuery(id+"F35.wireOp",EDGE,"E79.3.0");var subQ4=sQuery(id+"F35.wireOp",EDGE,"E79.4.2");var subQ5=sQuery(id+"F35.wireOp",EDGE,"E79.2.0");var subQ6=sQuery(id+"F35.wireOp",EDGE,"E79.3.2");var subQ7=sQuery(id+"F35.wireOp",EDGE,"E79.1.0");var subQ8=sQuery(id+"F35.wireOp",EDGE,"E79.2.2");var subQ9=sQuery(id+"F35.wireOp",EDGE,"E78.MirrorCS");var subQ10=sQuery(id+"F35.wireOp",EDGE,"E79.1.2");var subQ11=sQuery(id+"F35.wireOp",EDGE,"E79.4.0");var subQ12=sQuery(id+"F35.wireOp",EDGE,"E79.5.2");var subQ13=sQuery(id+"F35.wireOp",EDGE,"E79.8.0");var subQ14=sQuery(id+"F35.wireOp",EDGE,"E79.9.2");var subQ15=sQuery(id+"F35.wireOp",EDGE,"E77");var subQ16=sQuery(id+"F35.wireOp",EDGE,"E79.11.0");var subQ17=sQuery(id+"F35.wireOp",EDGE,"E79.9.0");var subQ18=sQuery(id+"F35.wireOp",EDGE,"E79.10.2");var subQ19=sQuery(id+"F35.wireOp",EDGE,"E79.10.0");var subQ20=sQuery(id+"F35.wireOp",EDGE,"E79.11.2");var subQ21=sQuery(id+"F35.wireOp",EDGE,"E79.6.0");var subQ22=sQuery(id+"F35.wireOp",EDGE,"E79.7.2");var subQ23=sQuery(id+"F35.wireOp",EDGE,"E79.7.0");var subQ24=sQuery(id+"F35.wireOp",EDGE,"E79.8.2");var subQ25=sQuery(id+"F35.wireOp",EDGE,"E79.1.1");Q13=makeQuery(id+"F36.boolean.opBoolean","SPLIT",FACE,{"disambiguationData":[TD([makeQuery(id+"F36.opExtrude","SWEPT_FACE",FACE,{"disambiguationData":[OSD([subQ7])]})])],"derivedFrom":makeQuery(id+"F36.opExtrude","CAP_FACE",FACE,{"disambiguationData":[OSD([subQ1,sQuery(id+"F35.wireOp",EDGE,"E75"),subQ15,subQ9,subQ7,subQ25,subQ10,subQ5,sQuery(id+"F35.wireOp",EDGE,"E79.2.1"),subQ8,subQ3,sQuery(id+"F35.wireOp",EDGE,"E79.3.1"),subQ6,subQ11,sQuery(id+"F35.wireOp",EDGE,"E79.4.1"),subQ4,subQ0,sQuery(id+"F35.wireOp",EDGE,"E79.5.1"),subQ12,subQ21,sQuery(id+"F35.wireOp",EDGE,"E79.6.1"),subQ2,subQ23,sQuery(id+"F35.wireOp",EDGE,"E79.7.1"),subQ22,subQ13,sQuery(id+"F35.wireOp",EDGE,"E79.8.1"),subQ24,subQ17,sQuery(id+"F35.wireOp",EDGE,"E79.9.1"),subQ14,subQ19,sQuery(id+"F35.wireOp",EDGE,"E79.10.1"),subQ18,subQ16,sQuery(id+"F35.wireOp",EDGE,"E79.11.1"),subQ20,sQuery(id+"F35.wireOp",EDGE,"E80")])],"isStart":true})});}
            fillet(context, id + "F48", {"entities" : qUnion([Q0, Q1, Q2, Q3, Q4, Q5, Q6, Q7, Q8, Q9, Q10, Q11, Q12, Q13]), "radius" : .5 * mm, "tangentPropagation" : true, "allowEdgeOverflow" : false});
        }
        {
            var Q0;
            Q0=makeQuery(id+"F36.opExtrude","CAP_FACE",FACE,{"disambiguationData":[OSD([sQuery(id+"F35.wireOp",EDGE,"E74"),sQuery(id+"F35.wireOp",EDGE,"E75"),sQuery(id+"F35.wireOp",EDGE,"E77"),sQuery(id+"F35.wireOp",EDGE,"E78.MirrorCS"),sQuery(id+"F35.wireOp",EDGE,"E79.1.0"),sQuery(id+"F35.wireOp",EDGE,"E79.1.1"),sQuery(id+"F35.wireOp",EDGE,"E79.1.2"),sQuery(id+"F35.wireOp",EDGE,"E79.2.0"),sQuery(id+"F35.wireOp",EDGE,"E79.2.1"),sQuery(id+"F35.wireOp",EDGE,"E79.2.2"),sQuery(id+"F35.wireOp",EDGE,"E79.3.0"),sQuery(id+"F35.wireOp",EDGE,"E79.3.1"),sQuery(id+"F35.wireOp",EDGE,"E79.3.2"),sQuery(id+"F35.wireOp",EDGE,"E79.4.0"),sQuery(id+"F35.wireOp",EDGE,"E79.4.1"),sQuery(id+"F35.wireOp",EDGE,"E79.4.2"),sQuery(id+"F35.wireOp",EDGE,"E79.5.0"),sQuery(id+"F35.wireOp",EDGE,"E79.5.1"),sQuery(id+"F35.wireOp",EDGE,"E79.5.2"),sQuery(id+"F35.wireOp",EDGE,"E79.6.0"),sQuery(id+"F35.wireOp",EDGE,"E79.6.1"),sQuery(id+"F35.wireOp",EDGE,"E79.6.2"),sQuery(id+"F35.wireOp",EDGE,"E79.7.0"),sQuery(id+"F35.wireOp",EDGE,"E79.7.1"),sQuery(id+"F35.wireOp",EDGE,"E79.7.2"),sQuery(id+"F35.wireOp",EDGE,"E79.8.0"),sQuery(id+"F35.wireOp",EDGE,"E79.8.1"),sQuery(id+"F35.wireOp",EDGE,"E79.8.2"),sQuery(id+"F35.wireOp",EDGE,"E79.9.0"),sQuery(id+"F35.wireOp",EDGE,"E79.9.1"),sQuery(id+"F35.wireOp",EDGE,"E79.9.2"),sQuery(id+"F35.wireOp",EDGE,"E79.10.0"),sQuery(id+"F35.wireOp",EDGE,"E79.10.1"),sQuery(id+"F35.wireOp",EDGE,"E79.10.2"),sQuery(id+"F35.wireOp",EDGE,"E79.11.0"),sQuery(id+"F35.wireOp",EDGE,"E79.11.1"),sQuery(id+"F35.wireOp",EDGE,"E79.11.2"),sQuery(id+"F35.wireOp",EDGE,"E80")])],"isStart":false});
            fillet(context, id + "F49", {"entities" : qUnion([Q0]), "radius" : .5 * mm, "tangentPropagation" : true, "allowEdgeOverflow" : false});
        }
        {
            var Q0;
            {var subQ0=sQuery(id+"F39.wireOp",EDGE,"E88.5.1");var subQ1=sQuery(id+"F39.wireOp",EDGE,"E83");var subQ2=sQuery(id+"F39.wireOp",EDGE,"E88.6.0");var subQ3=sQuery(id+"F39.wireOp",EDGE,"E88.3.1");var subQ4=sQuery(id+"F39.wireOp",EDGE,"E88.4.0");var subQ5=sQuery(id+"F39.wireOp",EDGE,"E88.2.1");var subQ6=sQuery(id+"F39.wireOp",EDGE,"E88.3.0");var subQ7=sQuery(id+"F39.wireOp",EDGE,"E88.1.1");var subQ8=sQuery(id+"F39.wireOp",EDGE,"E88.2.0");var subQ9=sQuery(id+"F39.wireOp",EDGE,"E87.MirrorCS");var subQ10=sQuery(id+"F39.wireOp",EDGE,"E88.1.0");var subQ11=sQuery(id+"F39.wireOp",EDGE,"E88.4.1");var subQ12=sQuery(id+"F39.wireOp",EDGE,"E88.5.0");var subQ13=sQuery(id+"F39.wireOp",EDGE,"E88.7.2");var subQ14=sQuery(id+"F39.wireOp",EDGE,"E86");var subQ15=sQuery(id+"F39.wireOp",EDGE,"E88.10.1");var subQ16=sQuery(id+"F39.wireOp",EDGE,"E88.8.1");var subQ17=sQuery(id+"F39.wireOp",EDGE,"E88.9.0");var subQ18=sQuery(id+"F39.wireOp",EDGE,"E88.9.1");var subQ19=sQuery(id+"F39.wireOp",EDGE,"E88.10.0");var subQ20=sQuery(id+"F39.wireOp",EDGE,"E88.6.1");var subQ21=sQuery(id+"F39.wireOp",EDGE,"E88.7.0");var subQ22=sQuery(id+"F39.wireOp",EDGE,"E88.7.1");var subQ23=sQuery(id+"F39.wireOp",EDGE,"E88.8.0");Q0=makeQuery(id+"F40.boolean.opBoolean","SPLIT",FACE,{"disambiguationData":[TD([makeQuery(id+"F40.opExtrude","SWEPT_FACE",FACE,{"disambiguationData":[OSD([subQ21])]})])],"derivedFrom":makeQuery(id+"F40.opExtrude","CAP_FACE",FACE,{"disambiguationData":[OSD([subQ1,sQuery(id+"F39.wireOp",EDGE,"E84"),subQ14,subQ9,subQ10,subQ7,sQuery(id+"F39.wireOp",EDGE,"E88.1.2"),subQ8,subQ5,sQuery(id+"F39.wireOp",EDGE,"E88.2.2"),subQ6,subQ3,sQuery(id+"F39.wireOp",EDGE,"E88.3.2"),subQ4,subQ11,sQuery(id+"F39.wireOp",EDGE,"E88.4.2"),subQ12,subQ0,sQuery(id+"F39.wireOp",EDGE,"E88.5.2"),subQ2,subQ20,sQuery(id+"F39.wireOp",EDGE,"E88.6.2"),subQ21,subQ22,subQ13,subQ23,subQ16,sQuery(id+"F39.wireOp",EDGE,"E88.8.2"),subQ17,subQ18,sQuery(id+"F39.wireOp",EDGE,"E88.9.2"),subQ19,subQ15,sQuery(id+"F39.wireOp",EDGE,"E88.10.2"),sQuery(id+"F39.wireOp",EDGE,"E89")])],"isStart":true})});}
            var Q1;
            {var subQ0=sQuery(id+"F39.wireOp",EDGE,"E88.5.1");var subQ1=sQuery(id+"F39.wireOp",EDGE,"E83");var subQ2=sQuery(id+"F39.wireOp",EDGE,"E88.6.0");var subQ3=sQuery(id+"F39.wireOp",EDGE,"E88.3.1");var subQ4=sQuery(id+"F39.wireOp",EDGE,"E88.4.0");var subQ5=sQuery(id+"F39.wireOp",EDGE,"E88.2.1");var subQ6=sQuery(id+"F39.wireOp",EDGE,"E88.3.0");var subQ7=sQuery(id+"F39.wireOp",EDGE,"E88.1.1");var subQ8=sQuery(id+"F39.wireOp",EDGE,"E88.2.0");var subQ9=sQuery(id+"F39.wireOp",EDGE,"E87.MirrorCS");var subQ10=sQuery(id+"F39.wireOp",EDGE,"E88.1.0");var subQ11=sQuery(id+"F39.wireOp",EDGE,"E88.4.1");var subQ12=sQuery(id+"F39.wireOp",EDGE,"E88.5.0");var subQ13=sQuery(id+"F39.wireOp",EDGE,"E86");var subQ14=sQuery(id+"F39.wireOp",EDGE,"E88.10.1");var subQ15=sQuery(id+"F39.wireOp",EDGE,"E88.8.1");var subQ16=sQuery(id+"F39.wireOp",EDGE,"E88.9.0");var subQ17=sQuery(id+"F39.wireOp",EDGE,"E88.9.1");var subQ18=sQuery(id+"F39.wireOp",EDGE,"E88.10.0");var subQ19=sQuery(id+"F39.wireOp",EDGE,"E88.6.1");var subQ20=sQuery(id+"F39.wireOp",EDGE,"E88.7.0");var subQ21=sQuery(id+"F39.wireOp",EDGE,"E88.7.1");var subQ22=sQuery(id+"F39.wireOp",EDGE,"E88.8.0");var subQ23=sQuery(id+"F39.wireOp",EDGE,"E88.3.2");Q1=makeQuery(id+"F40.boolean.opBoolean","SPLIT",FACE,{"disambiguationData":[TD([makeQuery(id+"F40.opExtrude","SWEPT_FACE",FACE,{"disambiguationData":[OSD([subQ6])]})])],"derivedFrom":makeQuery(id+"F40.opExtrude","CAP_FACE",FACE,{"disambiguationData":[OSD([subQ1,sQuery(id+"F39.wireOp",EDGE,"E84"),subQ13,subQ9,subQ10,subQ7,sQuery(id+"F39.wireOp",EDGE,"E88.1.2"),subQ8,subQ5,sQuery(id+"F39.wireOp",EDGE,"E88.2.2"),subQ6,subQ3,subQ23,subQ4,subQ11,sQuery(id+"F39.wireOp",EDGE,"E88.4.2"),subQ12,subQ0,sQuery(id+"F39.wireOp",EDGE,"E88.5.2"),subQ2,subQ19,sQuery(id+"F39.wireOp",EDGE,"E88.6.2"),subQ20,subQ21,sQuery(id+"F39.wireOp",EDGE,"E88.7.2"),subQ22,subQ15,sQuery(id+"F39.wireOp",EDGE,"E88.8.2"),subQ16,subQ17,sQuery(id+"F39.wireOp",EDGE,"E88.9.2"),subQ18,subQ14,sQuery(id+"F39.wireOp",EDGE,"E88.10.2"),sQuery(id+"F39.wireOp",EDGE,"E89")])],"isStart":true})});}
            var Q2;
            {var subQ0=sQuery(id+"F39.wireOp",EDGE,"E88.5.1");var subQ1=sQuery(id+"F39.wireOp",EDGE,"E83");var subQ2=sQuery(id+"F39.wireOp",EDGE,"E88.6.0");var subQ3=sQuery(id+"F39.wireOp",EDGE,"E88.6.2");var subQ4=sQuery(id+"F39.wireOp",EDGE,"E88.3.1");var subQ5=sQuery(id+"F39.wireOp",EDGE,"E88.4.0");var subQ6=sQuery(id+"F39.wireOp",EDGE,"E88.2.1");var subQ7=sQuery(id+"F39.wireOp",EDGE,"E88.3.0");var subQ8=sQuery(id+"F39.wireOp",EDGE,"E88.1.1");var subQ9=sQuery(id+"F39.wireOp",EDGE,"E88.2.0");var subQ10=sQuery(id+"F39.wireOp",EDGE,"E87.MirrorCS");var subQ11=sQuery(id+"F39.wireOp",EDGE,"E88.1.0");var subQ12=sQuery(id+"F39.wireOp",EDGE,"E88.4.1");var subQ13=sQuery(id+"F39.wireOp",EDGE,"E88.5.0");var subQ14=sQuery(id+"F39.wireOp",EDGE,"E88.6.1");var subQ15=sQuery(id+"F39.wireOp",EDGE,"E86");var subQ16=sQuery(id+"F39.wireOp",EDGE,"E88.10.1");var subQ17=sQuery(id+"F39.wireOp",EDGE,"E88.8.1");var subQ18=sQuery(id+"F39.wireOp",EDGE,"E88.9.0");var subQ19=sQuery(id+"F39.wireOp",EDGE,"E88.9.1");var subQ20=sQuery(id+"F39.wireOp",EDGE,"E88.10.0");var subQ21=sQuery(id+"F39.wireOp",EDGE,"E88.7.0");var subQ22=sQuery(id+"F39.wireOp",EDGE,"E88.7.1");var subQ23=sQuery(id+"F39.wireOp",EDGE,"E88.8.0");Q2=makeQuery(id+"F40.boolean.opBoolean","SPLIT",FACE,{"disambiguationData":[TD([makeQuery(id+"F40.opExtrude","SWEPT_FACE",FACE,{"disambiguationData":[OSD([subQ2])]})])],"derivedFrom":makeQuery(id+"F40.opExtrude","CAP_FACE",FACE,{"disambiguationData":[OSD([subQ1,sQuery(id+"F39.wireOp",EDGE,"E84"),subQ15,subQ10,subQ11,subQ8,sQuery(id+"F39.wireOp",EDGE,"E88.1.2"),subQ9,subQ6,sQuery(id+"F39.wireOp",EDGE,"E88.2.2"),subQ7,subQ4,sQuery(id+"F39.wireOp",EDGE,"E88.3.2"),subQ5,subQ12,sQuery(id+"F39.wireOp",EDGE,"E88.4.2"),subQ13,subQ0,sQuery(id+"F39.wireOp",EDGE,"E88.5.2"),subQ2,subQ14,subQ3,subQ21,subQ22,sQuery(id+"F39.wireOp",EDGE,"E88.7.2"),subQ23,subQ17,sQuery(id+"F39.wireOp",EDGE,"E88.8.2"),subQ18,subQ19,sQuery(id+"F39.wireOp",EDGE,"E88.9.2"),subQ20,subQ16,sQuery(id+"F39.wireOp",EDGE,"E88.10.2"),sQuery(id+"F39.wireOp",EDGE,"E89")])],"isStart":true})});}
            var Q3;
            {var subQ0=sQuery(id+"F39.wireOp",EDGE,"E88.5.1");var subQ1=sQuery(id+"F39.wireOp",EDGE,"E83");var subQ2=sQuery(id+"F39.wireOp",EDGE,"E88.6.0");var subQ3=sQuery(id+"F39.wireOp",EDGE,"E88.3.1");var subQ4=sQuery(id+"F39.wireOp",EDGE,"E88.4.0");var subQ5=sQuery(id+"F39.wireOp",EDGE,"E88.2.1");var subQ6=sQuery(id+"F39.wireOp",EDGE,"E88.3.0");var subQ7=sQuery(id+"F39.wireOp",EDGE,"E88.5.2");var subQ8=sQuery(id+"F39.wireOp",EDGE,"E88.1.1");var subQ9=sQuery(id+"F39.wireOp",EDGE,"E88.2.0");var subQ10=sQuery(id+"F39.wireOp",EDGE,"E87.MirrorCS");var subQ11=sQuery(id+"F39.wireOp",EDGE,"E88.1.0");var subQ12=sQuery(id+"F39.wireOp",EDGE,"E88.5.0");var subQ13=sQuery(id+"F39.wireOp",EDGE,"E88.4.1");var subQ14=sQuery(id+"F39.wireOp",EDGE,"E86");var subQ15=sQuery(id+"F39.wireOp",EDGE,"E88.10.1");var subQ16=sQuery(id+"F39.wireOp",EDGE,"E88.8.1");var subQ17=sQuery(id+"F39.wireOp",EDGE,"E88.9.0");var subQ18=sQuery(id+"F39.wireOp",EDGE,"E88.9.1");var subQ19=sQuery(id+"F39.wireOp",EDGE,"E88.10.0");var subQ20=sQuery(id+"F39.wireOp",EDGE,"E88.6.1");var subQ21=sQuery(id+"F39.wireOp",EDGE,"E88.7.0");var subQ22=sQuery(id+"F39.wireOp",EDGE,"E88.7.1");var subQ23=sQuery(id+"F39.wireOp",EDGE,"E88.8.0");Q3=makeQuery(id+"F40.boolean.opBoolean","SPLIT",FACE,{"disambiguationData":[TD([makeQuery(id+"F40.opExtrude","SWEPT_FACE",FACE,{"disambiguationData":[OSD([subQ12])]})])],"derivedFrom":makeQuery(id+"F40.opExtrude","CAP_FACE",FACE,{"disambiguationData":[OSD([subQ1,sQuery(id+"F39.wireOp",EDGE,"E84"),subQ14,subQ10,subQ11,subQ8,sQuery(id+"F39.wireOp",EDGE,"E88.1.2"),subQ9,subQ5,sQuery(id+"F39.wireOp",EDGE,"E88.2.2"),subQ6,subQ3,sQuery(id+"F39.wireOp",EDGE,"E88.3.2"),subQ4,subQ13,sQuery(id+"F39.wireOp",EDGE,"E88.4.2"),subQ12,subQ0,subQ7,subQ2,subQ20,sQuery(id+"F39.wireOp",EDGE,"E88.6.2"),subQ21,subQ22,sQuery(id+"F39.wireOp",EDGE,"E88.7.2"),subQ23,subQ16,sQuery(id+"F39.wireOp",EDGE,"E88.8.2"),subQ17,subQ18,sQuery(id+"F39.wireOp",EDGE,"E88.9.2"),subQ19,subQ15,sQuery(id+"F39.wireOp",EDGE,"E88.10.2"),sQuery(id+"F39.wireOp",EDGE,"E89")])],"isStart":true})});}
            var Q4;
            {var subQ0=sQuery(id+"F39.wireOp",EDGE,"E88.5.1");var subQ1=sQuery(id+"F39.wireOp",EDGE,"E83");var subQ2=sQuery(id+"F39.wireOp",EDGE,"E88.6.0");var subQ3=sQuery(id+"F39.wireOp",EDGE,"E88.3.1");var subQ4=sQuery(id+"F39.wireOp",EDGE,"E88.4.0");var subQ5=sQuery(id+"F39.wireOp",EDGE,"E88.2.1");var subQ6=sQuery(id+"F39.wireOp",EDGE,"E88.3.0");var subQ7=sQuery(id+"F39.wireOp",EDGE,"E88.1.1");var subQ8=sQuery(id+"F39.wireOp",EDGE,"E88.2.0");var subQ9=sQuery(id+"F39.wireOp",EDGE,"E87.MirrorCS");var subQ10=sQuery(id+"F39.wireOp",EDGE,"E88.1.0");var subQ11=sQuery(id+"F39.wireOp",EDGE,"E88.4.1");var subQ12=sQuery(id+"F39.wireOp",EDGE,"E88.5.0");var subQ13=sQuery(id+"F39.wireOp",EDGE,"E86");var subQ14=sQuery(id+"F39.wireOp",EDGE,"E88.10.1");var subQ15=sQuery(id+"F39.wireOp",EDGE,"E88.8.1");var subQ16=sQuery(id+"F39.wireOp",EDGE,"E88.9.0");var subQ17=sQuery(id+"F39.wireOp",EDGE,"E88.9.1");var subQ18=sQuery(id+"F39.wireOp",EDGE,"E88.10.0");var subQ19=sQuery(id+"F39.wireOp",EDGE,"E88.6.1");var subQ20=sQuery(id+"F39.wireOp",EDGE,"E88.7.0");var subQ21=sQuery(id+"F39.wireOp",EDGE,"E88.7.1");var subQ22=sQuery(id+"F39.wireOp",EDGE,"E88.8.0");var subQ23=sQuery(id+"F39.wireOp",EDGE,"E88.10.2");Q4=makeQuery(id+"F40.boolean.opBoolean","SPLIT",FACE,{"disambiguationData":[TD([makeQuery(id+"F40.opExtrude","SWEPT_FACE",FACE,{"disambiguationData":[OSD([subQ18])]})])],"derivedFrom":makeQuery(id+"F40.opExtrude","CAP_FACE",FACE,{"disambiguationData":[OSD([subQ1,sQuery(id+"F39.wireOp",EDGE,"E84"),subQ13,subQ9,subQ10,subQ7,sQuery(id+"F39.wireOp",EDGE,"E88.1.2"),subQ8,subQ5,sQuery(id+"F39.wireOp",EDGE,"E88.2.2"),subQ6,subQ3,sQuery(id+"F39.wireOp",EDGE,"E88.3.2"),subQ4,subQ11,sQuery(id+"F39.wireOp",EDGE,"E88.4.2"),subQ12,subQ0,sQuery(id+"F39.wireOp",EDGE,"E88.5.2"),subQ2,subQ19,sQuery(id+"F39.wireOp",EDGE,"E88.6.2"),subQ20,subQ21,sQuery(id+"F39.wireOp",EDGE,"E88.7.2"),subQ22,subQ15,sQuery(id+"F39.wireOp",EDGE,"E88.8.2"),subQ16,subQ17,sQuery(id+"F39.wireOp",EDGE,"E88.9.2"),subQ18,subQ14,subQ23,sQuery(id+"F39.wireOp",EDGE,"E89")])],"isStart":true})});}
            var Q5;
            {var subQ0=sQuery(id+"F39.wireOp",EDGE,"E83");Q5=makeQuery(id+"F40.boolean.opBoolean","MERGE",FACE,{"derivedFrom":[makeQuery(id+"F38.opExtrude","SWEPT_FACE",FACE,{"disambiguationData":[OSD([sQuery(id+"F37.wireOp",EDGE,"E82")])]}),makeQuery(id+"F40.opExtrude","SWEPT_FACE",FACE,{"disambiguationData":[OSD([subQ0]),TDD([makeQuery(id+"F39.imprint","IMPRINT",EDGE,{"disambiguationData":[TD([[makeQuery(id+"F39.imprint","INTERSECT",VERTEX,{"derivedFrom":[subQ0,sQuery(id+"F39.wireOp",EDGE,"E88.8.1")]}),-1.0]])],"derivedFrom":subQ0})])]}),makeQuery(id+"F40.opExtrude","SWEPT_FACE",FACE,{"disambiguationData":[OSD([subQ0]),TDD([makeQuery(id+"F39.imprint","IMPRINT",EDGE,{"disambiguationData":[TD([[makeQuery(id+"F39.imprint","INTERSECT",VERTEX,{"derivedFrom":[subQ0,sQuery(id+"F39.wireOp",EDGE,"E88.9.1")]}),-1.0]])],"derivedFrom":subQ0})])]}),makeQuery(id+"F40.opExtrude","SWEPT_FACE",FACE,{"disambiguationData":[OSD([subQ0]),TDD([makeQuery(id+"F39.imprint","IMPRINT",EDGE,{"disambiguationData":[TD([[makeQuery(id+"F39.imprint","INTERSECT",VERTEX,{"derivedFrom":[subQ0,sQuery(id+"F39.wireOp",EDGE,"E86")]}),1.0]])],"derivedFrom":subQ0})])]}),makeQuery(id+"F40.opExtrude","SWEPT_FACE",FACE,{"disambiguationData":[OSD([subQ0]),TDD([makeQuery(id+"F39.imprint","IMPRINT",EDGE,{"disambiguationData":[TD([[makeQuery(id+"F39.imprint","INTERSECT",VERTEX,{"derivedFrom":[subQ0,sQuery(id+"F39.wireOp",EDGE,"E87.MirrorCS")]}),-1.0]])],"derivedFrom":subQ0})])]}),makeQuery(id+"F40.opExtrude","SWEPT_FACE",FACE,{"disambiguationData":[OSD([subQ0]),TDD([makeQuery(id+"F39.imprint","IMPRINT",EDGE,{"disambiguationData":[TD([[makeQuery(id+"F39.imprint","INTERSECT",VERTEX,{"derivedFrom":[subQ0,sQuery(id+"F39.wireOp",EDGE,"E88.1.1")]}),-1.0]])],"derivedFrom":subQ0})])]}),makeQuery(id+"F40.opExtrude","SWEPT_FACE",FACE,{"disambiguationData":[OSD([subQ0]),TDD([makeQuery(id+"F39.imprint","IMPRINT",EDGE,{"disambiguationData":[TD([[makeQuery(id+"F39.imprint","INTERSECT",VERTEX,{"derivedFrom":[subQ0,sQuery(id+"F39.wireOp",EDGE,"E88.2.1")]}),-1.0]])],"derivedFrom":subQ0})])]}),makeQuery(id+"F40.opExtrude","SWEPT_FACE",FACE,{"disambiguationData":[OSD([subQ0]),TDD([makeQuery(id+"F39.imprint","IMPRINT",EDGE,{"disambiguationData":[TD([[makeQuery(id+"F39.imprint","INTERSECT",VERTEX,{"derivedFrom":[subQ0,sQuery(id+"F39.wireOp",EDGE,"E88.3.1")]}),-1.0]])],"derivedFrom":subQ0})])]}),makeQuery(id+"F40.opExtrude","SWEPT_FACE",FACE,{"disambiguationData":[OSD([subQ0]),TDD([makeQuery(id+"F39.imprint","IMPRINT",EDGE,{"disambiguationData":[TD([[makeQuery(id+"F39.imprint","INTERSECT",VERTEX,{"derivedFrom":[subQ0,sQuery(id+"F39.wireOp",EDGE,"E88.4.1")]}),-1.0]])],"derivedFrom":subQ0})])]}),makeQuery(id+"F40.opExtrude","SWEPT_FACE",FACE,{"disambiguationData":[OSD([subQ0]),TDD([makeQuery(id+"F39.imprint","IMPRINT",EDGE,{"disambiguationData":[TD([[makeQuery(id+"F39.imprint","INTERSECT",VERTEX,{"derivedFrom":[subQ0,sQuery(id+"F39.wireOp",EDGE,"E88.5.1")]}),-1.0]])],"derivedFrom":subQ0})])]}),makeQuery(id+"F40.opExtrude","SWEPT_FACE",FACE,{"disambiguationData":[OSD([subQ0]),TDD([makeQuery(id+"F39.imprint","IMPRINT",EDGE,{"disambiguationData":[TD([[makeQuery(id+"F39.imprint","INTERSECT",VERTEX,{"derivedFrom":[subQ0,sQuery(id+"F39.wireOp",EDGE,"E88.6.1")]}),-1.0]])],"derivedFrom":subQ0})])]}),makeQuery(id+"F40.opExtrude","SWEPT_FACE",FACE,{"disambiguationData":[OSD([subQ0]),TDD([makeQuery(id+"F39.imprint","IMPRINT",EDGE,{"disambiguationData":[TD([[makeQuery(id+"F39.imprint","INTERSECT",VERTEX,{"derivedFrom":[subQ0,sQuery(id+"F39.wireOp",EDGE,"E88.7.1")]}),-1.0]])],"derivedFrom":subQ0})])]})]});}
            var Q6;
            {var subQ0=sQuery(id+"F39.wireOp",EDGE,"E88.5.1");var subQ1=sQuery(id+"F39.wireOp",EDGE,"E83");var subQ2=sQuery(id+"F39.wireOp",EDGE,"E88.6.0");var subQ3=sQuery(id+"F39.wireOp",EDGE,"E88.3.1");var subQ4=sQuery(id+"F39.wireOp",EDGE,"E88.4.0");var subQ5=sQuery(id+"F39.wireOp",EDGE,"E88.2.1");var subQ6=sQuery(id+"F39.wireOp",EDGE,"E88.3.0");var subQ7=sQuery(id+"F39.wireOp",EDGE,"E88.1.1");var subQ8=sQuery(id+"F39.wireOp",EDGE,"E88.2.0");var subQ9=sQuery(id+"F39.wireOp",EDGE,"E87.MirrorCS");var subQ10=sQuery(id+"F39.wireOp",EDGE,"E88.1.0");var subQ11=sQuery(id+"F39.wireOp",EDGE,"E88.4.1");var subQ12=sQuery(id+"F39.wireOp",EDGE,"E88.5.0");var subQ13=sQuery(id+"F39.wireOp",EDGE,"E86");var subQ14=sQuery(id+"F39.wireOp",EDGE,"E88.10.1");var subQ15=sQuery(id+"F39.wireOp",EDGE,"E88.8.1");var subQ16=sQuery(id+"F39.wireOp",EDGE,"E88.9.0");var subQ17=sQuery(id+"F39.wireOp",EDGE,"E88.9.1");var subQ18=sQuery(id+"F39.wireOp",EDGE,"E88.10.0");var subQ19=sQuery(id+"F39.wireOp",EDGE,"E88.6.1");var subQ20=sQuery(id+"F39.wireOp",EDGE,"E88.7.0");var subQ21=sQuery(id+"F39.wireOp",EDGE,"E88.7.1");var subQ22=sQuery(id+"F39.wireOp",EDGE,"E88.8.0");var subQ23=sQuery(id+"F39.wireOp",EDGE,"E88.1.2");Q6=makeQuery(id+"F40.boolean.opBoolean","SPLIT",FACE,{"disambiguationData":[TD([makeQuery(id+"F40.opExtrude","SWEPT_FACE",FACE,{"disambiguationData":[OSD([subQ10])]})])],"derivedFrom":makeQuery(id+"F40.opExtrude","CAP_FACE",FACE,{"disambiguationData":[OSD([subQ1,sQuery(id+"F39.wireOp",EDGE,"E84"),subQ13,subQ9,subQ10,subQ7,subQ23,subQ8,subQ5,sQuery(id+"F39.wireOp",EDGE,"E88.2.2"),subQ6,subQ3,sQuery(id+"F39.wireOp",EDGE,"E88.3.2"),subQ4,subQ11,sQuery(id+"F39.wireOp",EDGE,"E88.4.2"),subQ12,subQ0,sQuery(id+"F39.wireOp",EDGE,"E88.5.2"),subQ2,subQ19,sQuery(id+"F39.wireOp",EDGE,"E88.6.2"),subQ20,subQ21,sQuery(id+"F39.wireOp",EDGE,"E88.7.2"),subQ22,subQ15,sQuery(id+"F39.wireOp",EDGE,"E88.8.2"),subQ16,subQ17,sQuery(id+"F39.wireOp",EDGE,"E88.9.2"),subQ18,subQ14,sQuery(id+"F39.wireOp",EDGE,"E88.10.2"),sQuery(id+"F39.wireOp",EDGE,"E89")])],"isStart":true})});}
            var Q7;
            {var subQ0=sQuery(id+"F39.wireOp",EDGE,"E88.5.1");var subQ1=sQuery(id+"F39.wireOp",EDGE,"E83");var subQ2=sQuery(id+"F39.wireOp",EDGE,"E88.6.0");var subQ3=sQuery(id+"F39.wireOp",EDGE,"E88.3.1");var subQ4=sQuery(id+"F39.wireOp",EDGE,"E88.4.0");var subQ5=sQuery(id+"F39.wireOp",EDGE,"E88.2.1");var subQ6=sQuery(id+"F39.wireOp",EDGE,"E88.3.0");var subQ7=sQuery(id+"F39.wireOp",EDGE,"E88.1.1");var subQ8=sQuery(id+"F39.wireOp",EDGE,"E88.2.0");var subQ9=sQuery(id+"F39.wireOp",EDGE,"E87.MirrorCS");var subQ10=sQuery(id+"F39.wireOp",EDGE,"E88.1.0");var subQ11=sQuery(id+"F39.wireOp",EDGE,"E88.4.1");var subQ12=sQuery(id+"F39.wireOp",EDGE,"E88.5.0");var subQ13=sQuery(id+"F39.wireOp",EDGE,"E84");var subQ14=sQuery(id+"F39.wireOp",EDGE,"E86");var subQ15=sQuery(id+"F39.wireOp",EDGE,"E88.10.1");var subQ16=sQuery(id+"F39.wireOp",EDGE,"E88.8.1");var subQ17=sQuery(id+"F39.wireOp",EDGE,"E88.9.0");var subQ18=sQuery(id+"F39.wireOp",EDGE,"E88.9.1");var subQ19=sQuery(id+"F39.wireOp",EDGE,"E88.10.0");var subQ20=sQuery(id+"F39.wireOp",EDGE,"E88.6.1");var subQ21=sQuery(id+"F39.wireOp",EDGE,"E88.7.0");var subQ22=sQuery(id+"F39.wireOp",EDGE,"E88.7.1");var subQ23=sQuery(id+"F39.wireOp",EDGE,"E88.8.0");Q7=makeQuery(id+"F40.boolean.opBoolean","SPLIT",FACE,{"disambiguationData":[TD([makeQuery(id+"F40.opExtrude","SWEPT_FACE",FACE,{"disambiguationData":[OSD([subQ13])]})])],"derivedFrom":makeQuery(id+"F40.opExtrude","CAP_FACE",FACE,{"disambiguationData":[OSD([subQ1,subQ13,subQ14,subQ9,subQ10,subQ7,sQuery(id+"F39.wireOp",EDGE,"E88.1.2"),subQ8,subQ5,sQuery(id+"F39.wireOp",EDGE,"E88.2.2"),subQ6,subQ3,sQuery(id+"F39.wireOp",EDGE,"E88.3.2"),subQ4,subQ11,sQuery(id+"F39.wireOp",EDGE,"E88.4.2"),subQ12,subQ0,sQuery(id+"F39.wireOp",EDGE,"E88.5.2"),subQ2,subQ20,sQuery(id+"F39.wireOp",EDGE,"E88.6.2"),subQ21,subQ22,sQuery(id+"F39.wireOp",EDGE,"E88.7.2"),subQ23,subQ16,sQuery(id+"F39.wireOp",EDGE,"E88.8.2"),subQ17,subQ18,sQuery(id+"F39.wireOp",EDGE,"E88.9.2"),subQ19,subQ15,sQuery(id+"F39.wireOp",EDGE,"E88.10.2"),sQuery(id+"F39.wireOp",EDGE,"E89")])],"isStart":true})});}
            var Q8;
            {var subQ0=sQuery(id+"F39.wireOp",EDGE,"E88.5.1");var subQ1=sQuery(id+"F39.wireOp",EDGE,"E83");var subQ2=sQuery(id+"F39.wireOp",EDGE,"E88.6.0");var subQ3=sQuery(id+"F39.wireOp",EDGE,"E88.3.1");var subQ4=sQuery(id+"F39.wireOp",EDGE,"E88.4.0");var subQ5=sQuery(id+"F39.wireOp",EDGE,"E88.2.1");var subQ6=sQuery(id+"F39.wireOp",EDGE,"E88.3.0");var subQ7=sQuery(id+"F39.wireOp",EDGE,"E88.1.1");var subQ8=sQuery(id+"F39.wireOp",EDGE,"E88.2.0");var subQ9=sQuery(id+"F39.wireOp",EDGE,"E87.MirrorCS");var subQ10=sQuery(id+"F39.wireOp",EDGE,"E88.1.0");var subQ11=sQuery(id+"F39.wireOp",EDGE,"E88.4.1");var subQ12=sQuery(id+"F39.wireOp",EDGE,"E88.5.0");var subQ13=sQuery(id+"F39.wireOp",EDGE,"E86");var subQ14=sQuery(id+"F39.wireOp",EDGE,"E88.10.1");var subQ15=sQuery(id+"F39.wireOp",EDGE,"E88.4.2");var subQ16=sQuery(id+"F39.wireOp",EDGE,"E88.8.1");var subQ17=sQuery(id+"F39.wireOp",EDGE,"E88.9.0");var subQ18=sQuery(id+"F39.wireOp",EDGE,"E88.9.1");var subQ19=sQuery(id+"F39.wireOp",EDGE,"E88.10.0");var subQ20=sQuery(id+"F39.wireOp",EDGE,"E88.6.1");var subQ21=sQuery(id+"F39.wireOp",EDGE,"E88.7.0");var subQ22=sQuery(id+"F39.wireOp",EDGE,"E88.7.1");var subQ23=sQuery(id+"F39.wireOp",EDGE,"E88.8.0");Q8=makeQuery(id+"F40.boolean.opBoolean","SPLIT",FACE,{"disambiguationData":[TD([makeQuery(id+"F40.opExtrude","SWEPT_FACE",FACE,{"disambiguationData":[OSD([subQ4])]})])],"derivedFrom":makeQuery(id+"F40.opExtrude","CAP_FACE",FACE,{"disambiguationData":[OSD([subQ1,sQuery(id+"F39.wireOp",EDGE,"E84"),subQ13,subQ9,subQ10,subQ7,sQuery(id+"F39.wireOp",EDGE,"E88.1.2"),subQ8,subQ5,sQuery(id+"F39.wireOp",EDGE,"E88.2.2"),subQ6,subQ3,sQuery(id+"F39.wireOp",EDGE,"E88.3.2"),subQ4,subQ11,subQ15,subQ12,subQ0,sQuery(id+"F39.wireOp",EDGE,"E88.5.2"),subQ2,subQ20,sQuery(id+"F39.wireOp",EDGE,"E88.6.2"),subQ21,subQ22,sQuery(id+"F39.wireOp",EDGE,"E88.7.2"),subQ23,subQ16,sQuery(id+"F39.wireOp",EDGE,"E88.8.2"),subQ17,subQ18,sQuery(id+"F39.wireOp",EDGE,"E88.9.2"),subQ19,subQ14,sQuery(id+"F39.wireOp",EDGE,"E88.10.2"),sQuery(id+"F39.wireOp",EDGE,"E89")])],"isStart":true})});}
            var Q9;
            {var subQ0=sQuery(id+"F39.wireOp",EDGE,"E88.5.1");var subQ1=sQuery(id+"F39.wireOp",EDGE,"E83");var subQ2=sQuery(id+"F39.wireOp",EDGE,"E88.6.0");var subQ3=sQuery(id+"F39.wireOp",EDGE,"E88.3.1");var subQ4=sQuery(id+"F39.wireOp",EDGE,"E88.4.0");var subQ5=sQuery(id+"F39.wireOp",EDGE,"E88.2.1");var subQ6=sQuery(id+"F39.wireOp",EDGE,"E88.3.0");var subQ7=sQuery(id+"F39.wireOp",EDGE,"E88.1.1");var subQ8=sQuery(id+"F39.wireOp",EDGE,"E88.2.0");var subQ9=sQuery(id+"F39.wireOp",EDGE,"E87.MirrorCS");var subQ10=sQuery(id+"F39.wireOp",EDGE,"E88.1.0");var subQ11=sQuery(id+"F39.wireOp",EDGE,"E88.4.1");var subQ12=sQuery(id+"F39.wireOp",EDGE,"E88.5.0");var subQ13=sQuery(id+"F39.wireOp",EDGE,"E86");var subQ14=sQuery(id+"F39.wireOp",EDGE,"E88.10.1");var subQ15=sQuery(id+"F39.wireOp",EDGE,"E88.8.1");var subQ16=sQuery(id+"F39.wireOp",EDGE,"E88.9.0");var subQ17=sQuery(id+"F39.wireOp",EDGE,"E88.9.1");var subQ18=sQuery(id+"F39.wireOp",EDGE,"E88.10.0");var subQ19=sQuery(id+"F39.wireOp",EDGE,"E88.6.1");var subQ20=sQuery(id+"F39.wireOp",EDGE,"E88.7.0");var subQ21=sQuery(id+"F39.wireOp",EDGE,"E88.7.1");var subQ22=sQuery(id+"F39.wireOp",EDGE,"E88.8.0");var subQ23=sQuery(id+"F39.wireOp",EDGE,"E88.8.2");Q9=makeQuery(id+"F40.boolean.opBoolean","SPLIT",FACE,{"disambiguationData":[TD([makeQuery(id+"F40.opExtrude","SWEPT_FACE",FACE,{"disambiguationData":[OSD([subQ22])]})])],"derivedFrom":makeQuery(id+"F40.opExtrude","CAP_FACE",FACE,{"disambiguationData":[OSD([subQ1,sQuery(id+"F39.wireOp",EDGE,"E84"),subQ13,subQ9,subQ10,subQ7,sQuery(id+"F39.wireOp",EDGE,"E88.1.2"),subQ8,subQ5,sQuery(id+"F39.wireOp",EDGE,"E88.2.2"),subQ6,subQ3,sQuery(id+"F39.wireOp",EDGE,"E88.3.2"),subQ4,subQ11,sQuery(id+"F39.wireOp",EDGE,"E88.4.2"),subQ12,subQ0,sQuery(id+"F39.wireOp",EDGE,"E88.5.2"),subQ2,subQ19,sQuery(id+"F39.wireOp",EDGE,"E88.6.2"),subQ20,subQ21,sQuery(id+"F39.wireOp",EDGE,"E88.7.2"),subQ22,subQ15,subQ23,subQ16,subQ17,sQuery(id+"F39.wireOp",EDGE,"E88.9.2"),subQ18,subQ14,sQuery(id+"F39.wireOp",EDGE,"E88.10.2"),sQuery(id+"F39.wireOp",EDGE,"E89")])],"isStart":true})});}
            var Q10;
            {var subQ0=sQuery(id+"F39.wireOp",EDGE,"E88.5.1");var subQ1=sQuery(id+"F39.wireOp",EDGE,"E83");var subQ2=sQuery(id+"F39.wireOp",EDGE,"E88.6.0");var subQ3=sQuery(id+"F39.wireOp",EDGE,"E88.3.1");var subQ4=sQuery(id+"F39.wireOp",EDGE,"E88.4.0");var subQ5=sQuery(id+"F39.wireOp",EDGE,"E88.2.1");var subQ6=sQuery(id+"F39.wireOp",EDGE,"E88.3.0");var subQ7=sQuery(id+"F39.wireOp",EDGE,"E88.1.1");var subQ8=sQuery(id+"F39.wireOp",EDGE,"E88.2.0");var subQ9=sQuery(id+"F39.wireOp",EDGE,"E87.MirrorCS");var subQ10=sQuery(id+"F39.wireOp",EDGE,"E88.1.0");var subQ11=sQuery(id+"F39.wireOp",EDGE,"E88.4.1");var subQ12=sQuery(id+"F39.wireOp",EDGE,"E88.5.0");var subQ13=sQuery(id+"F39.wireOp",EDGE,"E86");var subQ14=sQuery(id+"F39.wireOp",EDGE,"E88.10.1");var subQ15=sQuery(id+"F39.wireOp",EDGE,"E88.8.1");var subQ16=sQuery(id+"F39.wireOp",EDGE,"E88.9.0");var subQ17=sQuery(id+"F39.wireOp",EDGE,"E88.9.1");var subQ18=sQuery(id+"F39.wireOp",EDGE,"E88.10.0");var subQ19=sQuery(id+"F39.wireOp",EDGE,"E88.6.1");var subQ20=sQuery(id+"F39.wireOp",EDGE,"E88.7.0");var subQ21=sQuery(id+"F39.wireOp",EDGE,"E88.7.1");var subQ22=sQuery(id+"F39.wireOp",EDGE,"E88.8.0");var subQ23=sQuery(id+"F39.wireOp",EDGE,"E88.9.2");Q10=makeQuery(id+"F40.boolean.opBoolean","SPLIT",FACE,{"disambiguationData":[TD([makeQuery(id+"F40.opExtrude","SWEPT_FACE",FACE,{"disambiguationData":[OSD([subQ16])]})])],"derivedFrom":makeQuery(id+"F40.opExtrude","CAP_FACE",FACE,{"disambiguationData":[OSD([subQ1,sQuery(id+"F39.wireOp",EDGE,"E84"),subQ13,subQ9,subQ10,subQ7,sQuery(id+"F39.wireOp",EDGE,"E88.1.2"),subQ8,subQ5,sQuery(id+"F39.wireOp",EDGE,"E88.2.2"),subQ6,subQ3,sQuery(id+"F39.wireOp",EDGE,"E88.3.2"),subQ4,subQ11,sQuery(id+"F39.wireOp",EDGE,"E88.4.2"),subQ12,subQ0,sQuery(id+"F39.wireOp",EDGE,"E88.5.2"),subQ2,subQ19,sQuery(id+"F39.wireOp",EDGE,"E88.6.2"),subQ20,subQ21,sQuery(id+"F39.wireOp",EDGE,"E88.7.2"),subQ22,subQ15,sQuery(id+"F39.wireOp",EDGE,"E88.8.2"),subQ16,subQ17,subQ23,subQ18,subQ14,sQuery(id+"F39.wireOp",EDGE,"E88.10.2"),sQuery(id+"F39.wireOp",EDGE,"E89")])],"isStart":true})});}
            var Q11;
            {var subQ0=sQuery(id+"F39.wireOp",EDGE,"E88.5.1");var subQ1=sQuery(id+"F39.wireOp",EDGE,"E83");var subQ2=sQuery(id+"F39.wireOp",EDGE,"E88.6.0");var subQ3=sQuery(id+"F39.wireOp",EDGE,"E88.3.1");var subQ4=sQuery(id+"F39.wireOp",EDGE,"E88.4.0");var subQ5=sQuery(id+"F39.wireOp",EDGE,"E88.2.1");var subQ6=sQuery(id+"F39.wireOp",EDGE,"E88.3.0");var subQ7=sQuery(id+"F39.wireOp",EDGE,"E88.1.1");var subQ8=sQuery(id+"F39.wireOp",EDGE,"E88.2.0");var subQ9=sQuery(id+"F39.wireOp",EDGE,"E87.MirrorCS");var subQ10=sQuery(id+"F39.wireOp",EDGE,"E88.1.0");var subQ11=sQuery(id+"F39.wireOp",EDGE,"E88.4.1");var subQ12=sQuery(id+"F39.wireOp",EDGE,"E88.5.0");var subQ13=sQuery(id+"F39.wireOp",EDGE,"E86");var subQ14=sQuery(id+"F39.wireOp",EDGE,"E88.10.1");var subQ15=sQuery(id+"F39.wireOp",EDGE,"E88.8.1");var subQ16=sQuery(id+"F39.wireOp",EDGE,"E88.9.0");var subQ17=sQuery(id+"F39.wireOp",EDGE,"E88.9.1");var subQ18=sQuery(id+"F39.wireOp",EDGE,"E88.10.0");var subQ19=sQuery(id+"F39.wireOp",EDGE,"E88.6.1");var subQ20=sQuery(id+"F39.wireOp",EDGE,"E88.7.0");var subQ21=sQuery(id+"F39.wireOp",EDGE,"E88.7.1");var subQ22=sQuery(id+"F39.wireOp",EDGE,"E88.8.0");var subQ23=sQuery(id+"F39.wireOp",EDGE,"E88.2.2");Q11=makeQuery(id+"F40.boolean.opBoolean","SPLIT",FACE,{"disambiguationData":[TD([makeQuery(id+"F40.opExtrude","SWEPT_FACE",FACE,{"disambiguationData":[OSD([subQ8])]})])],"derivedFrom":makeQuery(id+"F40.opExtrude","CAP_FACE",FACE,{"disambiguationData":[OSD([subQ1,sQuery(id+"F39.wireOp",EDGE,"E84"),subQ13,subQ9,subQ10,subQ7,sQuery(id+"F39.wireOp",EDGE,"E88.1.2"),subQ8,subQ5,subQ23,subQ6,subQ3,sQuery(id+"F39.wireOp",EDGE,"E88.3.2"),subQ4,subQ11,sQuery(id+"F39.wireOp",EDGE,"E88.4.2"),subQ12,subQ0,sQuery(id+"F39.wireOp",EDGE,"E88.5.2"),subQ2,subQ19,sQuery(id+"F39.wireOp",EDGE,"E88.6.2"),subQ20,subQ21,sQuery(id+"F39.wireOp",EDGE,"E88.7.2"),subQ22,subQ15,sQuery(id+"F39.wireOp",EDGE,"E88.8.2"),subQ16,subQ17,sQuery(id+"F39.wireOp",EDGE,"E88.9.2"),subQ18,subQ14,sQuery(id+"F39.wireOp",EDGE,"E88.10.2"),sQuery(id+"F39.wireOp",EDGE,"E89")])],"isStart":true})});}
            fillet(context, id + "F50", {"entities" : qUnion([Q0, Q1, Q2, Q3, Q4, Q5, Q6, Q7, Q8, Q9, Q10, Q11]), "radius" : .5 * mm, "tangentPropagation" : true, "allowEdgeOverflow" : false});
        }
        {
            var Q0;
            Q0=makeQuery(id+"F47.opFillet","BLEND_FACE",FACE,{"disambiguationData":[OSD([sQuery(id+"F31.wireOp",EDGE,"E71.1.1")])]});
            var Q1;
            Q1=makeQuery(id+"F40.opExtrude","CAP_FACE",FACE,{"disambiguationData":[OSD([sQuery(id+"F39.wireOp",EDGE,"E83"),sQuery(id+"F39.wireOp",EDGE,"E84"),sQuery(id+"F39.wireOp",EDGE,"E86"),sQuery(id+"F39.wireOp",EDGE,"E87.MirrorCS"),sQuery(id+"F39.wireOp",EDGE,"E88.1.0"),sQuery(id+"F39.wireOp",EDGE,"E88.1.1"),sQuery(id+"F39.wireOp",EDGE,"E88.1.2"),sQuery(id+"F39.wireOp",EDGE,"E88.2.0"),sQuery(id+"F39.wireOp",EDGE,"E88.2.1"),sQuery(id+"F39.wireOp",EDGE,"E88.2.2"),sQuery(id+"F39.wireOp",EDGE,"E88.3.0"),sQuery(id+"F39.wireOp",EDGE,"E88.3.1"),sQuery(id+"F39.wireOp",EDGE,"E88.3.2"),sQuery(id+"F39.wireOp",EDGE,"E88.4.0"),sQuery(id+"F39.wireOp",EDGE,"E88.4.1"),sQuery(id+"F39.wireOp",EDGE,"E88.4.2"),sQuery(id+"F39.wireOp",EDGE,"E88.5.0"),sQuery(id+"F39.wireOp",EDGE,"E88.5.1"),sQuery(id+"F39.wireOp",EDGE,"E88.5.2"),sQuery(id+"F39.wireOp",EDGE,"E88.6.0"),sQuery(id+"F39.wireOp",EDGE,"E88.6.1"),sQuery(id+"F39.wireOp",EDGE,"E88.6.2"),sQuery(id+"F39.wireOp",EDGE,"E88.7.0"),sQuery(id+"F39.wireOp",EDGE,"E88.7.1"),sQuery(id+"F39.wireOp",EDGE,"E88.7.2"),sQuery(id+"F39.wireOp",EDGE,"E88.8.0"),sQuery(id+"F39.wireOp",EDGE,"E88.8.1"),sQuery(id+"F39.wireOp",EDGE,"E88.8.2"),sQuery(id+"F39.wireOp",EDGE,"E88.9.0"),sQuery(id+"F39.wireOp",EDGE,"E88.9.1"),sQuery(id+"F39.wireOp",EDGE,"E88.9.2"),sQuery(id+"F39.wireOp",EDGE,"E88.10.0"),sQuery(id+"F39.wireOp",EDGE,"E88.10.1"),sQuery(id+"F39.wireOp",EDGE,"E88.10.2"),sQuery(id+"F39.wireOp",EDGE,"E89")])],"isStart":false});
            fillet(context, id + "F51", {"entities" : qUnion([Q0, Q1]), "radius" : .5 * mm, "tangentPropagation" : true, "allowEdgeOverflow" : false});
        }
    });
